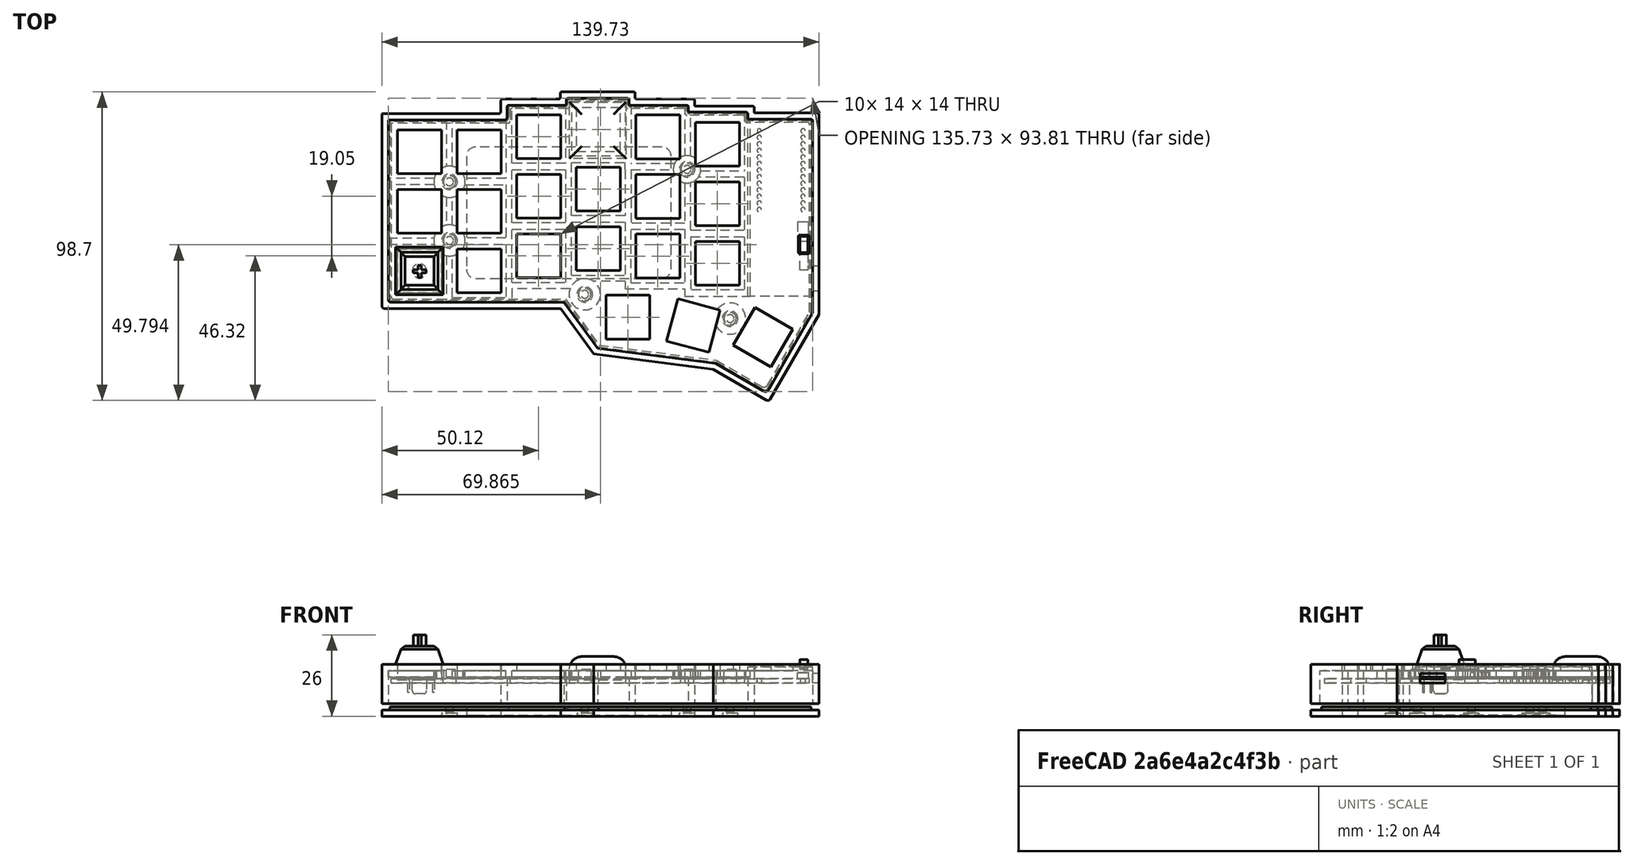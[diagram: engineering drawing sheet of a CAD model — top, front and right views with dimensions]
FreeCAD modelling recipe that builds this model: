
FCSTD DOCUMENT  (FreeCAD 0.22R37841 (Git))
Label: Corne 42 Case Clone
License: All rights reserved
LicenseURL: http://en.wikipedia.org/wiki/All_rights_reserved
objects: Sketcher::SketchObject×38, PartDesign::Pad×18, PartDesign::Pocket×13, PartDesign::Body×6, PartDesign::Fillet×3, App::DocumentObjectGroup×2, PartDesign::ShapeBinder×2, Spreadsheet::Sheet×1, Mesh::Feature×1, PartDesign::Chamfer×1
note: 116 computed .brp shape members not serialized (recipe doc carries the construction recipe); baked Part::Feature solids carry a one-line shape summary decoded from their .brp

FEATURE [Spreadsheet::Sheet] Spreadsheet
  cells = A1='PCBInnerBorderSpacing; B1(PCBInnerBorderSpacing)=1; A2='CaseTopBorderWitdh; B2(CaseTopBorderWitdh)=2; A3='SwitchBorderSpacing; B3(SwitchBorderSpacing)=2; A4='PCBBorderRadius; B4(PCBBorderRadius)=0.632; A5='PCBSmallStep; B5(PCBSmallStep)=2.25; A6='PCBBigStep; B6(PCBBigStep)=4.75; A7='SwitchplateHeight; B7(SwitchplateHeight)=2; A8='CaseTopTopBorderHeight; B8(CaseTopTopBorderHeight)=7; A9='CaseTopBottomBorderHeight; B9(CaseTopBottomBorderHeight)=6; A10='CaseColumnDiameter; B10(CaseColumnDiameter)=5; A11='ThreadedInsertHeight; B11(ThreadedInsertHeight)=3; A12='ThreadedInsertExtDiameter; B12(ThreadedInsertExtDiameter)=3.9; A13='PCBHoleSize; B13(PCBHoleSize)=4.2; A14='USBCPocketWidth; B14(USBCPocketWidth)=13.2; A15='USBCPocketHEIGHT; B15(USBCPocketHeight)=7.4; A16='CaseBottomPartHeight; B16(CaseBottomPartHeight)==CaseBottomFloorHeight + CaseBottomBorder; A17='CaseBottomFloorHeight; B17(CaseBottomFloorHeight)=3; A18='CaseBottomBorder; B18(CaseBottomBorder)=10; A19='ShadowLineWidth; B19(ShadowLineWidth)==CaseTopBorderWitdh - ShadowLineLipWidth; A20='ShadowLineLipWidth; B20(ShadowLineLipWidth)=0.6; A21='ResetSwitchHeight; B21(ResetSwitchHeight)=2.6; A22='PowerSwitchHeight; B22(PowerSwitchHeight)==3 - 1.4
FEATURE [Sketcher::SketchObject] MirroredSketch003  label="PCB.Borders"
  FullyConstrained = true
  expr: Constraints[41] = Spreadsheet.PCBBorderRadius
  expr: Constraints[44] = Spreadsheet.PCBBorderRadius
  expr: Constraints[47] = Spreadsheet.PCBBorderRadius
  expr: Constraints[52] = Spreadsheet.PCBBorderRadius
  expr: Constraints[53] = Spreadsheet.PCBBorderRadius
  expr: Constraints[56] = Spreadsheet.PCBBorderRadius
  expr: Constraints[59] = Spreadsheet.PCBBorderRadius
  expr: Constraints[62] = Spreadsheet.PCBBorderRadius
  expr: Constraints[65] = Spreadsheet.PCBBorderRadius
  expr: Constraints[68] = Spreadsheet.PCBBorderRadius
  expr: Constraints[74] = Spreadsheet.PCBBorderRadius
  expr: Constraints[79] = Spreadsheet.PCBBorderRadius
  expr: Constraints[86] = Spreadsheet.PCBSmallStep
  expr: Constraints[87] = Spreadsheet.PCBSmallStep
  expr: Constraints[88] = Spreadsheet.PCBSmallStep
  expr: Constraints[89] = Spreadsheet.PCBSmallStep
  expr: Constraints[90] = Spreadsheet.PCBBigStep
  sketch-geometry (38):
    g0: LineSegment StartX=0 StartY=56.25 StartZ=0 EndX=0 EndY=0.632 EndZ=0
    g1: LineSegment StartX=0.632 StartY=0 StartZ=0 EndX=55.6983 EndY=0 EndZ=0
    g2: LineSegment StartX=55.6983 StartY=0 StartZ=0 EndX=66.4243 EndY=-14.7035 EndZ=0
    g3: LineSegment StartX=66.4243 StartY=-14.7035 StartZ=0 EndX=103.928 EndY=-19.5811 EndZ=0
    g4: LineSegment StartX=103.928 StartY=-19.5811 StartZ=0 EndX=118.437 EndY=-27.9743 EndZ=0
    g5: LineSegment StartX=120.31 StartY=-27.472 StartZ=0 EndX=133.73 EndY=-4.162 EndZ=0
    g6: LineSegment StartX=133.73 StartY=-4.162 StartZ=0 EndX=133.73 EndY=55.868 EndZ=0
    g7: LineSegment StartX=133.098 StartY=56.5 StartZ=0 EndX=113.612 EndY=56.5 EndZ=0
    g8: LineSegment StartX=112.98 StartY=57.132 StartZ=0 EndX=112.98 EndY=58.118 EndZ=0
    g9: LineSegment StartX=112.348 StartY=58.75 StartZ=0 EndX=94.612 EndY=58.75 EndZ=0
    g10: LineSegment StartX=93.98 StartY=59.382 StartZ=0 EndX=93.98 EndY=60.368 EndZ=0
    g11: LineSegment StartX=93.348 StartY=61 StartZ=0 EndX=75.612 EndY=61 EndZ=0
    g12: LineSegment StartX=74.98 StartY=61.632 StartZ=0 EndX=74.98 EndY=62.618 EndZ=0
    g13: LineSegment StartX=74.348 StartY=63.25 StartZ=0 EndX=57.612 EndY=63.25 EndZ=0
    g14: LineSegment StartX=56.98 StartY=62.618 StartZ=0 EndX=56.98 EndY=61.632 EndZ=0
    g15: LineSegment StartX=56.348 StartY=61 StartZ=0 EndX=38.612 EndY=61 EndZ=0
    g16: LineSegment StartX=37.98 StartY=60.368 StartZ=0 EndX=37.98 EndY=56.882 EndZ=0
    g17: LineSegment StartX=37.348 StartY=56.25 StartZ=0 EndX=0 EndY=56.25 EndZ=0
    g18: Circle CenterX=18.61 CenterY=37.51 CenterZ=0 NormalX=0 NormalY=0 NormalZ=1 AngleXU=0 Radius=2.15
    g19: Circle CenterX=18.6 CenterY=18.76 CenterZ=0 NormalX=0 NormalY=0 NormalZ=1 AngleXU=0 Radius=2.15
    g20: Circle CenterX=108.3 CenterY=-6.24 CenterZ=0 NormalX=0 NormalY=0 NormalZ=1 AngleXU=0 Radius=2.15
    g21: Circle CenterX=94.55 CenterY=41.5 CenterZ=0 NormalX=0 NormalY=0 NormalZ=1 AngleXU=0 Radius=2.15
    g22: Circle CenterX=61.84 CenterY=1.51 CenterZ=0 NormalX=0 NormalY=0 NormalZ=1 AngleXU=0 Radius=2.15
    g23: ArcOfCircle CenterX=37.348 CenterY=56.882 CenterZ=0 NormalX=0 NormalY=0 NormalZ=1 AngleXU=0 Radius=0.632 StartAngle=4.71239 EndAngle=6.28319
    g24: ArcOfCircle CenterX=56.348 CenterY=61.632 CenterZ=0 NormalX=0 NormalY=0 NormalZ=1 AngleXU=0 Radius=0.632 StartAngle=4.71239 EndAngle=6.28319
    g25: ArcOfCircle CenterX=75.612 CenterY=61.632 CenterZ=0 NormalX=0 NormalY=0 NormalZ=1 AngleXU=0 Radius=0.632 StartAngle=3.14159 EndAngle=4.71239
    g26: ArcOfCircle CenterX=57.612 CenterY=62.618 CenterZ=0 NormalX=0 NormalY=0 NormalZ=1 AngleXU=0 Radius=0.632 StartAngle=1.5708 EndAngle=3.14159
    g27: ArcOfCircle CenterX=74.348 CenterY=62.618 CenterZ=0 NormalX=0 NormalY=0 NormalZ=1 AngleXU=0 Radius=0.632 StartAngle=5e-15 EndAngle=1.5708
    g28: ArcOfCircle CenterX=93.348 CenterY=60.368 CenterZ=0 NormalX=0 NormalY=0 NormalZ=1 AngleXU=0 Radius=0.632 StartAngle=-9e-16 EndAngle=1.5708
    g29: ArcOfCircle CenterX=94.612 CenterY=59.382 CenterZ=0 NormalX=0 NormalY=0 NormalZ=1 AngleXU=0 Radius=0.632 StartAngle=3.14159 EndAngle=4.71239
    g30: ArcOfCircle CenterX=112.348 CenterY=58.118 CenterZ=0 NormalX=0 NormalY=0 NormalZ=1 AngleXU=0 Radius=0.632 StartAngle=-9e-16 EndAngle=1.5708
    g31: ArcOfCircle CenterX=113.612 CenterY=57.132 CenterZ=0 NormalX=0 NormalY=0 NormalZ=1 AngleXU=0 Radius=0.632 StartAngle=3.14159 EndAngle=4.71239
    g32: ArcOfCircle CenterX=133.098 CenterY=55.868 CenterZ=0 NormalX=0 NormalY=0 NormalZ=1 AngleXU=0 Radius=0.632 StartAngle=-5.3e-15 EndAngle=1.5708
    g33: ArcOfCircle CenterX=119.123 CenterY=-26.7885 CenterZ=0 NormalX=0 NormalY=0 NormalZ=1 AngleXU=0 Radius=1.37 StartAngle=4.18792 EndAngle=5.76081
    g34: ArcOfCircle CenterX=0.632 CenterY=0.632 CenterZ=0 NormalX=0 NormalY=0 NormalZ=1 AngleXU=0 Radius=0.632 StartAngle=3.14159 EndAngle=4.71239
    g35: ArcOfCircle CenterX=38.612 CenterY=60.368 CenterZ=0 NormalX=0 NormalY=0 NormalZ=1 AngleXU=0 Radius=0.632 StartAngle=1.5708 EndAngle=3.14159
    g36: LineSegment StartX=122.07 StartY=-24.4153 StartZ=0 EndX=119.625 EndY=-28.6618 EndZ=0
    g37: LineSegment StartX=116.44 StartY=-26.819 StartZ=0 EndX=119.625 EndY=-28.6618 EndZ=0
  constraints (102):
    c: Horizontal(g1)
    c: Vertical(g0)
    c: Coincident(g1,g2)
    c: Coincident(g2,g3)
    c: Coincident(g3,g4)
    c: Coincident(g5,g6)
    c: Coincident(g17,g0)
    c: Vertical(g6)
    c: Horizontal(g7)
    c: Horizontal(g9)
    c: Horizontal(g11)
    c: Horizontal(g13)
    c: Horizontal(g15)
    c: Horizontal(g17)
    c: Vertical(g16)
    c: Vertical(g14)
    c: Vertical(g12)
    c: Vertical(g10)
    c: Vertical(g8)
    c: Angle(g5,g6) = -2.61922
    c: Angle(g4,g5) = -1.5687
    c: Angle(g4,g3) = -2.74645
    c: Angle(g2,g3) = -2.33036
    c: Diameter(g20) = 4.3
    c: Diameter(g21) = 4.3
    c: Diameter(g18) = 4.3
    c: Diameter(g19) = 4.3
    c: Distance(g18,g0) = 18.61
    c: Distance(g19,g18) = 18.75
    c: Distance(g19,g0) = 18.6
    c: Distance(g21,g6) = 39.18
    c: Distance(g21,g9) = 17.25
    c: Distance(g20,g6) = 25.43
    c: Distance(g3) = 37.82
    c: Distance(g19,g1) = 18.76
    c: Diameter(g22) = 4.3
    c: DistanceX(g19,g22) = 43.24
    c: DistanceY(g22,g19) = 17.25
    c: DistanceY(g20,g22) = 7.75
    c: Tangent(g16,g23) = 1.5708
    c: Tangent(g17,g23) = 1.5708
    c: Radius(g23) = 0.632
    c: Tangent(g14,g24) = 1.5708
    c: Tangent(g15,g24) = 1.5708
    c: Radius(g24) = 0.632
    c: Tangent(g12,g25) = 1.5708
    c: Tangent(g11,g25) = 1.5708
    c: Radius(g25) = 0.632
    c: Tangent(g13,g26) = -1.5708
    c: Tangent(g14,g26) = -1.5708
    c: Tangent(g13,g27) = -1.5708
    c: Tangent(g12,g27) = -1.5708
    c: Radius(g26) = 0.632
    c: Radius(g27) = 0.632
    c: Tangent(g11,g28) = -1.5708
    c: Tangent(g10,g28) = -1.5708
    c: Radius(g28) = 0.632
    c: Tangent(g10,g29) = 1.5708
    c: Tangent(g9,g29) = 1.5708
    c: Radius(g29) = 0.632
    c: Tangent(g9,g30) = -1.5708
    c: Tangent(g8,g30) = -1.5708
    c: Radius(g30) = 0.632
    c: Tangent(g8,g31) = 1.5708
    c: Tangent(g7,g31) = 1.5708
    c: Radius(g31) = 0.632
    c: Tangent(g7,g32) = -1.5708
    c: Tangent(g6,g32) = -1.5708
    c: Radius(g32) = 0.632
    c: Tangent(g5,g33) = -1.5708
    c: Tangent(g4,g33) = -1.5708
    c: Radius(g33) = 1.37
    c: Tangent(g1,g34) = -1.5708
    c: Tangent(g0,g34) = -1.5708
    c: Radius(g34) = 0.632
    c: DistanceY(g-1,g1) = 0
    c: DistanceX(g-2,g0) = 0
    c: Tangent(g15,g35) = -1.5708
    c: Tangent(g16,g35) = -1.5708
    c: Radius(g35) = 0.632
    c: Distance(g16,g0) = 37.98
    c: Distance(g14,g16) = 19
    c: Distance(g14,g12) = 18
    c: Distance(g10,g12) = 19
    c: Distance(g10,g8) = 19
    c: Distance(g6,g8) = 20.75
    c: Distance(g7,g9) = 2.25
    c: Distance(g9,g11) = 2.25
    c: Distance(g11,g13) = 2.25
    c: Distance(g15,g13) = 2.25
    c: Distance(g15,g17) = 4.75
    c: Distance(g1,g17) = 56.25
    c: Distance(g2) = 18.2
    c: DistanceY(g6,g6) = 60.03
    c: PointOnObject(g36,g5)
    c: Tangent(g36,g33)
    c: PointOnObject(g37,g4)
    c: Tangent(g37,g33)
    c: Coincident(g36,g37)
    c: Distance(g5,g36) = 28.27
    c: Distance(g36) = 4.9
    c: Distance(g37) = 3.68
FEATURE [Sketcher::SketchObject] Sketch
  FullyConstrained = true
  MapMode = 5
  Placement = pos=(66,54,3) rot=(0,0,1;0rad)
  sketch-geometry (4):
    g0: LineSegment StartX=-9.05 StartY=9.05 StartZ=0 EndX=9.05 EndY=9.05 EndZ=0
    g1: LineSegment StartX=9.05 StartY=9.05 StartZ=0 EndX=9.05 EndY=-9.05 EndZ=0
    g2: LineSegment StartX=9.05 StartY=-9.05 StartZ=0 EndX=-9.05 EndY=-9.05 EndZ=0
    g3: LineSegment StartX=-9.05 StartY=-9.05 StartZ=0 EndX=-9.05 EndY=9.05 EndZ=0
  constraints (11):
    c: Coincident(g0,g1)
    c: Coincident(g1,g2)
    c: Coincident(g2,g3)
    c: Coincident(g3,g0)
    c: Horizontal(g0)
    c: Horizontal(g2)
    c: Vertical(g1)
    c: Vertical(g3)
    c: Symmetric(g0,g1,g-1)
    c: Equal(g0,g1)
    c: Distance(g0) = 18.1
FEATURE [PartDesign::Pad] Pad007
  Direction = (0,0,1)
  Length = 7.5
  Length2 = 10
  Placement = pos=(66,54,3) rot=(0,0,1;0rad)
  Profile = -> Sketch
  ReferenceAxis = -> Sketch [N_Axis]
  Suppressed = false
  Type = 0
FEATURE [Mesh::Feature] xda_keycap
  Placement = pos=(-0.25,-0.45,14.5) rot=(0,0,1;0rad)
FEATURE [PartDesign::Fillet] Fillet
  Base = -> Pad007 [Face6]
  BaseFeature = -> Pad007
  Placement = pos=(66,54,3) rot=(0,0,1;0rad)
  Radius = 4
  SupportTransform = false
  Suppressed = false
  UseAllEdges = false
FEATURE [PartDesign::Body] Body002  label="Switch"
  AllowCompound = false
  Group = -> [Sketch,Pad007,Fillet]
  Origin = -> Origin002
  Tip = -> Fillet
FEATURE [Sketcher::SketchObject] Sketch054  label="Case.SwitchPlateBody"
  ExternalGeometry = -> [MirroredSketch003]
  FullyConstrained = false
  Placement = pos=(0,0,6) rot=(0,0,1;0rad)
  expr: .Placement.Base.z = Spreadsheet.CaseTopBottomBorderHeight
  expr: Constraints[22] = Spreadsheet.PCBInnerBorderSpacing + Spreadsheet.CaseTopBorderWitdh
  expr: Constraints[26] = Spreadsheet.PCBInnerBorderSpacing + Spreadsheet.CaseTopBorderWitdh
  expr: Constraints[27] = Spreadsheet.PCBInnerBorderSpacing + Spreadsheet.CaseTopBorderWitdh
  expr: Constraints[28] = Spreadsheet.PCBInnerBorderSpacing + Spreadsheet.CaseTopBorderWitdh
  expr: Constraints[32] = Spreadsheet.PCBInnerBorderSpacing + Spreadsheet.CaseTopBorderWitdh
  expr: Constraints[33] = Spreadsheet.PCBInnerBorderSpacing + Spreadsheet.CaseTopBorderWitdh
  expr: Constraints[34] = Spreadsheet.PCBInnerBorderSpacing + Spreadsheet.CaseTopBorderWitdh
  expr: Constraints[35] = Spreadsheet.PCBInnerBorderSpacing + Spreadsheet.CaseTopBorderWitdh
  expr: Constraints[36] = Spreadsheet.PCBInnerBorderSpacing + Spreadsheet.CaseTopBorderWitdh
  expr: Constraints[37] = Spreadsheet.PCBInnerBorderSpacing + Spreadsheet.CaseTopBorderWitdh
  expr: Constraints[38] = Spreadsheet.PCBInnerBorderSpacing + Spreadsheet.CaseTopBorderWitdh
  expr: Constraints[39] = Spreadsheet.PCBInnerBorderSpacing + Spreadsheet.CaseTopBorderWitdh
  expr: Constraints[44] = Spreadsheet.PCBInnerBorderSpacing + Spreadsheet.CaseTopBorderWitdh
  expr: Constraints[46] = Spreadsheet.PCBInnerBorderSpacing + Spreadsheet.CaseTopBorderWitdh
  expr: Constraints[50] = Spreadsheet.PCBInnerBorderSpacing + Spreadsheet.CaseTopBorderWitdh
  expr: Constraints[54] = Spreadsheet.PCBInnerBorderSpacing + Spreadsheet.CaseTopBorderWitdh
  expr: Constraints[59] = Spreadsheet.PCBInnerBorderSpacing + Spreadsheet.CaseTopBorderWitdh
  expr: Constraints[63] = Spreadsheet.PCBInnerBorderSpacing + Spreadsheet.CaseTopBorderWitdh
  sketch-geometry (39):
    g0: LineSegment StartX=-3 StartY=59.25 StartZ=0 EndX=34.2901 EndY=59.25 EndZ=0
    g1: LineSegment StartX=34.98 StartY=59.9399 StartZ=0 EndX=34.98 EndY=63.1957 EndZ=0
    g2: LineSegment StartX=35.7843 StartY=64 StartZ=0 EndX=53.5317 EndY=64 EndZ=0
    g3: LineSegment StartX=53.98 StartY=64.4483 StartZ=0 EndX=53.98 EndY=65.7804 EndZ=0
    g4: LineSegment StartX=54.4496 StartY=66.25 StartZ=0 EndX=77.5616 EndY=66.25 EndZ=0
    g5: LineSegment StartX=77.98 StartY=65.8316 StartZ=0 EndX=77.98 EndY=64.3517 EndZ=0
    g6: LineSegment StartX=78.3317 StartY=64 StartZ=0 EndX=96.3966 EndY=64 EndZ=0
    g7: LineSegment StartX=96.98 StartY=63.4166 StartZ=0 EndX=96.98 EndY=61.9688 EndZ=0
    g8: LineSegment StartX=97.1988 StartY=61.75 StartZ=0 EndX=115.529 EndY=61.75 EndZ=0
    g9: LineSegment StartX=115.98 StartY=61.2993 StartZ=0 EndX=115.98 EndY=59.8538 EndZ=0
    g10: LineSegment StartX=116.334 StartY=59.5 StartZ=0 EndX=136.112 EndY=59.5 EndZ=0
    g11: LineSegment StartX=136.73 StartY=58.8821 StartZ=0 EndX=136.73 EndY=-4.96388 EndZ=0
    g12: LineSegment StartX=136.73 StartY=-4.96388 StartZ=0 EndX=121.154 EndY=-32.0193 EndZ=0
    g13: LineSegment StartX=119.981 StartY=-32.3337 StartZ=0 EndX=102.946 EndY=-22.4786 EndZ=0
    g14: LineSegment StartX=102.946 StartY=-22.4786 StartZ=0 EndX=64.7598 EndY=-17.5123 EndZ=0
    g15: LineSegment StartX=64.7598 StartY=-17.5123 StartZ=0 EndX=54.1734 EndY=-3 EndZ=0
    g16: LineSegment StartX=54.1734 StartY=-3 StartZ=0 EndX=-2.2752 EndY=-3 EndZ=0
    g17: LineSegment StartX=-3 StartY=-2.2752 StartZ=0 EndX=-3 EndY=59.25 EndZ=0
    g18: LineSegment StartX=18.674 StartY=56.25 StartZ=0 EndX=18.674 EndY=59.25 EndZ=0
    g19: LineSegment StartX=47.3598 StartY=61 StartZ=0 EndX=47.3598 EndY=64 EndZ=0
    g20: LineSegment StartX=65.8007 StartY=63.25 StartZ=0 EndX=65.8007 EndY=66.25 EndZ=0
    g21: LineSegment StartX=128.098 StartY=-13.9439 StartZ=0 EndX=130.698 EndY=-15.4407 EndZ=0
    g22: LineSegment StartX=90.2517 StartY=-17.8024 StartZ=0 EndX=89.8648 EndY=-20.7774 EndZ=0
    g23: LineSegment StartX=62.9864 StartY=-9.99077 StartZ=0 EndX=60.5627 EndY=-11.7588 EndZ=0
    g24: LineSegment StartX=27.8823 StartY=0 StartZ=0 EndX=27.8823 EndY=-3 EndZ=0
    g25: LineSegment StartX=0 StartY=28.1957 StartZ=0 EndX=-3 EndY=28.1957 EndZ=0
    g26: ArcOfCircle CenterX=34.2901 CenterY=59.9399 CenterZ=0 NormalX=0 NormalY=0 NormalZ=1 AngleXU=0 Radius=0.689901 StartAngle=4.71239 EndAngle=6.28319
    g27: ArcOfCircle CenterX=35.7843 CenterY=63.1957 CenterZ=0 NormalX=0 NormalY=0 NormalZ=1 AngleXU=0 Radius=0.804272 StartAngle=1.5708 EndAngle=3.14159
    g28: ArcOfCircle CenterX=53.5317 CenterY=64.4483 CenterZ=0 NormalX=0 NormalY=0 NormalZ=1 AngleXU=0 Radius=0.448303 StartAngle=4.71239 EndAngle=6.28319
    g29: ArcOfCircle CenterX=54.4496 CenterY=65.7804 CenterZ=0 NormalX=0 NormalY=0 NormalZ=1 AngleXU=0 Radius=0.469571 StartAngle=1.5708 EndAngle=3.14159
    g30: ArcOfCircle CenterX=77.5616 CenterY=65.8316 CenterZ=0 NormalX=0 NormalY=0 NormalZ=1 AngleXU=0 Radius=0.418401 StartAngle=0 EndAngle=1.5708
    g31: ArcOfCircle CenterX=78.3317 CenterY=64.3517 CenterZ=0 NormalX=0 NormalY=0 NormalZ=1 AngleXU=0 Radius=0.3517 StartAngle=3.14159 EndAngle=4.71239
    g32: ArcOfCircle CenterX=96.3966 CenterY=63.4166 CenterZ=0 NormalX=0 NormalY=0 NormalZ=1 AngleXU=0 Radius=0.583444 StartAngle=0 EndAngle=1.5708
    g33: ArcOfCircle CenterX=97.1988 CenterY=61.9688 CenterZ=0 NormalX=0 NormalY=0 NormalZ=1 AngleXU=0 Radius=0.218754 StartAngle=3.14159 EndAngle=4.71239
    g34: ArcOfCircle CenterX=115.529 CenterY=61.2993 CenterZ=0 NormalX=0 NormalY=0 NormalZ=1 AngleXU=0 Radius=0.450718 StartAngle=0 EndAngle=1.5708
    g35: ArcOfCircle CenterX=116.334 CenterY=59.8538 CenterZ=0 NormalX=0 NormalY=0 NormalZ=1 AngleXU=0 Radius=0.353806 StartAngle=3.14159 EndAngle=4.71239
    g36: ArcOfCircle CenterX=136.112 CenterY=58.8821 CenterZ=0 NormalX=0 NormalY=0 NormalZ=1 AngleXU=0 Radius=0.617924 StartAngle=-9e-16 EndAngle=1.5708
    g37: ArcOfCircle CenterX=120.41 CenterY=-31.5915 CenterZ=0 NormalX=0 NormalY=0 NormalZ=1 AngleXU=0 Radius=0.857438 StartAngle=4.18792 EndAngle=5.76081
    g38: ArcOfCircle CenterX=-2.2752 CenterY=-2.2752 CenterZ=0 NormalX=0 NormalY=0 NormalZ=1 AngleXU=0 Radius=0.7248 StartAngle=3.14159 EndAngle=4.71239
  constraints (91):
    c: Horizontal(g0)
    c: Vertical(g1)
    c: Horizontal(g2)
    c: Vertical(g3)
    c: Horizontal(g4)
    c: Vertical(g5)
    c: Horizontal(g6)
    c: Vertical(g7)
    c: Horizontal(g8)
    c: Vertical(g9)
    c: Horizontal(g10)
    c: Vertical(g11)
    c: Coincident(g11,g12)
    c: Coincident(g13,g14)
    c: Coincident(g14,g15)
    c: Coincident(g15,g16)
    c: Horizontal(g16)
    c: Coincident(g17,g0)
    c: Vertical(g17)
    c: PointOnObject(g18,g-3)
    c: PointOnObject(g18,g0)
    c: Vertical(g18)
    c: Distance(g18) = 3
    c: PointOnObject(g19,g-5)
    c: PointOnObject(g19,g2)
    c: Vertical(g19)
    c: Distance(g-4,g1) = 3
    c: Distance(g-6,g3) = 3
    c: Distance(g19) = 3
    c: PointOnObject(g20,g-7)
    c: PointOnObject(g20,g4)
    c: Perpendicular(g20,g-7)
    c: Distance(g20) = 3
    c: Distance(g-8,g5) = 3
    c: Distance(g-9,g6) = 3
    c: Distance(g-11,g8) = 3
    c: Distance(g-10,g7) = 3
    c: Distance(g-12,g9) = 3
    c: Distance(g-13,g10) = 3
    c: Distance(g-14,g11) = 3
    c: PointOnObject(g21,g-15)
    c: PointOnObject(g21,g12)
    c: Perpendicular(g-15,g21)
    c: Parallel(g12,g-15)
    c: Distance(g21) = 3
    c: Parallel(g13,g-16)
    c: Distance(g-16,g13) = 3
    c: PointOnObject(g22,g-17)
    c: PointOnObject(g22,g14)
    c: Perpendicular(g-17,g22)
    c: Distance(g22) = 3
    c: PointOnObject(g23,g-18)
    c: PointOnObject(g23,g15)
    c: Perpendicular(g-18,g23)
    c: Distance(g23) = 3
    c: Parallel(g15,g-18)
    c: PointOnObject(g24,g-19)
    c: PointOnObject(g24,g16)
    c: Perpendicular(g-19,g24)
    c: Distance(g24) = 3
    c: PointOnObject(g25,g-20)
    c: PointOnObject(g25,g17)
    c: Perpendicular(g-20,g25)
    c: Distance(g25) = 3
    c: Tangent(g1,g26) = -1.5708
    c: Tangent(g0,g26) = -1.5708
    c: Tangent(g2,g27) = 1.5708
    c: Tangent(g1,g27) = 1.5708
    c: Tangent(g3,g28) = -1.5708
    c: Tangent(g2,g28) = -1.5708
    c: Tangent(g3,g29) = 1.5708
    c: Tangent(g4,g29) = 1.5708
    c: Tangent(g4,g30) = 1.5708
    c: Tangent(g5,g30) = 1.5708
    c: Tangent(g5,g31) = -1.5708
    c: Tangent(g6,g31) = -1.5708
    c: Tangent(g6,g32) = 1.5708
    c: Tangent(g7,g32) = 1.5708
    c: Tangent(g7,g33) = -1.5708
    c: Tangent(g8,g33) = -1.5708
    c: Tangent(g8,g34) = 1.5708
    c: Tangent(g9,g34) = 1.5708
    c: Tangent(g9,g35) = -1.5708
    c: Tangent(g10,g35) = -1.5708
    c: Tangent(g10,g36) = 1.5708
    c: Tangent(g11,g36) = 1.5708
    c: Tangent(g12,g37) = 1.5708
    c: Tangent(g13,g37) = 1.5708
    c: Tangent(g17,g38) = 1.5708
    c: Tangent(g16,g38) = 1.5708
    c: Parallel(g14,g-17)
FEATURE [PartDesign::Pad] Pad  label="Case.SwitchPlate.Body"
  Direction = (0,0,1)
  Length = 2
  Length2 = 10
  Placement = pos=(0,0,6) rot=(0,0,1;0rad)
  Profile = -> Sketch054
  ReferenceAxis = -> Sketch054 [N_Axis]
  Suppressed = false
  Type = 0
  expr: Length = Spreadsheet.SwitchplateHeight
FEATURE [Sketcher::SketchObject] MirroredSketch004  label="PCB.Borders001"
  AttachmentSupport = -> [XY_Plane001]
  FullyConstrained = true
  expr: Constraints[41] = Spreadsheet.PCBBorderRadius
  expr: Constraints[44] = Spreadsheet.PCBBorderRadius
  expr: Constraints[47] = Spreadsheet.PCBBorderRadius
  expr: Constraints[52] = Spreadsheet.PCBBorderRadius
  expr: Constraints[53] = Spreadsheet.PCBBorderRadius
  expr: Constraints[56] = Spreadsheet.PCBBorderRadius
  expr: Constraints[59] = Spreadsheet.PCBBorderRadius
  expr: Constraints[62] = Spreadsheet.PCBBorderRadius
  expr: Constraints[65] = Spreadsheet.PCBBorderRadius
  expr: Constraints[68] = Spreadsheet.PCBBorderRadius
  expr: Constraints[74] = Spreadsheet.PCBBorderRadius
  expr: Constraints[79] = Spreadsheet.PCBBorderRadius
  expr: Constraints[86] = Spreadsheet.PCBSmallStep
  expr: Constraints[87] = Spreadsheet.PCBSmallStep
  expr: Constraints[88] = Spreadsheet.PCBSmallStep
  expr: Constraints[89] = Spreadsheet.PCBSmallStep
  expr: Constraints[90] = Spreadsheet.PCBBigStep
  sketch-geometry (38):
    g0: LineSegment StartX=0 StartY=56.25 StartZ=0 EndX=0 EndY=0.632 EndZ=0
    g1: LineSegment StartX=0.632 StartY=0 StartZ=0 EndX=55.6983 EndY=0 EndZ=0
    g2: LineSegment StartX=55.6983 StartY=0 StartZ=0 EndX=66.4243 EndY=-14.7035 EndZ=0
    g3: LineSegment StartX=66.4243 StartY=-14.7035 StartZ=0 EndX=103.928 EndY=-19.5811 EndZ=0
    g4: LineSegment StartX=103.928 StartY=-19.5811 StartZ=0 EndX=118.437 EndY=-27.9743 EndZ=0
    g5: LineSegment StartX=120.31 StartY=-27.472 StartZ=0 EndX=133.73 EndY=-4.162 EndZ=0
    g6: LineSegment StartX=133.73 StartY=-4.162 StartZ=0 EndX=133.73 EndY=55.868 EndZ=0
    g7: LineSegment StartX=133.098 StartY=56.5 StartZ=0 EndX=113.612 EndY=56.5 EndZ=0
    g8: LineSegment StartX=112.98 StartY=57.132 StartZ=0 EndX=112.98 EndY=58.118 EndZ=0
    g9: LineSegment StartX=112.348 StartY=58.75 StartZ=0 EndX=94.612 EndY=58.75 EndZ=0
    g10: LineSegment StartX=93.98 StartY=59.382 StartZ=0 EndX=93.98 EndY=60.368 EndZ=0
    g11: LineSegment StartX=93.348 StartY=61 StartZ=0 EndX=75.612 EndY=61 EndZ=0
    g12: LineSegment StartX=74.98 StartY=61.632 StartZ=0 EndX=74.98 EndY=62.618 EndZ=0
    g13: LineSegment StartX=74.348 StartY=63.25 StartZ=0 EndX=57.612 EndY=63.25 EndZ=0
    g14: LineSegment StartX=56.98 StartY=62.618 StartZ=0 EndX=56.98 EndY=61.632 EndZ=0
    g15: LineSegment StartX=56.348 StartY=61 StartZ=0 EndX=38.612 EndY=61 EndZ=0
    g16: LineSegment StartX=37.98 StartY=60.368 StartZ=0 EndX=37.98 EndY=56.882 EndZ=0
    g17: LineSegment StartX=37.348 StartY=56.25 StartZ=0 EndX=0 EndY=56.25 EndZ=0
    g18: Circle CenterX=18.61 CenterY=37.51 CenterZ=0 NormalX=0 NormalY=0 NormalZ=1 AngleXU=0 Radius=2.15
    g19: Circle CenterX=18.6 CenterY=18.76 CenterZ=0 NormalX=0 NormalY=0 NormalZ=1 AngleXU=0 Radius=2.15
    g20: Circle CenterX=108.3 CenterY=-6.24 CenterZ=0 NormalX=0 NormalY=0 NormalZ=1 AngleXU=0 Radius=2.15
    g21: Circle CenterX=94.55 CenterY=41.5 CenterZ=0 NormalX=0 NormalY=0 NormalZ=1 AngleXU=0 Radius=2.15
    g22: Circle CenterX=61.84 CenterY=1.51 CenterZ=0 NormalX=0 NormalY=0 NormalZ=1 AngleXU=0 Radius=2.15
    g23: ArcOfCircle CenterX=37.348 CenterY=56.882 CenterZ=0 NormalX=0 NormalY=0 NormalZ=1 AngleXU=0 Radius=0.632 StartAngle=4.71239 EndAngle=6.28319
    g24: ArcOfCircle CenterX=56.348 CenterY=61.632 CenterZ=0 NormalX=0 NormalY=0 NormalZ=1 AngleXU=0 Radius=0.632 StartAngle=4.71239 EndAngle=6.28319
    g25: ArcOfCircle CenterX=75.612 CenterY=61.632 CenterZ=0 NormalX=0 NormalY=0 NormalZ=1 AngleXU=0 Radius=0.632 StartAngle=3.14159 EndAngle=4.71239
    g26: ArcOfCircle CenterX=57.612 CenterY=62.618 CenterZ=0 NormalX=0 NormalY=0 NormalZ=1 AngleXU=0 Radius=0.632 StartAngle=1.5708 EndAngle=3.14159
    g27: ArcOfCircle CenterX=74.348 CenterY=62.618 CenterZ=0 NormalX=0 NormalY=0 NormalZ=1 AngleXU=0 Radius=0.632 StartAngle=5e-15 EndAngle=1.5708
    g28: ArcOfCircle CenterX=93.348 CenterY=60.368 CenterZ=0 NormalX=0 NormalY=0 NormalZ=1 AngleXU=0 Radius=0.632 StartAngle=-9e-16 EndAngle=1.5708
    g29: ArcOfCircle CenterX=94.612 CenterY=59.382 CenterZ=0 NormalX=0 NormalY=0 NormalZ=1 AngleXU=0 Radius=0.632 StartAngle=3.14159 EndAngle=4.71239
    g30: ArcOfCircle CenterX=112.348 CenterY=58.118 CenterZ=0 NormalX=0 NormalY=0 NormalZ=1 AngleXU=0 Radius=0.632 StartAngle=-9e-16 EndAngle=1.5708
    g31: ArcOfCircle CenterX=113.612 CenterY=57.132 CenterZ=0 NormalX=0 NormalY=0 NormalZ=1 AngleXU=0 Radius=0.632 StartAngle=3.14159 EndAngle=4.71239
    g32: ArcOfCircle CenterX=133.098 CenterY=55.868 CenterZ=0 NormalX=0 NormalY=0 NormalZ=1 AngleXU=0 Radius=0.632 StartAngle=-5.3e-15 EndAngle=1.5708
    g33: ArcOfCircle CenterX=119.123 CenterY=-26.7885 CenterZ=0 NormalX=0 NormalY=0 NormalZ=1 AngleXU=0 Radius=1.37 StartAngle=4.18792 EndAngle=5.76081
    g34: ArcOfCircle CenterX=0.632 CenterY=0.632 CenterZ=0 NormalX=0 NormalY=0 NormalZ=1 AngleXU=0 Radius=0.632 StartAngle=3.14159 EndAngle=4.71239
    g35: ArcOfCircle CenterX=38.612 CenterY=60.368 CenterZ=0 NormalX=0 NormalY=0 NormalZ=1 AngleXU=0 Radius=0.632 StartAngle=1.5708 EndAngle=3.14159
    g36: LineSegment StartX=122.07 StartY=-24.4153 StartZ=0 EndX=119.625 EndY=-28.6618 EndZ=0
    g37: LineSegment StartX=116.44 StartY=-26.819 StartZ=0 EndX=119.625 EndY=-28.6618 EndZ=0
  constraints (102):
    c: Horizontal(g1)
    c: Vertical(g0)
    c: Coincident(g1,g2)
    c: Coincident(g2,g3)
    c: Coincident(g3,g4)
    c: Coincident(g5,g6)
    c: Coincident(g17,g0)
    c: Vertical(g6)
    c: Horizontal(g7)
    c: Horizontal(g9)
    c: Horizontal(g11)
    c: Horizontal(g13)
    c: Horizontal(g15)
    c: Horizontal(g17)
    c: Vertical(g16)
    c: Vertical(g14)
    c: Vertical(g12)
    c: Vertical(g10)
    c: Vertical(g8)
    c: Angle(g5,g6) = -2.61922
    c: Angle(g4,g5) = -1.5687
    c: Angle(g4,g3) = -2.74645
    c: Angle(g2,g3) = -2.33036
    c: Diameter(g20) = 4.3
    c: Diameter(g21) = 4.3
    c: Diameter(g18) = 4.3
    c: Diameter(g19) = 4.3
    c: Distance(g18,g0) = 18.61
    c: Distance(g19,g18) = 18.75
    c: Distance(g19,g0) = 18.6
    c: Distance(g21,g6) = 39.18
    c: Distance(g21,g9) = 17.25
    c: Distance(g20,g6) = 25.43
    c: Distance(g3) = 37.82
    c: Distance(g19,g1) = 18.76
    c: Diameter(g22) = 4.3
    c: DistanceX(g19,g22) = 43.24
    c: DistanceY(g22,g19) = 17.25
    c: DistanceY(g20,g22) = 7.75
    c: Tangent(g16,g23) = 1.5708
    c: Tangent(g17,g23) = 1.5708
    c: Radius(g23) = 0.632
    c: Tangent(g14,g24) = 1.5708
    c: Tangent(g15,g24) = 1.5708
    c: Radius(g24) = 0.632
    c: Tangent(g12,g25) = 1.5708
    c: Tangent(g11,g25) = 1.5708
    c: Radius(g25) = 0.632
    c: Tangent(g13,g26) = -1.5708
    c: Tangent(g14,g26) = -1.5708
    c: Tangent(g13,g27) = -1.5708
    c: Tangent(g12,g27) = -1.5708
    c: Radius(g26) = 0.632
    c: Radius(g27) = 0.632
    c: Tangent(g11,g28) = -1.5708
    c: Tangent(g10,g28) = -1.5708
    c: Radius(g28) = 0.632
    c: Tangent(g10,g29) = 1.5708
    c: Tangent(g9,g29) = 1.5708
    c: Radius(g29) = 0.632
    c: Tangent(g9,g30) = -1.5708
    c: Tangent(g8,g30) = -1.5708
    c: Radius(g30) = 0.632
    c: Tangent(g8,g31) = 1.5708
    c: Tangent(g7,g31) = 1.5708
    c: Radius(g31) = 0.632
    c: Tangent(g7,g32) = -1.5708
    c: Tangent(g6,g32) = -1.5708
    c: Radius(g32) = 0.632
    c: Tangent(g5,g33) = -1.5708
    c: Tangent(g4,g33) = -1.5708
    c: Radius(g33) = 1.37
    c: Tangent(g1,g34) = -1.5708
    c: Tangent(g0,g34) = -1.5708
    c: Radius(g34) = 0.632
    c: DistanceY(g-1,g1) = 0
    c: DistanceX(g-2,g0) = 0
    c: Tangent(g15,g35) = -1.5708
    c: Tangent(g16,g35) = -1.5708
    c: Radius(g35) = 0.632
    c: Distance(g16,g0) = 37.98
    c: Distance(g14,g16) = 19
    c: Distance(g14,g12) = 18
    c: Distance(g10,g12) = 19
    c: Distance(g10,g8) = 19
    c: Distance(g6,g8) = 20.75
    c: Distance(g7,g9) = 2.25
    c: Distance(g9,g11) = 2.25
    c: Distance(g11,g13) = 2.25
    c: Distance(g15,g13) = 2.25
    c: Distance(g15,g17) = 4.75
    c: Distance(g1,g17) = 56.25
    c: Distance(g2) = 18.2
    c: DistanceY(g6,g6) = 60.03
    c: PointOnObject(g36,g5)
    c: Tangent(g36,g33)
    c: PointOnObject(g37,g4)
    c: Tangent(g37,g33)
    c: Coincident(g36,g37)
    c: Distance(g5,g36) = 28.27
    c: Distance(g36) = 4.9
    c: Distance(g37) = 3.68
FEATURE [Sketcher::SketchObject] Sketch056  label="Case.OuterBorders001"
  ExternalGeometry = -> [MirroredSketch003]
  FullyConstrained = false
  expr: Constraints[22] = Spreadsheet.PCBInnerBorderSpacing + Spreadsheet.CaseTopBorderWitdh
  expr: Constraints[26] = Spreadsheet.PCBInnerBorderSpacing + Spreadsheet.CaseTopBorderWitdh
  expr: Constraints[27] = Spreadsheet.PCBInnerBorderSpacing + Spreadsheet.CaseTopBorderWitdh
  expr: Constraints[28] = Spreadsheet.PCBInnerBorderSpacing + Spreadsheet.CaseTopBorderWitdh
  expr: Constraints[32] = Spreadsheet.PCBInnerBorderSpacing + Spreadsheet.CaseTopBorderWitdh
  expr: Constraints[33] = Spreadsheet.PCBInnerBorderSpacing + Spreadsheet.CaseTopBorderWitdh
  expr: Constraints[34] = Spreadsheet.PCBInnerBorderSpacing + Spreadsheet.CaseTopBorderWitdh
  expr: Constraints[35] = Spreadsheet.PCBInnerBorderSpacing + Spreadsheet.CaseTopBorderWitdh
  expr: Constraints[36] = Spreadsheet.PCBInnerBorderSpacing + Spreadsheet.CaseTopBorderWitdh
  expr: Constraints[37] = Spreadsheet.PCBInnerBorderSpacing + Spreadsheet.CaseTopBorderWitdh
  expr: Constraints[38] = Spreadsheet.PCBInnerBorderSpacing + Spreadsheet.CaseTopBorderWitdh
  expr: Constraints[39] = Spreadsheet.PCBInnerBorderSpacing + Spreadsheet.CaseTopBorderWitdh
  expr: Constraints[44] = Spreadsheet.PCBInnerBorderSpacing + Spreadsheet.CaseTopBorderWitdh
  expr: Constraints[46] = Spreadsheet.PCBInnerBorderSpacing + Spreadsheet.CaseTopBorderWitdh
  expr: Constraints[50] = Spreadsheet.PCBInnerBorderSpacing + Spreadsheet.CaseTopBorderWitdh
  expr: Constraints[54] = Spreadsheet.PCBInnerBorderSpacing + Spreadsheet.CaseTopBorderWitdh
  expr: Constraints[59] = Spreadsheet.PCBInnerBorderSpacing + Spreadsheet.CaseTopBorderWitdh
  expr: Constraints[63] = Spreadsheet.PCBInnerBorderSpacing + Spreadsheet.CaseTopBorderWitdh
  sketch-geometry (39):
    g0: LineSegment StartX=-3 StartY=59.25 StartZ=0 EndX=34.2901 EndY=59.25 EndZ=0
    g1: LineSegment StartX=34.98 StartY=59.9399 StartZ=0 EndX=34.98 EndY=63.1957 EndZ=0
    g2: LineSegment StartX=35.7843 StartY=64 StartZ=0 EndX=53.5317 EndY=64 EndZ=0
    g3: LineSegment StartX=53.98 StartY=64.4483 StartZ=0 EndX=53.98 EndY=65.7804 EndZ=0
    g4: LineSegment StartX=54.4496 StartY=66.25 StartZ=0 EndX=77.5616 EndY=66.25 EndZ=0
    g5: LineSegment StartX=77.98 StartY=65.8316 StartZ=0 EndX=77.98 EndY=64.3517 EndZ=0
    g6: LineSegment StartX=78.3317 StartY=64 StartZ=0 EndX=96.3966 EndY=64 EndZ=0
    g7: LineSegment StartX=96.98 StartY=63.4166 StartZ=0 EndX=96.98 EndY=61.9688 EndZ=0
    g8: LineSegment StartX=97.1988 StartY=61.75 StartZ=0 EndX=115.529 EndY=61.75 EndZ=0
    g9: LineSegment StartX=115.98 StartY=61.2993 StartZ=0 EndX=115.98 EndY=59.8538 EndZ=0
    g10: LineSegment StartX=116.334 StartY=59.5 StartZ=0 EndX=136.112 EndY=59.5 EndZ=0
    g11: LineSegment StartX=136.73 StartY=58.8821 StartZ=0 EndX=136.73 EndY=-4.96388 EndZ=0
    g12: LineSegment StartX=136.73 StartY=-4.96388 StartZ=0 EndX=121.154 EndY=-32.0193 EndZ=0
    g13: LineSegment StartX=119.981 StartY=-32.3337 StartZ=0 EndX=102.946 EndY=-22.4786 EndZ=0
    g14: LineSegment StartX=102.946 StartY=-22.4786 StartZ=0 EndX=64.7598 EndY=-17.5123 EndZ=0
    g15: LineSegment StartX=64.7598 StartY=-17.5123 StartZ=0 EndX=54.1734 EndY=-3 EndZ=0
    g16: LineSegment StartX=54.1734 StartY=-3 StartZ=0 EndX=-2.2752 EndY=-3 EndZ=0
    g17: LineSegment StartX=-3 StartY=-2.2752 StartZ=0 EndX=-3 EndY=59.25 EndZ=0
    g18: LineSegment StartX=18.674 StartY=56.25 StartZ=0 EndX=18.674 EndY=59.25 EndZ=0
    g19: LineSegment StartX=47.3598 StartY=61 StartZ=0 EndX=47.3598 EndY=64 EndZ=0
    g20: LineSegment StartX=65.8007 StartY=63.25 StartZ=0 EndX=65.8007 EndY=66.25 EndZ=0
    g21: LineSegment StartX=128.098 StartY=-13.9439 StartZ=0 EndX=130.698 EndY=-15.4407 EndZ=0
    g22: LineSegment StartX=90.2517 StartY=-17.8024 StartZ=0 EndX=89.8648 EndY=-20.7774 EndZ=0
    g23: LineSegment StartX=62.9864 StartY=-9.99077 StartZ=0 EndX=60.5627 EndY=-11.7588 EndZ=0
    g24: LineSegment StartX=27.8823 StartY=0 StartZ=0 EndX=27.8823 EndY=-3 EndZ=0
    g25: LineSegment StartX=0 StartY=28.1957 StartZ=0 EndX=-3 EndY=28.1957 EndZ=0
    g26: ArcOfCircle CenterX=34.2901 CenterY=59.9399 CenterZ=0 NormalX=0 NormalY=0 NormalZ=1 AngleXU=0 Radius=0.689901 StartAngle=4.71239 EndAngle=6.28319
    g27: ArcOfCircle CenterX=35.7843 CenterY=63.1957 CenterZ=0 NormalX=0 NormalY=0 NormalZ=1 AngleXU=0 Radius=0.804272 StartAngle=1.5708 EndAngle=3.14159
    g28: ArcOfCircle CenterX=53.5317 CenterY=64.4483 CenterZ=0 NormalX=0 NormalY=0 NormalZ=1 AngleXU=0 Radius=0.448303 StartAngle=4.71239 EndAngle=6.28319
    g29: ArcOfCircle CenterX=54.4496 CenterY=65.7804 CenterZ=0 NormalX=0 NormalY=0 NormalZ=1 AngleXU=0 Radius=0.469571 StartAngle=1.5708 EndAngle=3.14159
    g30: ArcOfCircle CenterX=77.5616 CenterY=65.8316 CenterZ=0 NormalX=0 NormalY=0 NormalZ=1 AngleXU=0 Radius=0.418401 StartAngle=0 EndAngle=1.5708
    g31: ArcOfCircle CenterX=78.3317 CenterY=64.3517 CenterZ=0 NormalX=0 NormalY=0 NormalZ=1 AngleXU=0 Radius=0.3517 StartAngle=3.14159 EndAngle=4.71239
    g32: ArcOfCircle CenterX=96.3966 CenterY=63.4166 CenterZ=0 NormalX=0 NormalY=0 NormalZ=1 AngleXU=0 Radius=0.583444 StartAngle=0 EndAngle=1.5708
    g33: ArcOfCircle CenterX=97.1988 CenterY=61.9688 CenterZ=0 NormalX=0 NormalY=0 NormalZ=1 AngleXU=0 Radius=0.218754 StartAngle=3.14159 EndAngle=4.71239
    g34: ArcOfCircle CenterX=115.529 CenterY=61.2993 CenterZ=0 NormalX=0 NormalY=0 NormalZ=1 AngleXU=0 Radius=0.450718 StartAngle=0 EndAngle=1.5708
    g35: ArcOfCircle CenterX=116.334 CenterY=59.8538 CenterZ=0 NormalX=0 NormalY=0 NormalZ=1 AngleXU=0 Radius=0.353806 StartAngle=3.14159 EndAngle=4.71239
    g36: ArcOfCircle CenterX=136.112 CenterY=58.8821 CenterZ=0 NormalX=0 NormalY=0 NormalZ=1 AngleXU=0 Radius=0.617924 StartAngle=-9e-16 EndAngle=1.5708
    g37: ArcOfCircle CenterX=120.41 CenterY=-31.5915 CenterZ=0 NormalX=0 NormalY=0 NormalZ=1 AngleXU=0 Radius=0.857438 StartAngle=4.18792 EndAngle=5.76081
    g38: ArcOfCircle CenterX=-2.2752 CenterY=-2.2752 CenterZ=0 NormalX=0 NormalY=0 NormalZ=1 AngleXU=0 Radius=0.7248 StartAngle=3.14159 EndAngle=4.71239
  constraints (91):
    c: Horizontal(g0)
    c: Vertical(g1)
    c: Horizontal(g2)
    c: Vertical(g3)
    c: Horizontal(g4)
    c: Vertical(g5)
    c: Horizontal(g6)
    c: Vertical(g7)
    c: Horizontal(g8)
    c: Vertical(g9)
    c: Horizontal(g10)
    c: Vertical(g11)
    c: Coincident(g11,g12)
    c: Coincident(g13,g14)
    c: Coincident(g14,g15)
    c: Coincident(g15,g16)
    c: Horizontal(g16)
    c: Coincident(g17,g0)
    c: Vertical(g17)
    c: PointOnObject(g18,g-3)
    c: PointOnObject(g18,g0)
    c: Vertical(g18)
    c: Distance(g18) = 3
    c: PointOnObject(g19,g-5)
    c: PointOnObject(g19,g2)
    c: Vertical(g19)
    c: Distance(g-4,g1) = 3
    c: Distance(g-6,g3) = 3
    c: Distance(g19) = 3
    c: PointOnObject(g20,g-7)
    c: PointOnObject(g20,g4)
    c: Perpendicular(g20,g-7)
    c: Distance(g20) = 3
    c: Distance(g-8,g5) = 3
    c: Distance(g-9,g6) = 3
    c: Distance(g-11,g8) = 3
    c: Distance(g-10,g7) = 3
    c: Distance(g-12,g9) = 3
    c: Distance(g-13,g10) = 3
    c: Distance(g-14,g11) = 3
    c: PointOnObject(g21,g-15)
    c: PointOnObject(g21,g12)
    c: Perpendicular(g-15,g21)
    c: Parallel(g12,g-15)
    c: Distance(g21) = 3
    c: Parallel(g13,g-16)
    c: Distance(g-16,g13) = 3
    c: PointOnObject(g22,g-17)
    c: PointOnObject(g22,g14)
    c: Perpendicular(g-17,g22)
    c: Distance(g22) = 3
    c: PointOnObject(g23,g-18)
    c: PointOnObject(g23,g15)
    c: Perpendicular(g-18,g23)
    c: Distance(g23) = 3
    c: Parallel(g15,g-18)
    c: PointOnObject(g24,g-19)
    c: PointOnObject(g24,g16)
    c: Perpendicular(g-19,g24)
    c: Distance(g24) = 3
    c: PointOnObject(g25,g-20)
    c: PointOnObject(g25,g17)
    c: Perpendicular(g-20,g25)
    c: Distance(g25) = 3
    c: Tangent(g1,g26) = -1.5708
    c: Tangent(g0,g26) = -1.5708
    c: Tangent(g2,g27) = 1.5708
    c: Tangent(g1,g27) = 1.5708
    c: Tangent(g3,g28) = -1.5708
    c: Tangent(g2,g28) = -1.5708
    c: Tangent(g3,g29) = 1.5708
    c: Tangent(g4,g29) = 1.5708
    c: Tangent(g4,g30) = 1.5708
    c: Tangent(g5,g30) = 1.5708
    c: Tangent(g5,g31) = -1.5708
    c: Tangent(g6,g31) = -1.5708
    c: Tangent(g6,g32) = 1.5708
    c: Tangent(g7,g32) = 1.5708
    c: Tangent(g7,g33) = -1.5708
    c: Tangent(g8,g33) = -1.5708
    c: Tangent(g8,g34) = 1.5708
    c: Tangent(g9,g34) = 1.5708
    c: Tangent(g9,g35) = -1.5708
    c: Tangent(g10,g35) = -1.5708
    c: Tangent(g10,g36) = 1.5708
    c: Tangent(g11,g36) = 1.5708
    c: Tangent(g12,g37) = 1.5708
    c: Tangent(g13,g37) = 1.5708
    c: Tangent(g17,g38) = 1.5708
    c: Tangent(g16,g38) = 1.5708
    c: Parallel(g14,g-17)
FEATURE [Sketcher::SketchObject] Sketch057  label="Case.InnerBorders001"
  ExternalGeometry = -> [MirroredSketch003]
  FullyConstrained = false
  expr: Constraints[23] = Spreadsheet.PCBInnerBorderSpacing
  expr: Constraints[27] = Spreadsheet.PCBInnerBorderSpacing
  expr: Constraints[57] = Spreadsheet.PCBInnerBorderSpacing
  expr: Constraints[61] = Spreadsheet.PCBInnerBorderSpacing
  expr: Constraints[65] = Spreadsheet.PCBInnerBorderSpacing
  expr: Constraints[66] = Spreadsheet.PCBInnerBorderSpacing
  expr: Constraints[67] = Spreadsheet.PCBInnerBorderSpacing
  expr: Constraints[68] = Spreadsheet.PCBInnerBorderSpacing
  expr: Constraints[69] = Spreadsheet.PCBInnerBorderSpacing
  expr: Constraints[70] = Spreadsheet.PCBInnerBorderSpacing
  expr: Constraints[71] = Spreadsheet.PCBInnerBorderSpacing
  expr: Constraints[72] = Spreadsheet.PCBInnerBorderSpacing
  expr: Constraints[73] = Spreadsheet.PCBInnerBorderSpacing
  expr: Constraints[74] = Spreadsheet.PCBInnerBorderSpacing
  expr: Constraints[79] = Spreadsheet.PCBInnerBorderSpacing
  expr: Constraints[84] = Spreadsheet.PCBInnerBorderSpacing
  expr: Constraints[89] = Spreadsheet.PCBInnerBorderSpacing
  sketch-geometry (47):
    g0: LineSegment StartX=-1 StartY=57.25 StartZ=0 EndX=36.2169 EndY=57.25 EndZ=0
    g1: LineSegment StartX=36.98 StartY=58.0131 StartZ=0 EndX=36.98 EndY=61.4175 EndZ=0
    g2: LineSegment StartX=37.5625 StartY=62 StartZ=0 EndX=55.4164 EndY=62 EndZ=0
    g3: LineSegment StartX=55.98 StartY=62.5636 StartZ=0 EndX=55.98 EndY=63.7531 EndZ=0
    g4: LineSegment StartX=56.4769 StartY=64.25 StartZ=0 EndX=75.4511 EndY=64.25 EndZ=0
    g5: LineSegment StartX=75.98 StartY=63.7211 StartZ=0 EndX=75.98 EndY=62.4917 EndZ=0
    g6: LineSegment StartX=76.4717 StartY=62 StartZ=0 EndX=94.3924 EndY=62 EndZ=0
    g7: LineSegment StartX=94.98 StartY=61.4124 StartZ=0 EndX=94.98 EndY=60.1933 EndZ=0
    g8: LineSegment StartX=95.4233 StartY=59.75 StartZ=0 EndX=113.447 EndY=59.75 EndZ=0
    g9: LineSegment StartX=113.98 StartY=59.2166 StartZ=0 EndX=113.98 EndY=57.5 EndZ=0
    g10: LineSegment StartX=113.98 StartY=57.5 StartZ=0 EndX=134.174 EndY=57.5 EndZ=0
    g11: LineSegment StartX=134.73 StartY=56.9441 StartZ=0 EndX=134.73 EndY=-4.32052 EndZ=0
    g12: LineSegment StartX=134.73 StartY=-4.32052 StartZ=0 EndX=120.755 EndY=-28.8693 EndZ=0
    g13: LineSegment StartX=118.869 StartY=-29.3799 StartZ=0 EndX=103.751 EndY=-20.634 EndZ=0
    g14: LineSegment StartX=103.751 StartY=-20.634 StartZ=0 EndX=65.9238 EndY=-15.7144 EndZ=0
    g15: LineSegment StartX=65.9238 StartY=-15.7144 StartZ=0 EndX=55.19 EndY=-1 EndZ=0
    g16: LineSegment StartX=55.19 StartY=-1 StartZ=0 EndX=-0.150389 EndY=-1 EndZ=0
    g17: LineSegment StartX=-1 StartY=-0.150389 StartZ=0 EndX=-1 EndY=57.25 EndZ=0
    g18: LineSegment StartX=47.1972 StartY=61 StartZ=0 EndX=47.1972 EndY=62 EndZ=0
    g19: LineSegment StartX=55.98 StartY=62.2587 StartZ=0 EndX=56.98 EndY=62.2587 EndZ=0
    g20: LineSegment StartX=64.3475 StartY=63.25 StartZ=0 EndX=64.3475 EndY=64.25 EndZ=0
    g21: LineSegment StartX=74.98 StartY=62.1974 StartZ=0 EndX=75.98 EndY=62.1974 EndZ=0
    g22: LineSegment StartX=85.2009 StartY=61 StartZ=0 EndX=85.2009 EndY=62 EndZ=0
    g23: LineSegment StartX=93.98 StartY=59.926 StartZ=0 EndX=94.98 EndY=59.926 EndZ=0
    g24: LineSegment StartX=103.763 StartY=58.75 StartZ=0 EndX=103.763 EndY=59.75 EndZ=0
    g25: LineSegment StartX=112.98 StartY=57.625 StartZ=0 EndX=113.98 EndY=57.625 EndZ=0
    g26: LineSegment StartX=123.843 StartY=56.5 StartZ=0 EndX=123.843 EndY=57.5 EndZ=0
    g27: LineSegment StartX=133.73 StartY=50.7739 StartZ=0 EndX=134.73 EndY=50.7739 EndZ=0
    g28: LineSegment StartX=128.328 StartY=-13.5448 StartZ=0 EndX=129.195 EndY=-14.0438 EndZ=0
    g29: LineSegment StartX=37.98 StartY=58.625 StartZ=0 EndX=36.98 EndY=58.625 EndZ=0
    g30: LineSegment StartX=10.6909 StartY=56.25 StartZ=0 EndX=10.6909 EndY=57.25 EndZ=0
    g31: LineSegment StartX=0 StartY=10.9273 StartZ=0 EndX=-1 EndY=10.9273 EndZ=0
    g32: LineSegment StartX=108.97 StartY=-22.4975 StartZ=0 EndX=108.469 EndY=-23.3631 EndZ=0
    g33: LineSegment StartX=62.8938 StartY=-9.86382 StartZ=0 EndX=62.0859 EndY=-10.4532 EndZ=0
    g34: LineSegment StartX=45.3197 StartY=-1 StartZ=0 EndX=45.3197 EndY=0 EndZ=0
    g35: ArcOfCircle CenterX=37.5625 CenterY=61.4175 CenterZ=0 NormalX=0 NormalY=0 NormalZ=1 AngleXU=0 Radius=0.582459 StartAngle=1.5708 EndAngle=3.14159
    g36: ArcOfCircle CenterX=55.4164 CenterY=62.5636 CenterZ=0 NormalX=0 NormalY=0 NormalZ=1 AngleXU=0 Radius=0.563591 StartAngle=4.71239 EndAngle=6.28319
    g37: ArcOfCircle CenterX=56.4769 CenterY=63.7531 CenterZ=0 NormalX=0 NormalY=0 NormalZ=1 AngleXU=0 Radius=0.496936 StartAngle=1.5708 EndAngle=3.14159
    g38: ArcOfCircle CenterX=75.4511 CenterY=63.7211 CenterZ=0 NormalX=0 NormalY=0 NormalZ=1 AngleXU=0 Radius=0.528895 StartAngle=0 EndAngle=1.5708
    g39: ArcOfCircle CenterX=76.4717 CenterY=62.4917 CenterZ=0 NormalX=0 NormalY=0 NormalZ=1 AngleXU=0 Radius=0.491748 StartAngle=3.14159 EndAngle=4.71239
    g40: ArcOfCircle CenterX=94.3924 CenterY=61.4124 CenterZ=0 NormalX=0 NormalY=0 NormalZ=1 AngleXU=0 Radius=0.587645 StartAngle=0 EndAngle=1.5708
    g41: ArcOfCircle CenterX=95.4233 CenterY=60.1933 CenterZ=0 NormalX=0 NormalY=0 NormalZ=1 AngleXU=0 Radius=0.443253 StartAngle=3.14159 EndAngle=4.71239
    g42: ArcOfCircle CenterX=113.447 CenterY=59.2166 CenterZ=0 NormalX=0 NormalY=0 NormalZ=1 AngleXU=0 Radius=0.533416 StartAngle=0 EndAngle=1.5708
    g43: ArcOfCircle CenterX=134.174 CenterY=56.9441 CenterZ=0 NormalX=0 NormalY=0 NormalZ=1 AngleXU=0 Radius=0.555946 StartAngle=0 EndAngle=1.5708
    g44: ArcOfCircle CenterX=119.558 CenterY=-28.1883 CenterZ=0 NormalX=0 NormalY=0 NormalZ=1 AngleXU=0 Radius=1.37659 StartAngle=4.18792 EndAngle=5.76566
    g45: ArcOfCircle CenterX=-0.150389 CenterY=-0.150389 CenterZ=0 NormalX=0 NormalY=0 NormalZ=1 AngleXU=0 Radius=0.849611 StartAngle=3.14159 EndAngle=4.71239
    g46: ArcOfCircle CenterX=36.2169 CenterY=58.0131 CenterZ=0 NormalX=0 NormalY=0 NormalZ=1 AngleXU=0 Radius=0.763133 StartAngle=4.71239 EndAngle=6.28319
  constraints (115):
    c: Horizontal(g0)
    c: Vertical(g1)
    c: Horizontal(g2)
    c: Vertical(g3)
    c: Horizontal(g4)
    c: Horizontal(g6)
    c: Vertical(g7)
    c: Horizontal(g8)
    c: Vertical(g9)
    c: Coincident(g9,g10)
    c: Horizontal(g10)
    c: Vertical(g11)
    c: Coincident(g11,g12)
    c: Coincident(g13,g14)
    c: Coincident(g14,g15)
    c: Coincident(g15,g16)
    c: Horizontal(g16)
    c: Coincident(g17,g0)
    c: Vertical(g17)
    c: Vertical(g5)
    c: PointOnObject(g18,g-8)
    c: PointOnObject(g18,g2)
    c: Perpendicular(g18,g-8)
    c: Distance(g18) = 1
    c: PointOnObject(g19,g3)
    c: PointOnObject(g19,g-10)
    c: Horizontal(g19)
    c: Distance(g19) = 1
    c: PointOnObject(g20,g-12)
    c: PointOnObject(g20,g4)
    c: Vertical(g20)
    c: PointOnObject(g21,g-14)
    c: PointOnObject(g21,g5)
    c: Horizontal(g21)
    c: PointOnObject(g22,g-16)
    c: PointOnObject(g22,g6)
    c: Perpendicular(g22,g-16)
    c: PointOnObject(g23,g-18)
    c: PointOnObject(g23,g7)
    c: Horizontal(g23)
    c: PointOnObject(g24,g-20)
    c: PointOnObject(g24,g8)
    c: Perpendicular(g-20,g24)
    c: PointOnObject(g25,g-22)
    c: PointOnObject(g25,g9)
    c: Horizontal(g25)
    c: PointOnObject(g26,g-24)
    c: PointOnObject(g26,g10)
    c: Perpendicular(g26,g-24)
    c: PointOnObject(g27,g-26)
    c: PointOnObject(g27,g11)
    c: Horizontal(g27)
    c: PointOnObject(g28,g-27)
    c: PointOnObject(g28,g12)
    c: PointOnObject(g29,g-6)
    c: PointOnObject(g29,g1)
    c: Horizontal(g29)
    c: Distance(g29) = 1
    c: PointOnObject(g30,g-3)
    c: PointOnObject(g30,g0)
    c: Vertical(g30)
    c: Distance(g30) = 1
    c: PointOnObject(g31,g-4)
    c: PointOnObject(g31,g17)
    c: Horizontal(g31)
    c: Distance(g31) = 1
    c: Distance(g20) = 1
    c: Distance(g21) = 1
    c: Distance(g22) = 1
    c: Distance(g23) = 1
    c: Distance(g24) = 1
    c: Distance(g25) = 1
    c: Distance(g26) = 1
    c: Distance(g27) = 1
    c: Distance(g28) = 1
    c: Perpendicular(g28,g-27)
    c: PointOnObject(g32,g-29)
    c: PointOnObject(g32,g13)
    c: Parallel(g13,g-29)
    c: Distance(g32) = 1
    c: Perpendicular(g-29,g32)
    c: PointOnObject(g33,g-31)
    c: PointOnObject(g33,g15)
    c: Perpendicular(g-31,g33)
    c: Distance(g33) = 1
    c: Parallel(g15,g-31)
    c: PointOnObject(g34,g16)
    c: PointOnObject(g34,g-32)
    c: Vertical(g34)
    c: Distance(g34) = 1
    c: Tangent(g2,g35) = 1.5708
    c: Tangent(g1,g35) = 1.5708
    c: Tangent(g3,g36) = -1.5708
    c: Tangent(g2,g36) = -1.5708
    c: Tangent(g4,g37) = 1.5708
    c: Tangent(g3,g37) = 1.5708
    c: Tangent(g4,g38) = 1.5708
    c: Tangent(g5,g38) = 1.5708
    c: Tangent(g6,g39) = -1.5708
    c: Tangent(g5,g39) = -1.5708
    c: Tangent(g6,g40) = 1.5708
    c: Tangent(g7,g40) = 1.5708
    c: Tangent(g8,g41) = -1.5708
    c: Tangent(g7,g41) = -1.5708
    c: Tangent(g8,g42) = 1.5708
    c: Tangent(g9,g42) = 1.5708
    c: Tangent(g10,g43) = 1.5708
    c: Tangent(g11,g43) = 1.5708
    c: Tangent(g13,g44) = 1.5708
    c: Tangent(g12,g44) = 1.5708
    c: Tangent(g17,g45) = 1.5708
    c: Tangent(g16,g45) = 1.5708
    c: Tangent(g0,g46) = -1.5708
    c: Tangent(g1,g46) = -1.5708
    c: Parallel(g14,g-30)
FEATURE [Sketcher::SketchObject] Sketch058  label="Case.TopBorder"
  AttachmentSupport = -> [Pad]
  FullyConstrained = false
  MapMode = 5
  Placement = pos=(0,0,8) rot=(0,0,1;0rad)
  sketch-geometry (86):
    g0: LineSegment StartX=-3 StartY=59.25 StartZ=0 EndX=34.2901 EndY=59.25 EndZ=0
    g1: LineSegment StartX=34.98 StartY=59.9399 StartZ=0 EndX=34.98 EndY=63.1957 EndZ=0
    g2: LineSegment StartX=35.7843 StartY=64 StartZ=0 EndX=53.5317 EndY=64 EndZ=0
    g3: LineSegment StartX=53.98 StartY=64.4483 StartZ=0 EndX=53.98 EndY=65.7804 EndZ=0
    g4: LineSegment StartX=54.4496 StartY=66.25 StartZ=0 EndX=77.5616 EndY=66.25 EndZ=0
    g5: LineSegment StartX=77.98 StartY=65.8316 StartZ=0 EndX=77.98 EndY=64.3517 EndZ=0
    g6: LineSegment StartX=78.3317 StartY=64 StartZ=0 EndX=96.3966 EndY=64 EndZ=0
    g7: LineSegment StartX=96.98 StartY=63.4166 StartZ=0 EndX=96.98 EndY=61.9688 EndZ=0
    g8: LineSegment StartX=97.1988 StartY=61.75 StartZ=0 EndX=115.529 EndY=61.75 EndZ=0
    g9: LineSegment StartX=115.98 StartY=61.2993 StartZ=0 EndX=115.98 EndY=59.8538 EndZ=0
    g10: LineSegment StartX=116.334 StartY=59.5 StartZ=0 EndX=136.112 EndY=59.5 EndZ=0
    g11: LineSegment StartX=136.73 StartY=58.8821 StartZ=0 EndX=136.73 EndY=-4.96388 EndZ=0
    g12: LineSegment StartX=136.73 StartY=-4.96388 StartZ=0 EndX=121.154 EndY=-32.0193 EndZ=0
    g13: LineSegment StartX=119.981 StartY=-32.3337 StartZ=0 EndX=102.946 EndY=-22.4786 EndZ=0
    g14: LineSegment StartX=102.946 StartY=-22.4786 StartZ=0 EndX=64.7598 EndY=-17.5123 EndZ=0
    g15: LineSegment StartX=64.7598 StartY=-17.5123 StartZ=0 EndX=54.1734 EndY=-3 EndZ=0
    g16: LineSegment StartX=54.1734 StartY=-3 StartZ=0 EndX=-2.2752 EndY=-3 EndZ=0
    g17: LineSegment StartX=-3 StartY=-2.2752 StartZ=0 EndX=-3 EndY=59.25 EndZ=0
    g18: LineSegment StartX=18.674 StartY=56.25 StartZ=0 EndX=18.674 EndY=59.25 EndZ=0
    g19: LineSegment StartX=47.3598 StartY=61 StartZ=0 EndX=47.3598 EndY=64 EndZ=0
    g20: LineSegment StartX=65.8007 StartY=63.25 StartZ=0 EndX=65.8007 EndY=66.25 EndZ=0
    g21: LineSegment StartX=128.098 StartY=-13.9439 StartZ=0 EndX=130.698 EndY=-15.4407 EndZ=0
    g22: LineSegment StartX=90.2517 StartY=-17.8024 StartZ=0 EndX=89.8648 EndY=-20.7774 EndZ=0
    g23: LineSegment StartX=62.9864 StartY=-9.99077 StartZ=0 EndX=60.5627 EndY=-11.7588 EndZ=0
    g24: LineSegment StartX=27.8823 StartY=0 StartZ=0 EndX=27.8823 EndY=-3 EndZ=0
    g25: LineSegment StartX=0 StartY=28.1957 StartZ=0 EndX=-3 EndY=28.1957 EndZ=0
    g26: ArcOfCircle CenterX=34.2901 CenterY=59.9399 CenterZ=0 NormalX=0 NormalY=0 NormalZ=1 AngleXU=0 Radius=0.689901 StartAngle=4.71239 EndAngle=6.28319
    g27: ArcOfCircle CenterX=35.7843 CenterY=63.1957 CenterZ=0 NormalX=0 NormalY=0 NormalZ=1 AngleXU=0 Radius=0.804272 StartAngle=1.5708 EndAngle=3.14159
    g28: ArcOfCircle CenterX=53.5317 CenterY=64.4483 CenterZ=0 NormalX=0 NormalY=0 NormalZ=1 AngleXU=0 Radius=0.448303 StartAngle=4.71239 EndAngle=6.28319
    g29: ArcOfCircle CenterX=54.4496 CenterY=65.7804 CenterZ=0 NormalX=0 NormalY=0 NormalZ=1 AngleXU=0 Radius=0.469571 StartAngle=1.5708 EndAngle=3.14159
    g30: ArcOfCircle CenterX=77.5616 CenterY=65.8316 CenterZ=0 NormalX=0 NormalY=0 NormalZ=1 AngleXU=0 Radius=0.418401 StartAngle=0 EndAngle=1.5708
    g31: ArcOfCircle CenterX=78.3317 CenterY=64.3517 CenterZ=0 NormalX=0 NormalY=0 NormalZ=1 AngleXU=0 Radius=0.3517 StartAngle=3.14159 EndAngle=4.71239
    g32: ArcOfCircle CenterX=96.3966 CenterY=63.4166 CenterZ=0 NormalX=0 NormalY=0 NormalZ=1 AngleXU=0 Radius=0.583444 StartAngle=0 EndAngle=1.5708
    g33: ArcOfCircle CenterX=97.1988 CenterY=61.9688 CenterZ=0 NormalX=0 NormalY=0 NormalZ=1 AngleXU=0 Radius=0.218754 StartAngle=3.14159 EndAngle=4.71239
    g34: ArcOfCircle CenterX=115.529 CenterY=61.2993 CenterZ=0 NormalX=0 NormalY=0 NormalZ=1 AngleXU=0 Radius=0.450718 StartAngle=0 EndAngle=1.5708
    g35: ArcOfCircle CenterX=116.334 CenterY=59.8538 CenterZ=0 NormalX=0 NormalY=0 NormalZ=1 AngleXU=0 Radius=0.353806 StartAngle=3.14159 EndAngle=4.71239
    g36: ArcOfCircle CenterX=136.112 CenterY=58.8821 CenterZ=0 NormalX=0 NormalY=0 NormalZ=1 AngleXU=0 Radius=0.617924 StartAngle=-9e-16 EndAngle=1.5708
    g37: ArcOfCircle CenterX=120.41 CenterY=-31.5915 CenterZ=0 NormalX=0 NormalY=0 NormalZ=1 AngleXU=0 Radius=0.857438 StartAngle=4.18792 EndAngle=5.76081
    g38: ArcOfCircle CenterX=-2.2752 CenterY=-2.2752 CenterZ=0 NormalX=0 NormalY=0 NormalZ=1 AngleXU=0 Radius=0.7248 StartAngle=3.14159 EndAngle=4.71239
    g39: LineSegment StartX=-1 StartY=57.25 StartZ=0 EndX=36.2169 EndY=57.25 EndZ=0
    g40: LineSegment StartX=36.98 StartY=58.0131 StartZ=0 EndX=36.98 EndY=61.4175 EndZ=0
    g41: LineSegment StartX=37.5625 StartY=62 StartZ=0 EndX=55.4164 EndY=62 EndZ=0
    g42: LineSegment StartX=55.98 StartY=62.5636 StartZ=0 EndX=55.98 EndY=63.7531 EndZ=0
    g43: LineSegment StartX=56.4769 StartY=64.25 StartZ=0 EndX=75.4511 EndY=64.25 EndZ=0
    g44: LineSegment StartX=75.98 StartY=63.7211 StartZ=0 EndX=75.98 EndY=62.4917 EndZ=0
    g45: LineSegment StartX=76.4717 StartY=62 StartZ=0 EndX=94.3924 EndY=62 EndZ=0
    g46: LineSegment StartX=94.98 StartY=61.4124 StartZ=0 EndX=94.98 EndY=60.1933 EndZ=0
    g47: LineSegment StartX=95.4233 StartY=59.75 StartZ=0 EndX=113.447 EndY=59.75 EndZ=0
    g48: LineSegment StartX=113.98 StartY=59.2166 StartZ=0 EndX=113.98 EndY=57.5 EndZ=0
    g49: LineSegment StartX=113.98 StartY=57.5 StartZ=0 EndX=134.174 EndY=57.5 EndZ=0
    g50: LineSegment StartX=134.73 StartY=56.9441 StartZ=0 EndX=134.73 EndY=-4.32052 EndZ=0
    g51: LineSegment StartX=134.73 StartY=-4.32052 StartZ=0 EndX=120.755 EndY=-28.8693 EndZ=0
    g52: LineSegment StartX=118.869 StartY=-29.3799 StartZ=0 EndX=103.751 EndY=-20.634 EndZ=0
    g53: LineSegment StartX=103.751 StartY=-20.634 StartZ=0 EndX=65.9238 EndY=-15.7144 EndZ=0
    g54: LineSegment StartX=65.9238 StartY=-15.7144 StartZ=0 EndX=55.19 EndY=-1 EndZ=0
    g55: LineSegment StartX=55.19 StartY=-1 StartZ=0 EndX=-0.150389 EndY=-1 EndZ=0
    g56: LineSegment StartX=-1 StartY=-0.150389 StartZ=0 EndX=-1 EndY=57.25 EndZ=0
    g57: LineSegment StartX=47.1972 StartY=61 StartZ=0 EndX=47.1972 EndY=62 EndZ=0
    g58: LineSegment StartX=55.98 StartY=62.2587 StartZ=0 EndX=56.98 EndY=62.2587 EndZ=0
    g59: LineSegment StartX=64.3475 StartY=63.25 StartZ=0 EndX=64.3475 EndY=64.25 EndZ=0
    g60: LineSegment StartX=74.98 StartY=62.1974 StartZ=0 EndX=75.98 EndY=62.1974 EndZ=0
    g61: LineSegment StartX=85.2009 StartY=61 StartZ=0 EndX=85.2009 EndY=62 EndZ=0
    g62: LineSegment StartX=93.98 StartY=59.926 StartZ=0 EndX=94.98 EndY=59.926 EndZ=0
    g63: LineSegment StartX=103.763 StartY=58.75 StartZ=0 EndX=103.763 EndY=59.75 EndZ=0
    g64: LineSegment StartX=112.98 StartY=57.625 StartZ=0 EndX=113.98 EndY=57.625 EndZ=0
    g65: LineSegment StartX=123.843 StartY=56.5 StartZ=0 EndX=123.843 EndY=57.5 EndZ=0
    g66: LineSegment StartX=133.73 StartY=50.7739 StartZ=0 EndX=134.73 EndY=50.7739 EndZ=0
    g67: LineSegment StartX=128.328 StartY=-13.5448 StartZ=0 EndX=129.195 EndY=-14.0438 EndZ=0
    g68: LineSegment StartX=37.98 StartY=58.625 StartZ=0 EndX=36.98 EndY=58.625 EndZ=0
    g69: LineSegment StartX=10.6909 StartY=56.25 StartZ=0 EndX=10.6909 EndY=57.25 EndZ=0
    g70: LineSegment StartX=0 StartY=10.9273 StartZ=0 EndX=-1 EndY=10.9273 EndZ=0
    g71: LineSegment StartX=108.97 StartY=-22.4975 StartZ=0 EndX=108.469 EndY=-23.3631 EndZ=0
    g72: LineSegment StartX=62.8938 StartY=-9.86382 StartZ=0 EndX=62.0859 EndY=-10.4532 EndZ=0
    g73: LineSegment StartX=45.3197 StartY=-1 StartZ=0 EndX=45.3197 EndY=0 EndZ=0
    g74: ArcOfCircle CenterX=37.5625 CenterY=61.4175 CenterZ=0 NormalX=0 NormalY=0 NormalZ=1 AngleXU=0 Radius=0.582459 StartAngle=1.5708 EndAngle=3.14159
    g75: ArcOfCircle CenterX=55.4164 CenterY=62.5636 CenterZ=0 NormalX=0 NormalY=0 NormalZ=1 AngleXU=0 Radius=0.563591 StartAngle=4.71239 EndAngle=6.28319
    g76: ArcOfCircle CenterX=56.4769 CenterY=63.7531 CenterZ=0 NormalX=0 NormalY=0 NormalZ=1 AngleXU=0 Radius=0.496936 StartAngle=1.5708 EndAngle=3.14159
    g77: ArcOfCircle CenterX=75.4511 CenterY=63.7211 CenterZ=0 NormalX=0 NormalY=0 NormalZ=1 AngleXU=0 Radius=0.528895 StartAngle=0 EndAngle=1.5708
    g78: ArcOfCircle CenterX=76.4717 CenterY=62.4917 CenterZ=0 NormalX=0 NormalY=0 NormalZ=1 AngleXU=0 Radius=0.491748 StartAngle=3.14159 EndAngle=4.71239
    g79: ArcOfCircle CenterX=94.3924 CenterY=61.4124 CenterZ=0 NormalX=0 NormalY=0 NormalZ=1 AngleXU=0 Radius=0.587645 StartAngle=0 EndAngle=1.5708
    g80: ArcOfCircle CenterX=95.4233 CenterY=60.1933 CenterZ=0 NormalX=0 NormalY=0 NormalZ=1 AngleXU=0 Radius=0.443253 StartAngle=3.14159 EndAngle=4.71239
    g81: ArcOfCircle CenterX=113.447 CenterY=59.2166 CenterZ=0 NormalX=0 NormalY=0 NormalZ=1 AngleXU=0 Radius=0.533416 StartAngle=0 EndAngle=1.5708
    g82: ArcOfCircle CenterX=134.174 CenterY=56.9441 CenterZ=0 NormalX=0 NormalY=0 NormalZ=1 AngleXU=0 Radius=0.555946 StartAngle=0 EndAngle=1.5708
    g83: ArcOfCircle CenterX=119.558 CenterY=-28.1883 CenterZ=0 NormalX=0 NormalY=0 NormalZ=1 AngleXU=0 Radius=1.37659 StartAngle=4.18792 EndAngle=5.76566
    g84: ArcOfCircle CenterX=-0.150389 CenterY=-0.150389 CenterZ=0 NormalX=0 NormalY=0 NormalZ=1 AngleXU=0 Radius=0.849611 StartAngle=3.14159 EndAngle=4.71239
    g85: ArcOfCircle CenterX=36.2169 CenterY=58.0131 CenterZ=0 NormalX=0 NormalY=0 NormalZ=1 AngleXU=0 Radius=0.763133 StartAngle=4.71239 EndAngle=6.28319
  constraints (206):
    c: Horizontal(g0)
    c: Vertical(g1)
    c: Horizontal(g2)
    c: Vertical(g3)
    c: Horizontal(g4)
    c: Vertical(g5)
    c: Horizontal(g6)
    c: Vertical(g7)
    c: Horizontal(g8)
    c: Vertical(g9)
    c: Horizontal(g10)
    c: Vertical(g11)
    c: Coincident(g11,g12)
    c: Coincident(g13,g14)
    c: Coincident(g14,g15)
    c: Coincident(g15,g16)
    c: Horizontal(g16)
    c: Coincident(g17,g0)
    c: Vertical(g17)
    c: PointOnObject(g18,g-3)
    c: PointOnObject(g18,g0)
    c: Vertical(g18)
    c: Distance(g18) = 3
    c: PointOnObject(g19,g-5)
    c: PointOnObject(g19,g2)
    c: Vertical(g19)
    c: Distance(g-4,g1) = 3
    c: Distance(g-6,g3) = 3
    c: Distance(g19) = 3
    c: PointOnObject(g20,g-7)
    c: PointOnObject(g20,g4)
    c: Perpendicular(g20,g-7)
    c: Distance(g20) = 3
    c: Distance(g-8,g5) = 3
    c: Distance(g-9,g6) = 3
    c: Distance(g-11,g8) = 3
    c: Distance(g-10,g7) = 3
    c: Distance(g-12,g9) = 3
    c: Distance(g-13,g10) = 3
    c: Distance(g-14,g11) = 3
    c: PointOnObject(g21,g-15)
    c: PointOnObject(g21,g12)
    c: Perpendicular(g-15,g21)
    c: Parallel(g12,g-15)
    c: Distance(g21) = 3
    c: Parallel(g13,g-16)
    c: Distance(g-16,g13) = 3
    c: PointOnObject(g22,g-17)
    c: PointOnObject(g22,g14)
    c: Perpendicular(g-17,g22)
    c: Distance(g22) = 3
    c: PointOnObject(g23,g-18)
    c: PointOnObject(g23,g15)
    c: Perpendicular(g-18,g23)
    c: Distance(g23) = 3
    c: Parallel(g15,g-18)
    c: PointOnObject(g24,g-19)
    c: PointOnObject(g24,g16)
    c: Perpendicular(g-19,g24)
    c: Distance(g24) = 3
    c: PointOnObject(g25,g-20)
    c: PointOnObject(g25,g17)
    c: Perpendicular(g-20,g25)
    c: Distance(g25) = 3
    c: Tangent(g1,g26) = -1.5708
    c: Tangent(g0,g26) = -1.5708
    c: Tangent(g2,g27) = 1.5708
    c: Tangent(g1,g27) = 1.5708
    c: Tangent(g3,g28) = -1.5708
    c: Tangent(g2,g28) = -1.5708
    c: Tangent(g3,g29) = 1.5708
    c: Tangent(g4,g29) = 1.5708
    c: Tangent(g4,g30) = 1.5708
    c: Tangent(g5,g30) = 1.5708
    c: Tangent(g5,g31) = -1.5708
    c: Tangent(g6,g31) = -1.5708
    c: Tangent(g6,g32) = 1.5708
    c: Tangent(g7,g32) = 1.5708
    c: Tangent(g7,g33) = -1.5708
    c: Tangent(g8,g33) = -1.5708
    c: Tangent(g8,g34) = 1.5708
    c: Tangent(g9,g34) = 1.5708
    c: Tangent(g9,g35) = -1.5708
    c: Tangent(g10,g35) = -1.5708
    c: Tangent(g10,g36) = 1.5708
    c: Tangent(g11,g36) = 1.5708
    c: Tangent(g12,g37) = 1.5708
    c: Tangent(g13,g37) = 1.5708
    c: Tangent(g17,g38) = 1.5708
    c: Tangent(g16,g38) = 1.5708
    c: Parallel(g14,g-17)
    c: Horizontal(g39)
    c: Vertical(g40)
    c: Horizontal(g41)
    c: Vertical(g42)
    c: Horizontal(g43)
    c: Horizontal(g45)
    c: Vertical(g46)
    c: Horizontal(g47)
    c: Vertical(g48)
    c: Coincident(g48,g49)
    c: Horizontal(g49)
    c: Vertical(g50)
    c: Coincident(g50,g51)
    c: Coincident(g52,g53)
    c: Coincident(g53,g54)
    c: Coincident(g54,g55)
    c: Horizontal(g55)
    c: Coincident(g56,g39)
    c: Vertical(g56)
    c: Vertical(g44)
    c: PointOnObject(g57,g31)
    c: PointOnObject(g57,g41)
    c: Perpendicular(g57,g31)
    c: Distance(g57) = 1
    c: PointOnObject(g58,g42)
    c: PointOnObject(g58,g29)
    c: Horizontal(g58)
    c: Distance(g58) = 1
    c: PointOnObject(g59,g27)
    c: PointOnObject(g59,g43)
    c: Vertical(g59)
    c: PointOnObject(g60,g25)
    c: PointOnObject(g60,g44)
    c: Horizontal(g60)
    c: PointOnObject(g61,g23)
    c: PointOnObject(g61,g45)
    c: Perpendicular(g61,g23)
    c: PointOnObject(g62,g21)
    c: PointOnObject(g62,g46)
    c: Horizontal(g62)
    c: PointOnObject(g63,g19)
    c: PointOnObject(g63,g47)
    c: Perpendicular(g19,g63)
    c: PointOnObject(g64,g17)
    c: PointOnObject(g64,g48)
    c: Horizontal(g64)
    c: PointOnObject(g65,g15)
    c: PointOnObject(g65,g49)
    c: Perpendicular(g65,g15)
    c: PointOnObject(g66,g13)
    c: PointOnObject(g66,g50)
    c: Horizontal(g66)
    c: PointOnObject(g67,g12)
    c: PointOnObject(g67,g51)
    c: PointOnObject(g68,g33)
    c: PointOnObject(g68,g40)
    c: Horizontal(g68)
    c: Distance(g68) = 1
    c: PointOnObject(g69,g36)
    c: PointOnObject(g69,g39)
    c: Vertical(g69)
    c: Distance(g69) = 1
    c: PointOnObject(g70,g35)
    c: PointOnObject(g70,g56)
    c: Horizontal(g70)
    c: Distance(g70) = 1
    c: Distance(g59) = 1
    c: Distance(g60) = 1
    c: Distance(g61) = 1
    c: Distance(g62) = 1
    c: Distance(g63) = 1
    c: Distance(g64) = 1
    c: Distance(g65) = 1
    c: Distance(g66) = 1
    c: Distance(g67) = 1
    c: Perpendicular(g67,g12)
    c: PointOnObject(g71,g10)
    c: PointOnObject(g71,g52)
    c: Parallel(g52,g10)
    c: Distance(g71) = 1
    c: Perpendicular(g10,g71)
    c: PointOnObject(g72,g8)
    c: PointOnObject(g72,g54)
    c: Perpendicular(g8,g72)
    c: Distance(g72) = 1
    c: Parallel(g54,g8)
    c: PointOnObject(g73,g55)
    c: PointOnObject(g73,g7)
    c: Vertical(g73)
    c: Distance(g73) = 1
    c: Tangent(g41,g74) = 1.5708
    c: Tangent(g40,g74) = 1.5708
    c: Tangent(g42,g75) = -1.5708
    c: Tangent(g41,g75) = -1.5708
    c: Tangent(g43,g76) = 1.5708
    c: Tangent(g42,g76) = 1.5708
    c: Tangent(g43,g77) = 1.5708
    c: Tangent(g44,g77) = 1.5708
    c: Tangent(g45,g78) = -1.5708
    c: Tangent(g44,g78) = -1.5708
    c: Tangent(g45,g79) = 1.5708
    c: Tangent(g46,g79) = 1.5708
    c: Tangent(g47,g80) = -1.5708
    c: Tangent(g46,g80) = -1.5708
    c: Tangent(g47,g81) = 1.5708
    c: Tangent(g48,g81) = 1.5708
    c: Tangent(g49,g82) = 1.5708
    c: Tangent(g50,g82) = 1.5708
    c: Tangent(g52,g83) = 1.5708
    c: Tangent(g51,g83) = 1.5708
    c: Tangent(g56,g84) = 1.5708
    c: Tangent(g55,g84) = 1.5708
    c: Tangent(g39,g85) = -1.5708
    c: Tangent(g40,g85) = -1.5708
    c: Parallel(g53,g9)
FEATURE [Sketcher::SketchObject] Sketch023  label="Case.SwitchPlatePocket"
  ExternalGeometry = -> [Sketch058]
  FullyConstrained = false
  MapMode = 5
  Placement = pos=(0,0,8) rot=(0,0,1;0rad)
  expr: .Placement.Base.z = Spreadsheet.CaseTopBottomBorderHeight + Spreadsheet.SwitchplateHeight
  sketch-geometry (115):
    g0: LineSegment StartX=68.62 StartY=1.21 StartZ=0 EndX=82.62 EndY=1.21 EndZ=0
    g1: LineSegment StartX=82.62 StartY=1.21 StartZ=0 EndX=82.62 EndY=-12.79 EndZ=0
    g2: LineSegment StartX=82.62 StartY=-12.79 StartZ=0 EndX=68.62 EndY=-12.79 EndZ=0
    g3: LineSegment StartX=68.62 StartY=-12.79 StartZ=0 EndX=68.62 EndY=1.21 EndZ=0
    g4: LineSegment StartX=91.6293 StartY=0.0893034 StartZ=0 EndX=105.156 EndY=-3.52 EndZ=0
    g5: LineSegment StartX=105.156 StartY=-3.52 StartZ=0 EndX=101.547 EndY=-17.0467 EndZ=0
    g6: LineSegment StartX=101.547 StartY=-17.0467 StartZ=0 EndX=88.02 EndY=-13.4374 EndZ=0
    g7: LineSegment StartX=88.02 StartY=-13.4374 StartZ=0 EndX=91.6293 EndY=0.0893034 EndZ=0
    g8: LineSegment StartX=116.275 StartY=-2.66 StartZ=0 EndX=128.399 EndY=-9.66 EndZ=0
    g9: LineSegment StartX=128.399 StartY=-9.66 StartZ=0 EndX=121.399 EndY=-21.7844 EndZ=0
    g10: LineSegment StartX=121.399 StartY=-21.7844 StartZ=0 EndX=109.277 EndY=-14.7856 EndZ=0
    g11: LineSegment StartX=109.277 StartY=-14.7856 StartZ=0 EndX=116.275 EndY=-2.66 EndZ=0
    g12: Circle CenterX=108.346 CenterY=-6.24282 CenterZ=0 NormalX=0 NormalY=0 NormalZ=1 AngleXU=0 Radius=1.14051
    g13: Circle CenterX=61.8361 CenterY=1.51 CenterZ=0 NormalX=0 NormalY=0 NormalZ=1 AngleXU=0 Radius=1.14411
    g14: Circle CenterX=18.6 CenterY=18.76 CenterZ=0 NormalX=0 NormalY=0 NormalZ=1 AngleXU=0 Radius=1.14013
    g15: Circle CenterX=18.6 CenterY=37.51 CenterZ=0 NormalX=0 NormalY=0 NormalZ=1 AngleXU=0 Radius=1.14152
    g16: Circle CenterX=94.6 CenterY=41.2626 CenterZ=0 NormalX=0 NormalY=0 NormalZ=1 AngleXU=0 Radius=1.14274
    g17: LineSegment StartX=2.02 StartY=54.16 StartZ=0 EndX=2.02 EndY=40.16 EndZ=0
    g18: LineSegment StartX=2.02 StartY=2.06 StartZ=0 EndX=16.02 EndY=2.06 EndZ=0
    g19: LineSegment StartX=35.07 StartY=54.16 StartZ=0 EndX=21.07 EndY=54.16 EndZ=0
    g20: LineSegment StartX=35.07 StartY=40.16 StartZ=0 EndX=21.07 EndY=40.16 EndZ=0
    g21: LineSegment StartX=35.07 StartY=16.06 StartZ=0 EndX=21.07 EndY=16.06 EndZ=0
    g22: LineSegment StartX=2.02 StartY=35.11 StartZ=0 EndX=16.02 EndY=35.11 EndZ=0
    g23: LineSegment StartX=2.02 StartY=21.11 StartZ=0 EndX=16.02 EndY=21.11 EndZ=0
    g24: LineSegment StartX=16.02 StartY=54.16 StartZ=0 EndX=16.02 EndY=40.16 EndZ=0
    g25: LineSegment StartX=21.07 StartY=2.06 StartZ=0 EndX=21.07 EndY=16.06 EndZ=0
    g26: LineSegment StartX=35.07 StartY=54.16 StartZ=0 EndX=35.07 EndY=40.16 EndZ=0
    g27: LineSegment StartX=40.12 StartY=58.97 StartZ=0 EndX=40.12 EndY=44.97 EndZ=0
    g28: LineSegment StartX=54.12 StartY=6.87 StartZ=0 EndX=54.12 EndY=20.87 EndZ=0
    g29: LineSegment StartX=59.17 StartY=61.27 StartZ=0 EndX=59.17 EndY=47.27 EndZ=0
    g30: LineSegment StartX=73.17 StartY=9.17 StartZ=0 EndX=73.17 EndY=23.17 EndZ=0
    g31: LineSegment StartX=78.22 StartY=58.87 StartZ=0 EndX=78.22 EndY=44.87 EndZ=0
    g32: LineSegment StartX=92.22 StartY=6.77 StartZ=0 EndX=92.22 EndY=20.77 EndZ=0
    g33: LineSegment StartX=97.27 StartY=56.54 StartZ=0 EndX=97.27 EndY=42.54 EndZ=0
    g34: LineSegment StartX=111.27 StartY=56.54 StartZ=0 EndX=111.27 EndY=42.54 EndZ=0
    g35: LineSegment StartX=40.12 StartY=44.97 StartZ=0 EndX=54.12 EndY=44.97 EndZ=0
    g36: LineSegment StartX=40.12 StartY=39.92 StartZ=0 EndX=54.12 EndY=39.92 EndZ=0
    g37: LineSegment StartX=40.12 StartY=6.87 StartZ=0 EndX=54.12 EndY=6.87 EndZ=0
    g38: LineSegment StartX=59.17 StartY=9.17 StartZ=0 EndX=73.17 EndY=9.17 EndZ=0
    g39: LineSegment StartX=59.17 StartY=23.17 StartZ=0 EndX=73.17 EndY=23.17 EndZ=0
    g40: LineSegment StartX=59.17 StartY=28.22 StartZ=0 EndX=73.17 EndY=28.22 EndZ=0
    g41: LineSegment StartX=59.17 StartY=42.22 StartZ=0 EndX=73.17 EndY=42.22 EndZ=0
    g42: LineSegment StartX=59.17 StartY=47.27 StartZ=0 EndX=73.17 EndY=47.27 EndZ=0
    g43: LineSegment StartX=16.02 StartY=54.16 StartZ=0 EndX=2.02 EndY=54.16 EndZ=0
    g44: LineSegment StartX=16.02 StartY=40.16 StartZ=0 EndX=2.02 EndY=40.16 EndZ=0
    g45: LineSegment StartX=21.07 StartY=21.11 StartZ=0 EndX=35.07 EndY=21.11 EndZ=0
    g46: LineSegment StartX=16.02 StartY=16.06 StartZ=0 EndX=2.02 EndY=16.06 EndZ=0
    g47: LineSegment StartX=16.02 StartY=16.06 StartZ=0 EndX=16.02 EndY=2.06 EndZ=0
    g48: LineSegment StartX=21.07 StartY=21.11 StartZ=0 EndX=21.07 EndY=35.11 EndZ=0
    g49: LineSegment StartX=21.07 StartY=40.16 StartZ=0 EndX=21.07 EndY=54.16 EndZ=0
    g50: LineSegment StartX=16.02 StartY=35.11 StartZ=0 EndX=16.02 EndY=21.11 EndZ=0
    g51: LineSegment StartX=35.07 StartY=35.11 StartZ=0 EndX=35.07 EndY=21.11 EndZ=0
    g52: LineSegment StartX=35.07 StartY=16.06 StartZ=0 EndX=35.07 EndY=2.06 EndZ=0
    g53: LineSegment StartX=54.12 StartY=44.97 StartZ=0 EndX=54.12 EndY=58.97 EndZ=0
    g54: LineSegment StartX=54.12 StartY=25.92 StartZ=0 EndX=54.12 EndY=39.92 EndZ=0
    g55: LineSegment StartX=97.27 StartY=42.54 StartZ=0 EndX=111.27 EndY=42.54 EndZ=0
    g56: LineSegment StartX=97.27 StartY=37.49 StartZ=0 EndX=111.27 EndY=37.49 EndZ=0
    g57: LineSegment StartX=97.27 StartY=23.49 StartZ=0 EndX=111.27 EndY=23.49 EndZ=0
    g58: LineSegment StartX=97.27 StartY=18.44 StartZ=0 EndX=111.27 EndY=18.44 EndZ=0
    g59: LineSegment StartX=97.27 StartY=4.44 StartZ=0 EndX=111.27 EndY=4.44 EndZ=0
    g60: LineSegment StartX=73.17 StartY=28.22 StartZ=0 EndX=73.17 EndY=42.22 EndZ=0
    g61: LineSegment StartX=78.22 StartY=44.87 StartZ=0 EndX=92.22 EndY=44.87 EndZ=0
    g62: LineSegment StartX=73.17 StartY=47.27 StartZ=0 EndX=73.17 EndY=61.27 EndZ=0
    g63: LineSegment StartX=92.22 StartY=25.82 StartZ=0 EndX=92.22 EndY=39.82 EndZ=0
    g64: LineSegment StartX=78.22 StartY=6.77 StartZ=0 EndX=92.22 EndY=6.77 EndZ=0
    g65: LineSegment StartX=78.22 StartY=20.77 StartZ=0 EndX=92.22 EndY=20.77 EndZ=0
    g66: LineSegment StartX=78.22 StartY=25.82 StartZ=0 EndX=92.22 EndY=25.82 EndZ=0
    g67: LineSegment StartX=78.22 StartY=20.77 StartZ=0 EndX=78.22 EndY=6.77 EndZ=0
    g68: LineSegment StartX=78.22 StartY=39.82 StartZ=0 EndX=92.22 EndY=39.82 EndZ=0
    g69: LineSegment StartX=59.17 StartY=42.22 StartZ=0 EndX=59.17 EndY=28.22 EndZ=0
    g70: LineSegment StartX=78.22 StartY=39.82 StartZ=0 EndX=78.22 EndY=25.82 EndZ=0
    g71: LineSegment StartX=92.22 StartY=44.87 StartZ=0 EndX=92.22 EndY=58.87 EndZ=0
    g72: LineSegment StartX=40.12 StartY=39.92 StartZ=0 EndX=40.12 EndY=25.92 EndZ=0
    g73: LineSegment StartX=40.12 StartY=20.87 StartZ=0 EndX=40.12 EndY=6.87 EndZ=0
    g74: LineSegment StartX=97.27 StartY=18.44 StartZ=0 EndX=97.27 EndY=4.44 EndZ=0
    g75: LineSegment StartX=111.27 StartY=18.44 StartZ=0 EndX=111.27 EndY=4.44 EndZ=0
    g76: LineSegment StartX=111.27 StartY=37.49 StartZ=0 EndX=111.27 EndY=23.49 EndZ=0
    g77: LineSegment StartX=97.27 StartY=37.49 StartZ=0 EndX=97.27 EndY=23.49 EndZ=0
    g78: LineSegment StartX=78.22 StartY=58.87 StartZ=0 EndX=92.22 EndY=58.87 EndZ=0
    g79: LineSegment StartX=59.17 StartY=23.17 StartZ=0 EndX=59.17 EndY=9.17 EndZ=0
    g80: LineSegment StartX=2.02 StartY=35.11 StartZ=0 EndX=2.02 EndY=21.11 EndZ=0
    g81: LineSegment StartX=2.02 StartY=16.06 StartZ=0 EndX=2.02 EndY=2.06 EndZ=0
    g82: LineSegment StartX=111.27 StartY=56.54 StartZ=0 EndX=97.27 EndY=56.54 EndZ=0
    g83: LineSegment StartX=40.12 StartY=58.97 StartZ=0 EndX=54.12 EndY=58.97 EndZ=0
    g84: LineSegment StartX=40.12 StartY=20.87 StartZ=0 EndX=54.12 EndY=20.87 EndZ=0
    g85: LineSegment StartX=21.07 StartY=2.06 StartZ=0 EndX=35.07 EndY=2.06 EndZ=0
    g86: LineSegment StartX=40.12 StartY=25.92 StartZ=0 EndX=54.12 EndY=25.92 EndZ=0
    g87: LineSegment StartX=109.277 StartY=-14.7856 StartZ=0 EndX=109.277 EndY=-18.8356 EndZ=0
    g88: LineSegment StartX=88.02 StartY=-13.4374 StartZ=0 EndX=88.02 EndY=-63.3371 EndZ=0
    g89: LineSegment StartX=101.547 StartY=-17.0467 StartZ=0 EndX=109.277 EndY=-17.0467 EndZ=0
    g90: LineSegment StartX=0.08 StartY=56.27 StartZ=0 EndX=0.08 EndY=0.01 EndZ=0
    g91: LineSegment StartX=0.08 StartY=56.27 StartZ=0 EndX=38.09 EndY=56.27 EndZ=0
    g92: LineSegment StartX=0.08 StartY=0.01 StartZ=0 EndX=55.8461 EndY=0.01 EndZ=0
    g93: LineSegment StartX=55.8461 StartY=0.01 StartZ=0 EndX=66.6118 EndY=-14.7264 EndZ=0
    g94: LineSegment StartX=66.6118 StartY=-14.7264 StartZ=0 EndX=104.029 EndY=-19.5728 EndZ=0
    g95: LineSegment StartX=104.029 StartY=-19.5728 StartZ=0 EndX=119.75 EndY=-28.6236 EndZ=0
    g96: LineSegment StartX=119.75 StartY=-28.6236 StartZ=0 EndX=133.476 EndY=-4.78248 EndZ=0
    g97: LineSegment StartX=113.11 StartY=58.5126 StartZ=0 EndX=113.11 EndY=6.94265 EndZ=0
    g98: LineSegment StartX=113.11 StartY=6.94265 StartZ=0 EndX=133.476 EndY=-4.78248 EndZ=0
    g99: LineSegment StartX=94.09 StartY=58.5126 StartZ=0 EndX=113.11 EndY=58.5126 EndZ=0
    g100: LineSegment StartX=94.09 StartY=61.0126 StartZ=0 EndX=94.09 EndY=58.5126 EndZ=0
    g101: LineSegment StartX=38.09 StartY=61.02 StartZ=0 EndX=57.08 EndY=61.02 EndZ=0
    g102: LineSegment StartX=57.08 StartY=63.26 StartZ=0 EndX=75.08 EndY=63.26 EndZ=0
    g103: LineSegment StartX=57.08 StartY=63.26 StartZ=0 EndX=57.08 EndY=61.02 EndZ=0
    g104: LineSegment StartX=75.08 StartY=61.02 StartZ=0 EndX=75.08 EndY=63.26 EndZ=0
    g105: LineSegment StartX=75.08 StartY=61.02 StartZ=0 EndX=94.09 EndY=61.0126 EndZ=0
    g106: LineSegment StartX=38.09 StartY=61.02 StartZ=0 EndX=38.09 EndY=56.27 EndZ=0
    g107: LineSegment StartX=73.17 StartY=61.27 StartZ=0 EndX=59.17 EndY=61.27 EndZ=0
    g108: LineSegment StartX=21.07 StartY=35.11 StartZ=0 EndX=35.07 EndY=35.11 EndZ=0
    g109: LineSegment StartX=114.544 StartY=22.1265 StartZ=0 EndX=114.544 EndY=57.5 EndZ=0
    g110: LineSegment StartX=115.521 StartY=21.15 StartZ=0 EndX=134.73 EndY=21.15 EndZ=0
    g111: LineSegment StartX=114.544 StartY=57.5 StartZ=0 EndX=134.174 EndY=57.5 EndZ=0
    g112: LineSegment StartX=134.73 StartY=21.15 StartZ=0 EndX=134.73 EndY=56.9444 EndZ=0
    g113: ArcOfCircle CenterX=134.174 CenterY=56.9444 CenterZ=0 NormalX=0 NormalY=0 NormalZ=1 AngleXU=0 Radius=0.555602 StartAngle=0 EndAngle=1.5708
    g114: ArcOfCircle CenterX=115.521 CenterY=22.1265 CenterZ=0 NormalX=0 NormalY=0 NormalZ=1 AngleXU=0 Radius=0.976478 StartAngle=3.14159 EndAngle=4.71239
  constraints (96):
    c: Coincident(g18,g81)
    c: Coincident(g46,g81)
    c: Coincident(g23,g80)
    c: Coincident(g22,g80)
    c: Coincident(g17,g44)
    c: Coincident(g17,g43)
    c: Coincident(g18,g47)
    c: Coincident(g46,g47)
    c: Coincident(g23,g50)
    c: Coincident(g22,g50)
    c: Coincident(g24,g44)
    c: Coincident(g24,g43)
    c: Coincident(g25,g85)
    c: Coincident(g21,g25)
    c: Coincident(g45,g48)
    c: Coincident(g48,g108)
    c: Coincident(g20,g49)
    c: Coincident(g19,g49)
    c: Coincident(g52,g85)
    c: Coincident(g21,g52)
    c: Coincident(g45,g51)
    c: Coincident(g51,g108)
    c: Coincident(g20,g26)
    c: Coincident(g19,g26)
    c: Coincident(g37,g73)
    c: Coincident(g73,g84)
    c: Coincident(g72,g86)
    c: Coincident(g36,g72)
    c: Coincident(g27,g35)
    c: Coincident(g27,g83)
    c: Coincident(g28,g37)
    c: Coincident(g28,g84)
    c: Coincident(g54,g86)
    c: Coincident(g36,g54)
    c: Coincident(g35,g53)
    c: Coincident(g53,g83)
    c: Coincident(g38,g79)
    c: Coincident(g39,g79)
    c: Coincident(g40,g69)
    c: Coincident(g41,g69)
    c: Coincident(g29,g42)
    c: Coincident(g29,g107)
    c: Coincident(g2,g3)
    c: Coincident(g0,g3)
    c: Coincident(g30,g38)
    c: Coincident(g30,g39)
    c: Coincident(g40,g60)
    c: Coincident(g41,g60)
    c: Coincident(g42,g62)
    c: Coincident(g62,g107)
    c: Coincident(g64,g67)
    c: Coincident(g65,g67)
    c: Coincident(g66,g70)
    c: Coincident(g68,g70)
    c: Coincident(g31,g61)
    c: Coincident(g31,g78)
    c: Coincident(g1,g2)
    c: Coincident(g0,g1)
    c: Coincident(g6,g7)
    c: Coincident(g4,g7)
    c: Coincident(g32,g64)
    c: Coincident(g32,g65)
    c: Coincident(g63,g66)
    c: Coincident(g63,g68)
    c: Coincident(g61,g71)
    c: Coincident(g71,g78)
    c: Coincident(g59,g74)
    c: Coincident(g58,g74)
    c: Coincident(g57,g77)
    c: Coincident(g56,g77)
    c: Coincident(g33,g55)
    c: Coincident(g33,g82)
    c: Coincident(g5,g6)
    c: Coincident(g4,g5)
    c: Coincident(g10,g11)
    c: Coincident(g59,g75)
    c: Coincident(g58,g75)
    c: Coincident(g57,g76)
    c: Coincident(g56,g76)
    c: Coincident(g34,g55)
    c: Coincident(g34,g82)
    c: Coincident(g8,g11)
    c: Coincident(g9,g10)
    c: Coincident(g8,g9)
    c: PointOnObject(g109,g-3)
    c: Vertical(g109)
    c: PointOnObject(g110,g-4)
    c: Horizontal(g110)
    c: Coincident(g111,g109)
    c: Horizontal(g111)
    c: Coincident(g112,g110)
    c: Vertical(g112)
    c: Tangent(g111,g113) = 1.5708
    c: Tangent(g112,g113) = -1.5708
    c: Tangent(g109,g114) = 1.5708
    c: Tangent(g110,g114) = -1.5708
FEATURE [PartDesign::Pocket] Pocket006  label="Case.SwitchPlate.Pocket"
  BaseFeature = -> Pad
  Direction = (0,0,-1)
  Length = 2
  Length2 = 5
  Placement = pos=(0,0,6) rot=(0,0,1;0rad)
  Profile = -> Sketch023
  ReferenceAxis = -> Sketch023 [N_Axis]
  Suppressed = false
  Type = 0
  expr: Length = Spreadsheet.SwitchplateHeight
FEATURE [Sketcher::SketchObject] Sketch059  label="Case.BottomBorders"
  AttachmentOffset = pos=(0,0,0) rot=(1,0,0;3.14159rad)
  AttachmentSupport = -> [Pad]
  FullyConstrained = false
  MapMode = 5
  Placement = pos=(0,0,6) rot=(0,0,1;0rad)
  sketch-geometry (86):
    g0: LineSegment StartX=-3 StartY=59.25 StartZ=0 EndX=34.2901 EndY=59.25 EndZ=0
    g1: LineSegment StartX=34.98 StartY=59.9399 StartZ=0 EndX=34.98 EndY=63.1957 EndZ=0
    g2: LineSegment StartX=35.7843 StartY=64 StartZ=0 EndX=53.5317 EndY=64 EndZ=0
    g3: LineSegment StartX=53.98 StartY=64.4483 StartZ=0 EndX=53.98 EndY=65.7804 EndZ=0
    g4: LineSegment StartX=54.4496 StartY=66.25 StartZ=0 EndX=77.5616 EndY=66.25 EndZ=0
    g5: LineSegment StartX=77.98 StartY=65.8316 StartZ=0 EndX=77.98 EndY=64.3517 EndZ=0
    g6: LineSegment StartX=78.3317 StartY=64 StartZ=0 EndX=96.3966 EndY=64 EndZ=0
    g7: LineSegment StartX=96.98 StartY=63.4166 StartZ=0 EndX=96.98 EndY=61.9688 EndZ=0
    g8: LineSegment StartX=97.1988 StartY=61.75 StartZ=0 EndX=115.529 EndY=61.75 EndZ=0
    g9: LineSegment StartX=115.98 StartY=61.2993 StartZ=0 EndX=115.98 EndY=59.8538 EndZ=0
    g10: LineSegment StartX=116.334 StartY=59.5 StartZ=0 EndX=136.112 EndY=59.5 EndZ=0
    g11: LineSegment StartX=136.73 StartY=58.8821 StartZ=0 EndX=136.73 EndY=-4.96388 EndZ=0
    g12: LineSegment StartX=136.73 StartY=-4.96388 StartZ=0 EndX=121.154 EndY=-32.0193 EndZ=0
    g13: LineSegment StartX=119.981 StartY=-32.3337 StartZ=0 EndX=102.946 EndY=-22.4786 EndZ=0
    g14: LineSegment StartX=102.946 StartY=-22.4786 StartZ=0 EndX=64.7598 EndY=-17.5123 EndZ=0
    g15: LineSegment StartX=64.7598 StartY=-17.5123 StartZ=0 EndX=54.1734 EndY=-3 EndZ=0
    g16: LineSegment StartX=54.1734 StartY=-3 StartZ=0 EndX=-2.2752 EndY=-3 EndZ=0
    g17: LineSegment StartX=-3 StartY=-2.2752 StartZ=0 EndX=-3 EndY=59.25 EndZ=0
    g18: LineSegment StartX=18.674 StartY=56.25 StartZ=0 EndX=18.674 EndY=59.25 EndZ=0
    g19: LineSegment StartX=47.3598 StartY=61 StartZ=0 EndX=47.3598 EndY=64 EndZ=0
    g20: LineSegment StartX=65.8007 StartY=63.25 StartZ=0 EndX=65.8007 EndY=66.25 EndZ=0
    g21: LineSegment StartX=128.098 StartY=-13.9439 StartZ=0 EndX=130.698 EndY=-15.4407 EndZ=0
    g22: LineSegment StartX=90.2517 StartY=-17.8024 StartZ=0 EndX=89.8648 EndY=-20.7774 EndZ=0
    g23: LineSegment StartX=62.9864 StartY=-9.99077 StartZ=0 EndX=60.5627 EndY=-11.7588 EndZ=0
    g24: LineSegment StartX=27.8823 StartY=0 StartZ=0 EndX=27.8823 EndY=-3 EndZ=0
    g25: LineSegment StartX=0 StartY=28.1957 StartZ=0 EndX=-3 EndY=28.1957 EndZ=0
    g26: ArcOfCircle CenterX=34.2901 CenterY=59.9399 CenterZ=0 NormalX=0 NormalY=0 NormalZ=1 AngleXU=0 Radius=0.689901 StartAngle=4.71239 EndAngle=6.28319
    g27: ArcOfCircle CenterX=35.7843 CenterY=63.1957 CenterZ=0 NormalX=0 NormalY=0 NormalZ=1 AngleXU=0 Radius=0.804272 StartAngle=1.5708 EndAngle=3.14159
    g28: ArcOfCircle CenterX=53.5317 CenterY=64.4483 CenterZ=0 NormalX=0 NormalY=0 NormalZ=1 AngleXU=0 Radius=0.448303 StartAngle=4.71239 EndAngle=6.28319
    g29: ArcOfCircle CenterX=54.4496 CenterY=65.7804 CenterZ=0 NormalX=0 NormalY=0 NormalZ=1 AngleXU=0 Radius=0.469571 StartAngle=1.5708 EndAngle=3.14159
    g30: ArcOfCircle CenterX=77.5616 CenterY=65.8316 CenterZ=0 NormalX=0 NormalY=0 NormalZ=1 AngleXU=0 Radius=0.418401 StartAngle=0 EndAngle=1.5708
    g31: ArcOfCircle CenterX=78.3317 CenterY=64.3517 CenterZ=0 NormalX=0 NormalY=0 NormalZ=1 AngleXU=0 Radius=0.3517 StartAngle=3.14159 EndAngle=4.71239
    g32: ArcOfCircle CenterX=96.3966 CenterY=63.4166 CenterZ=0 NormalX=0 NormalY=0 NormalZ=1 AngleXU=0 Radius=0.583444 StartAngle=0 EndAngle=1.5708
    g33: ArcOfCircle CenterX=97.1988 CenterY=61.9688 CenterZ=0 NormalX=0 NormalY=0 NormalZ=1 AngleXU=0 Radius=0.218754 StartAngle=3.14159 EndAngle=4.71239
    g34: ArcOfCircle CenterX=115.529 CenterY=61.2993 CenterZ=0 NormalX=0 NormalY=0 NormalZ=1 AngleXU=0 Radius=0.450718 StartAngle=0 EndAngle=1.5708
    g35: ArcOfCircle CenterX=116.334 CenterY=59.8538 CenterZ=0 NormalX=0 NormalY=0 NormalZ=1 AngleXU=0 Radius=0.353806 StartAngle=3.14159 EndAngle=4.71239
    g36: ArcOfCircle CenterX=136.112 CenterY=58.8821 CenterZ=0 NormalX=0 NormalY=0 NormalZ=1 AngleXU=0 Radius=0.617924 StartAngle=-9e-16 EndAngle=1.5708
    g37: ArcOfCircle CenterX=120.41 CenterY=-31.5915 CenterZ=0 NormalX=0 NormalY=0 NormalZ=1 AngleXU=0 Radius=0.857438 StartAngle=4.18792 EndAngle=5.76081
    g38: ArcOfCircle CenterX=-2.2752 CenterY=-2.2752 CenterZ=0 NormalX=0 NormalY=0 NormalZ=1 AngleXU=0 Radius=0.7248 StartAngle=3.14159 EndAngle=4.71239
    g39: LineSegment StartX=-1 StartY=57.25 StartZ=0 EndX=36.2169 EndY=57.25 EndZ=0
    g40: LineSegment StartX=36.98 StartY=58.0131 StartZ=0 EndX=36.98 EndY=61.4175 EndZ=0
    g41: LineSegment StartX=37.5625 StartY=62 StartZ=0 EndX=55.4164 EndY=62 EndZ=0
    g42: LineSegment StartX=55.98 StartY=62.5636 StartZ=0 EndX=55.98 EndY=63.7531 EndZ=0
    g43: LineSegment StartX=56.4769 StartY=64.25 StartZ=0 EndX=75.4511 EndY=64.25 EndZ=0
    g44: LineSegment StartX=75.98 StartY=63.7211 StartZ=0 EndX=75.98 EndY=62.4917 EndZ=0
    g45: LineSegment StartX=76.4717 StartY=62 StartZ=0 EndX=94.3924 EndY=62 EndZ=0
    g46: LineSegment StartX=94.98 StartY=61.4124 StartZ=0 EndX=94.98 EndY=60.1933 EndZ=0
    g47: LineSegment StartX=95.4233 StartY=59.75 StartZ=0 EndX=113.447 EndY=59.75 EndZ=0
    g48: LineSegment StartX=113.98 StartY=59.2166 StartZ=0 EndX=113.98 EndY=57.5 EndZ=0
    g49: LineSegment StartX=113.98 StartY=57.5 StartZ=0 EndX=134.174 EndY=57.5 EndZ=0
    g50: LineSegment StartX=134.73 StartY=56.9441 StartZ=0 EndX=134.73 EndY=-4.32052 EndZ=0
    g51: LineSegment StartX=134.73 StartY=-4.32052 StartZ=0 EndX=120.755 EndY=-28.8693 EndZ=0
    g52: LineSegment StartX=118.869 StartY=-29.3799 StartZ=0 EndX=103.751 EndY=-20.634 EndZ=0
    g53: LineSegment StartX=103.751 StartY=-20.634 StartZ=0 EndX=65.9238 EndY=-15.7144 EndZ=0
    g54: LineSegment StartX=65.9238 StartY=-15.7144 StartZ=0 EndX=55.19 EndY=-1 EndZ=0
    g55: LineSegment StartX=55.19 StartY=-1 StartZ=0 EndX=-0.150389 EndY=-1 EndZ=0
    g56: LineSegment StartX=-1 StartY=-0.150389 StartZ=0 EndX=-1 EndY=57.25 EndZ=0
    g57: LineSegment StartX=47.1972 StartY=61 StartZ=0 EndX=47.1972 EndY=62 EndZ=0
    g58: LineSegment StartX=55.98 StartY=62.2587 StartZ=0 EndX=56.98 EndY=62.2587 EndZ=0
    g59: LineSegment StartX=64.3475 StartY=63.25 StartZ=0 EndX=64.3475 EndY=64.25 EndZ=0
    g60: LineSegment StartX=74.98 StartY=62.1974 StartZ=0 EndX=75.98 EndY=62.1974 EndZ=0
    g61: LineSegment StartX=85.2009 StartY=61 StartZ=0 EndX=85.2009 EndY=62 EndZ=0
    g62: LineSegment StartX=93.98 StartY=59.926 StartZ=0 EndX=94.98 EndY=59.926 EndZ=0
    g63: LineSegment StartX=103.763 StartY=58.75 StartZ=0 EndX=103.763 EndY=59.75 EndZ=0
    g64: LineSegment StartX=112.98 StartY=57.625 StartZ=0 EndX=113.98 EndY=57.625 EndZ=0
    g65: LineSegment StartX=123.843 StartY=56.5 StartZ=0 EndX=123.843 EndY=57.5 EndZ=0
    g66: LineSegment StartX=133.73 StartY=50.7739 StartZ=0 EndX=134.73 EndY=50.7739 EndZ=0
    g67: LineSegment StartX=128.328 StartY=-13.5448 StartZ=0 EndX=129.195 EndY=-14.0438 EndZ=0
    g68: LineSegment StartX=37.98 StartY=58.625 StartZ=0 EndX=36.98 EndY=58.625 EndZ=0
    g69: LineSegment StartX=10.6909 StartY=56.25 StartZ=0 EndX=10.6909 EndY=57.25 EndZ=0
    g70: LineSegment StartX=0 StartY=10.9273 StartZ=0 EndX=-1 EndY=10.9273 EndZ=0
    g71: LineSegment StartX=108.97 StartY=-22.4975 StartZ=0 EndX=108.469 EndY=-23.3631 EndZ=0
    g72: LineSegment StartX=62.8938 StartY=-9.86382 StartZ=0 EndX=62.0859 EndY=-10.4532 EndZ=0
    g73: LineSegment StartX=45.3197 StartY=-1 StartZ=0 EndX=45.3197 EndY=0 EndZ=0
    g74: ArcOfCircle CenterX=37.5625 CenterY=61.4175 CenterZ=0 NormalX=0 NormalY=0 NormalZ=1 AngleXU=0 Radius=0.582459 StartAngle=1.5708 EndAngle=3.14159
    g75: ArcOfCircle CenterX=55.4164 CenterY=62.5636 CenterZ=0 NormalX=0 NormalY=0 NormalZ=1 AngleXU=0 Radius=0.563591 StartAngle=4.71239 EndAngle=6.28319
    g76: ArcOfCircle CenterX=56.4769 CenterY=63.7531 CenterZ=0 NormalX=0 NormalY=0 NormalZ=1 AngleXU=0 Radius=0.496936 StartAngle=1.5708 EndAngle=3.14159
    g77: ArcOfCircle CenterX=75.4511 CenterY=63.7211 CenterZ=0 NormalX=0 NormalY=0 NormalZ=1 AngleXU=0 Radius=0.528895 StartAngle=0 EndAngle=1.5708
    g78: ArcOfCircle CenterX=76.4717 CenterY=62.4917 CenterZ=0 NormalX=0 NormalY=0 NormalZ=1 AngleXU=0 Radius=0.491748 StartAngle=3.14159 EndAngle=4.71239
    g79: ArcOfCircle CenterX=94.3924 CenterY=61.4124 CenterZ=0 NormalX=0 NormalY=0 NormalZ=1 AngleXU=0 Radius=0.587645 StartAngle=0 EndAngle=1.5708
    g80: ArcOfCircle CenterX=95.4233 CenterY=60.1933 CenterZ=0 NormalX=0 NormalY=0 NormalZ=1 AngleXU=0 Radius=0.443253 StartAngle=3.14159 EndAngle=4.71239
    g81: ArcOfCircle CenterX=113.447 CenterY=59.2166 CenterZ=0 NormalX=0 NormalY=0 NormalZ=1 AngleXU=0 Radius=0.533416 StartAngle=0 EndAngle=1.5708
    g82: ArcOfCircle CenterX=134.174 CenterY=56.9441 CenterZ=0 NormalX=0 NormalY=0 NormalZ=1 AngleXU=0 Radius=0.555946 StartAngle=0 EndAngle=1.5708
    g83: ArcOfCircle CenterX=119.558 CenterY=-28.1883 CenterZ=0 NormalX=0 NormalY=0 NormalZ=1 AngleXU=0 Radius=1.37659 StartAngle=4.18792 EndAngle=5.76566
    g84: ArcOfCircle CenterX=-0.150389 CenterY=-0.150389 CenterZ=0 NormalX=0 NormalY=0 NormalZ=1 AngleXU=0 Radius=0.849611 StartAngle=3.14159 EndAngle=4.71239
    g85: ArcOfCircle CenterX=36.2169 CenterY=58.0131 CenterZ=0 NormalX=0 NormalY=0 NormalZ=1 AngleXU=0 Radius=0.763133 StartAngle=4.71239 EndAngle=6.28319
  constraints (61):
    c: Coincident(g17,g38)
    c: Coincident(g0,g17)
    c: Coincident(g16,g38)
    c: Coincident(g56,g84)
    c: Coincident(g39,g56)
    c: Coincident(g55,g84)
    c: Coincident(g0,g26)
    c: Coincident(g1,g26)
    c: Coincident(g1,g27)
    c: Coincident(g2,g27)
    c: Coincident(g39,g85)
    c: Coincident(g40,g85)
    c: Coincident(g40,g74)
    c: Coincident(g41,g74)
    c: Coincident(g2,g28)
    c: Coincident(g3,g28)
    c: Coincident(g3,g29)
    c: Coincident(g15,g16)
    c: Coincident(g4,g29)
    c: Coincident(g54,g55)
    c: Coincident(g41,g75)
    c: Coincident(g42,g75)
    c: Coincident(g42,g76)
    c: Coincident(g43,g76)
    c: Coincident(g14,g15)
    c: Coincident(g53,g54)
    c: Coincident(g43,g77)
    c: Coincident(g44,g78)
    c: Coincident(g44,g77)
    c: Coincident(g45,g78)
    c: Coincident(g4,g30)
    c: Coincident(g5,g31)
    c: Coincident(g5,g30)
    c: Coincident(g6,g31)
    c: Coincident(g45,g79)
    c: Coincident(g46,g80)
    c: Coincident(g46,g79)
    c: Coincident(g47,g80)
    c: Coincident(g6,g32)
    c: Coincident(g7,g33)
    c: Coincident(g7,g32)
    c: Coincident(g8,g33)
    c: Coincident(g13,g14)
    c: Coincident(g52,g53)
    c: Coincident(g47,g81)
    c: Coincident(g48,g49)
    c: Coincident(g48,g81)
    c: Coincident(g8,g34)
    c: Coincident(g9,g35)
    c: Coincident(g9,g34)
    c: Coincident(g10,g35)
    c: Coincident(g52,g83)
    c: Coincident(g13,g37)
    c: Coincident(g51,g83)
    c: Coincident(g12,g37)
    c: Coincident(g49,g82)
    c: Coincident(g50,g51)
    c: Coincident(g50,g82)
    c: Coincident(g10,g36)
    c: Coincident(g11,g12)
    c: Coincident(g11,g36)
FEATURE [PartDesign::Pad] Pad009  label="Case.BottomBorder.Body"
  BaseFeature = -> Pocket006
  Direction = (0,1e-16,1)
  Length = 22
  Length2 = 10
  Placement = pos=(0,0,6) rot=(0,0,1;0rad)
  Profile = -> Sketch059
  ReferenceAxis = -> Sketch059 [N_Axis]
  Reversed = true
  Suppressed = false
  Type = 0
  expr: Length = Spreadsheet.CaseTopBottomBorderHeight + Spreadsheet.CaseTopTopBorderHeight + 7 + 2
FEATURE [App::DocumentObjectGroup] Group  label="BaseSketches"
  Group = -> [MirroredSketch004,Sketch056,Sketch057]
FEATURE [Sketcher::SketchObject] Sketch077
  AttachmentSupport = -> [Pad009]
  ExternalGeometry = -> [MirroredSketch003,Pad009]
  FullyConstrained = false
  MapMode = 5
  Placement = pos=(0,0,6) rot=(1,0,0;3.14159rad)
  expr: Constraints[100] = Spreadsheet.ThreadedInsertExtDiameter
  expr: Constraints[102] = Spreadsheet.ThreadedInsertExtDiameter
  expr: Constraints[104] = Spreadsheet.ThreadedInsertExtDiameter
  expr: Constraints[98] = Spreadsheet.ThreadedInsertExtDiameter
  expr: Constraints[99] = Spreadsheet.ThreadedInsertExtDiameter
  sketch-geometry (42):
    g0: ArcOfCircle CenterX=18.61 CenterY=-37.51 CenterZ=0 NormalX=0 NormalY=0 NormalZ=1 AngleXU=0 Radius=5 StartAngle=1.05641 EndAngle=2.11531
    g1: Circle CenterX=61.84 CenterY=-1.51 CenterZ=0 NormalX=0 NormalY=0 NormalZ=1 AngleXU=0 Radius=5
    g2: ArcOfCircle CenterX=108.3 CenterY=6.24 CenterZ=0 NormalX=0 NormalY=0 NormalZ=1 AngleXU=0 Radius=5 StartAngle=3.77437 EndAngle=8.95945
    g3: ArcOfCircle CenterX=18.6 CenterY=-18.76 CenterZ=0 NormalX=0 NormalY=0 NormalZ=1 AngleXU=0 Radius=5 StartAngle=1.05411 EndAngle=2.11297
    g4: LineSegment StartX=14.1867 StartY=-21.11 StartZ=0 EndX=16.02 EndY=-21.11 EndZ=0
    g5: LineSegment StartX=16.02 StartY=-21.11 StartZ=0 EndX=16.02 EndY=-23.0429 EndZ=0
    g6: LineSegment StartX=16.02 StartY=-35.11 StartZ=0 EndX=14.2237 EndY=-35.11 EndZ=0
    g7: LineSegment StartX=21.07 StartY=-35.11 StartZ=0 EndX=22.9963 EndY=-35.11 EndZ=0
    g8: LineSegment StartX=23.0133 StartY=-21.11 StartZ=0 EndX=21.07 EndY=-21.11 EndZ=0
    g9: LineSegment StartX=21.07 StartY=-21.11 StartZ=0 EndX=21.07 EndY=-23.1073 EndZ=0
    g10: LineSegment StartX=21.07 StartY=-14.4127 StartZ=0 EndX=21.07 EndY=-16.06 EndZ=0
    g11: LineSegment StartX=21.07 StartY=-16.06 StartZ=0 EndX=22.8083 EndY=-16.06 EndZ=0
    g12: LineSegment StartX=16.02 StartY=-14.4771 StartZ=0 EndX=16.02 EndY=-16.06 EndZ=0
    g13: LineSegment StartX=16.02 StartY=-16.06 StartZ=0 EndX=14.3917 EndY=-16.06 EndZ=0
    g14: LineSegment StartX=16.02 StartY=-40.16 StartZ=0 EndX=14.37 EndY=-40.16 EndZ=0
    g15: LineSegment StartX=16.02 StartY=-41.7869 StartZ=0 EndX=16.02 EndY=-40.16 EndZ=0
    g16: LineSegment StartX=21.07 StartY=-40.16 StartZ=0 EndX=22.85 EndY=-40.16 EndZ=0
    g17: LineSegment StartX=21.07 StartY=-41.863 StartZ=0 EndX=21.07 EndY=-40.16 EndZ=0
    g18: LineSegment StartX=103.832 StartY=8.48359 StartZ=0 EndX=105.156 EndY=3.52 EndZ=0
    g19: LineSegment StartX=105.156 StartY=3.52 StartZ=0 EndX=104.268 EndY=3.28306 EndZ=0
    g20: ArcOfCircle CenterX=18.6 CenterY=-18.76 CenterZ=0 NormalX=0 NormalY=0 NormalZ=1 AngleXU=0 Radius=5 StartAngle=2.57116 EndAngle=3.63088
    g21: ArcOfCircle CenterX=18.6 CenterY=-18.76 CenterZ=0 NormalX=0 NormalY=0 NormalZ=1 AngleXU=0 Radius=5 StartAngle=4.17021 EndAngle=5.22907
    g22: ArcOfCircle CenterX=18.6 CenterY=-18.76 CenterZ=0 NormalX=0 NormalY=0 NormalZ=1 AngleXU=0 Radius=5 StartAngle=5.79389 EndAngle=6.85362
    g23: ArcOfCircle CenterX=18.61 CenterY=-37.51 CenterZ=0 NormalX=0 NormalY=0 NormalZ=1 AngleXU=0 Radius=5 StartAngle=2.64094 EndAngle=3.70019
    g24: ArcOfCircle CenterX=18.61 CenterY=-37.51 CenterZ=0 NormalX=0 NormalY=0 NormalZ=1 AngleXU=0 Radius=5 StartAngle=4.16788 EndAngle=5.22677
    g25: ArcOfCircle CenterX=18.61 CenterY=-37.51 CenterZ=0 NormalX=0 NormalY=0 NormalZ=1 AngleXU=0 Radius=5 StartAngle=5.72458 EndAngle=6.78384
    g26: LineSegment StartX=92.22 StartY=-37.782 StartZ=0 EndX=92.22 EndY=-39.82 EndZ=0
    g27: LineSegment StartX=92.22 StartY=-45.218 StartZ=0 EndX=92.22 EndY=-44.87 EndZ=0
    g28: LineSegment StartX=92.22 StartY=-44.87 StartZ=0 EndX=91.7401 EndY=-44.87 EndZ=0
    g29: ArcOfCircle CenterX=94.55 CenterY=-41.5 CenterZ=0 NormalX=0 NormalY=0 NormalZ=1 AngleXU=0 Radius=4.38774 StartAngle=2.74868 EndAngle=4.01738
    g30: ArcOfCircle CenterX=94.55 CenterY=-41.5 CenterZ=0 NormalX=0 NormalY=0 NormalZ=1 AngleXU=0 Radius=4.38774 StartAngle=6.04388 EndAngle=8.41379
    g31: ArcOfCircle CenterX=94.55 CenterY=-41.5 CenterZ=0 NormalX=0 NormalY=0 NormalZ=1 AngleXU=0 Radius=4.38774 StartAngle=4.15258 EndAngle=5.38102
    g32: LineSegment StartX=21.07 StartY=-33.157 StartZ=0 EndX=21.07 EndY=-35.11 EndZ=0
    g33: LineSegment StartX=16.02 StartY=-33.2331 StartZ=0 EndX=16.02 EndY=-35.11 EndZ=0
    g34: LineSegment StartX=90.4966 StartY=-39.82 StartZ=0 EndX=92.22 EndY=-39.82 EndZ=0
    g35: LineSegment StartX=97.27 StartY=-42.54 StartZ=0 EndX=98.8127 EndY=-42.54 EndZ=0
    g36: LineSegment StartX=97.27 StartY=-42.54 StartZ=0 EndX=97.27 EndY=-44.9429 EndZ=0
    g37: Circle CenterX=94.55 CenterY=-41.5 CenterZ=0 NormalX=0 NormalY=0 NormalZ=1 AngleXU=0 Radius=1.95
    g38: Circle CenterX=108.3 CenterY=6.24 CenterZ=0 NormalX=0 NormalY=0 NormalZ=1 AngleXU=0 Radius=1.95
    g39: Circle CenterX=61.84 CenterY=-1.51 CenterZ=0 NormalX=0 NormalY=0 NormalZ=1 AngleXU=0 Radius=1.95
    g40: Circle CenterX=18.6 CenterY=-18.76 CenterZ=0 NormalX=0 NormalY=0 NormalZ=1 AngleXU=0 Radius=1.95
    g41: Circle CenterX=18.61 CenterY=-37.51 CenterZ=0 NormalX=0 NormalY=0 NormalZ=1 AngleXU=0 Radius=1.95
  constraints (105):
    c: Coincident(g0,g-4)
    c: Coincident(g1,g-7)
    c: Coincident(g3,g-3)
    c: Diameter(g3) = 10
    c: Diameter(g0) = 10
    c: Diameter(g1) = 10
    c: Coincident(g4,g5)
    c: Coincident(g33,g6)
    c: Horizontal(g4)
    c: Horizontal(g6)
    c: Vertical(g5)
    c: Coincident(g33,g-14)
    c: Coincident(g8,g9)
    c: Coincident(g32,g7)
    c: Horizontal(g7)
    c: Horizontal(g8)
    c: Vertical(g9)
    c: Coincident(g7,g-33)
    c: Coincident(g10,g11)
    c: Horizontal(g11)
    c: Vertical(g10)
    c: Coincident(g10,g-9)
    c: Coincident(g12,g13)
    c: Horizontal(g13)
    c: Vertical(g12)
    c: Coincident(g12,g-11)
    c: Coincident(g15,g14)
    c: Horizontal(g14)
    c: Vertical(g15)
    c: Coincident(g14,g-19)
    c: Coincident(g17,g16)
    c: Horizontal(g16)
    c: Vertical(g17)
    c: Coincident(g16,g-18)
    c: Coincident(g18,g-50)
    c: Coincident(g18,g19)
    c: PointOnObject(g3,g-8)
    c: Equal(g3,g20)
    c: Coincident(g3,g20)
    c: Equal(g20,g21)
    c: Coincident(g20,g21)
    c: Equal(g21,g22)
    c: PointOnObject(g21,g-13)
    c: PointOnObject(g22,g-30)
    c: Coincident(g21,g22)
    c: PointOnObject(g0,g-13)
    c: Equal(g0,g23)
    c: Coincident(g0,g23)
    c: Equal(g23,g24)
    c: PointOnObject(g23,g-16)
    c: PointOnObject(g24,g-19)
    c: Coincident(g23,g24)
    c: Equal(g24,g25)
    c: PointOnObject(g24,g-18)
    c: PointOnObject(g25,g-17)
    c: Coincident(g24,g25)
    c: Vertical(g26)
    c: Coincident(g26,g-25)
    c: Coincident(g27,g28)
    c: Horizontal(g28)
    c: Vertical(g27)
    c: Coincident(g27,g-23)
    c: PointOnObject(g29,g-24)
    c: Equal(g29,g30)
    c: Coincident(g29,g30)
    c: Equal(g29,g31)
    c: Coincident(g29,g31)
    c: Coincident(g12,g3)
    c: Coincident(g13,g20)
    c: Coincident(g11,g22)
    c: PointOnObject(g8,g22)
    c: PointOnObject(g9,g21)
    c: PointOnObject(g32,g0)
    c: Coincident(g7,g25)
    c: PointOnObject(g10,g3)
    c: Coincident(g4,g20)
    c: Coincident(g5,g21)
    c: Coincident(g33,g0)
    c: Coincident(g6,g23)
    c: PointOnObject(g14,g23)
    c: PointOnObject(g15,g24)
    c: PointOnObject(g17,g24)
    c: PointOnObject(g16,g25)
    c: Coincident(g19,g2)
    c: Coincident(g18,g2)
    c: Coincident(g26,g30)
    c: Coincident(g28,g29)
    c: Coincident(g27,g31)
    c: Coincident(g34,g29)
    c: Coincident(g34,g26)
    c: Coincident(g35,g30)
    c: Horizontal(g35)
    c: Coincident(g36,g35)
    c: Coincident(g36,g31)
    c: Vertical(g36)
    c: Coincident(g37,g29)
    c: Coincident(g38,g2)
    c: Coincident(g39,g1)
    c: Diameter(g39) = 3.9
    c: Diameter(g38) = 3.9
    c: Diameter(g37) = 3.9
    c: Coincident(g40,g3)
    c: Diameter(g40) = 3.9
    c: Coincident(g41,g0)
    c: Diameter(g41) = 3.9
FEATURE [PartDesign::Pad] Pad008  label="Case.TopBorder.Body"
  BaseFeature = -> Pad009
  Direction = (0,0,1)
  Length = 7
  Length2 = 10
  Placement = pos=(0,0,6) rot=(0,0,1;0rad)
  Profile = -> Sketch058
  ReferenceAxis = -> Sketch058 [N_Axis]
  Suppressed = false
  Type = 0
  expr: Length = Spreadsheet.CaseTopTopBorderHeight
FEATURE [PartDesign::Pad] Pad013  label="Postes"
  BaseFeature = -> Pad008
  Direction = (0,0,-1)
  Length = 2.6
  Length2 = 10
  Placement = pos=(0,0,6) rot=(0,0,1;0rad)
  Profile = -> Sketch077
  ReferenceAxis = -> Sketch077 [N_Axis]
  Suppressed = false
  Type = 0
FEATURE [Sketcher::SketchObject] Sketch078
  AttachmentSupport = -> [Pad013]
  ExternalGeometry = -> [Pad013]
  FullyConstrained = false
  MapMode = 5
  Placement = pos=(0,0,6) rot=(1,0,0;3.14159rad)
  sketch-geometry (95):
    g0: LineSegment StartX=19.54 StartY=-0.54 StartZ=0 EndX=19.54 EndY=-16.3162 EndZ=0
    g1: LineSegment StartX=18.54 StartY=-0.54 StartZ=0 EndX=18.54 EndY=-1.88641 EndZ=0
    g2: LineSegment StartX=37.59 StartY=-0.54 StartZ=0 EndX=37.59 EndY=-1.54 EndZ=0
    g3: LineSegment StartX=36.59 StartY=-19.58 StartZ=0 EndX=20.8994 EndY=-19.58 EndZ=0
    g4: LineSegment StartX=36.59 StartY=-38.63 StartZ=0 EndX=21.2556 EndY=-38.63 EndZ=0
    g5: LineSegment StartX=38.59 StartY=-22.39 StartZ=0 EndX=55.64 EndY=-22.39 EndZ=0
    g6: LineSegment StartX=55.64 StartY=-24.39 StartZ=0 EndX=38.59 EndY=-24.39 EndZ=0
    g7: LineSegment StartX=38.59 StartY=-41.44 StartZ=0 EndX=55.64 EndY=-41.44 EndZ=0
    g8: LineSegment StartX=55.64 StartY=-43.44 StartZ=0 EndX=38.59 EndY=-43.44 EndZ=0
    g9: LineSegment StartX=57.64 StartY=-43.74 StartZ=0 EndX=74.69 EndY=-43.74 EndZ=0
    g10: LineSegment StartX=74.69 StartY=-45.74 StartZ=0 EndX=57.64 EndY=-45.74 EndZ=0
    g11: LineSegment StartX=74.69 StartY=-26.7254 StartZ=0 EndX=57.64 EndY=-26.7254 EndZ=0
    g12: LineSegment StartX=57.64 StartY=-24.69 StartZ=0 EndX=74.69 EndY=-24.69 EndZ=0
    g13: LineSegment StartX=57.64 StartY=-7.65 StartZ=0 EndX=74.69 EndY=-7.65 EndZ=0
    g14: LineSegment StartX=74.69 StartY=-5.65 StartZ=0 EndX=59.2888 EndY=-5.65 EndZ=0
    g15: LineSegment StartX=76.69 StartY=-5.25 StartZ=0 EndX=93.74 EndY=-5.25 EndZ=0
    g16: LineSegment StartX=76.69 StartY=-22.29 StartZ=0 EndX=93.74 EndY=-22.29 EndZ=0
    g17: LineSegment StartX=93.74 StartY=-24.29 StartZ=0 EndX=76.69 EndY=-24.29 EndZ=0
    g18: LineSegment StartX=76.69 StartY=-41.34 StartZ=0 EndX=91.9041 EndY=-41.34 EndZ=0
    g19: LineSegment StartX=92.4501 StartY=-43.34 StartZ=0 EndX=76.69 EndY=-43.34 EndZ=0
    g20: LineSegment StartX=95.74 StartY=-19.96 StartZ=0 EndX=112.79 EndY=-19.96 EndZ=0
    g21: LineSegment StartX=112.79 StartY=-21.96 StartZ=0 EndX=95.74 EndY=-21.96 EndZ=0
    g22: LineSegment StartX=36.59 StartY=-17.58 StartZ=0 EndX=36.59 EndY=-0.54 EndZ=0
    g23: LineSegment StartX=38.59 StartY=-24.39 StartZ=0 EndX=38.59 EndY=-41.44 EndZ=0
    g24: LineSegment StartX=55.64 StartY=-22.39 StartZ=0 EndX=55.6369 EndY=-5.65 EndZ=0
    g25: LineSegment StartX=57.64 StartY=-26.7254 StartZ=0 EndX=57.64 EndY=-43.74 EndZ=0
    g26: LineSegment StartX=36.59 StartY=-36.63 StartZ=0 EndX=36.59 EndY=-19.58 EndZ=0
    g27: LineSegment StartX=55.64 StartY=-41.44 StartZ=0 EndX=55.64 EndY=-24.39 EndZ=0
    g28: LineSegment StartX=74.69 StartY=-41.34 StartZ=0 EndX=74.69 EndY=-26.7254 EndZ=0
    g29: LineSegment StartX=74.69 StartY=-24.69 StartZ=0 EndX=74.69 EndY=-7.65 EndZ=0
    g30: LineSegment StartX=74.69 StartY=-5.65 StartZ=0 EndX=74.69 EndY=-3.26258 EndZ=0
    g31: LineSegment StartX=76.69 StartY=-5.25 StartZ=0 EndX=76.69 EndY=-22.29 EndZ=0
    g32: LineSegment StartX=93.74 StartY=-22.29 StartZ=0 EndX=93.74 EndY=-5.25 EndZ=0
    g33: LineSegment StartX=95.74 StartY=-21.96 StartZ=0 EndX=95.74 EndY=-39.01 EndZ=0
    g34: LineSegment StartX=57.64 StartY=-7.65 StartZ=0 EndX=57.64 EndY=-24.69 EndZ=0
    g35: LineSegment StartX=112.79 StartY=-39.01 StartZ=0 EndX=95.74 EndY=-39.01 EndZ=0
    g36: LineSegment StartX=96.9808 StartY=-41.01 StartZ=0 EndX=112.79 EndY=-41.01 EndZ=0
    g37: LineSegment StartX=93.74 StartY=-39.2188 StartZ=0 EndX=93.74 EndY=-24.29 EndZ=0
    g38: LineSegment StartX=17.54 StartY=-35.2577 StartZ=0 EndX=17.54 EndY=-20.995 EndZ=0
    g39: LineSegment StartX=21.175 StartY=-36.63 StartZ=0 EndX=36.59 EndY=-36.63 EndZ=0
    g40: LineSegment StartX=17.54 StartY=-16.3082 StartZ=0 EndX=17.54 EndY=1.69509 EndZ=0
    g41: LineSegment StartX=20.8382 StartY=-17.58 StartZ=0 EndX=36.59 EndY=-17.58 EndZ=0
    g42: LineSegment StartX=19.54 StartY=-20.987 StartZ=0 EndX=19.54 EndY=-35.1452 EndZ=0
    g43: ArcOfCircle CenterX=18.6824 CenterY=-37.7321 CenterZ=0 NormalX=0 NormalY=0 NormalZ=1 AngleXU=0 Radius=2.72539 StartAngle=3.47733 EndAngle=4.27987
    g44: ArcOfCircle CenterX=18.5307 CenterY=-18.6516 CenterZ=0 NormalX=0 NormalY=0 NormalZ=1 AngleXU=0 Radius=2.54419 StartAngle=5.12032 EndAngle=5.90965
    g45: ArcOfCircle CenterX=94.4774 CenterY=-41.712 CenterZ=0 NormalX=0 NormalY=0 NormalZ=1 AngleXU=0 Radius=2.59999 StartAngle=3.8182 EndAngle=4.42484
    g46: ArcOfCircle CenterX=18.6824 CenterY=-37.7321 CenterZ=0 NormalX=0 NormalY=0 NormalZ=1 AngleXU=0 Radius=2.72539 StartAngle=2.00331 EndAngle=2.72529
    g47: ArcOfCircle CenterX=18.6824 CenterY=-37.7321 CenterZ=0 NormalX=0 NormalY=0 NormalZ=1 AngleXU=0 Radius=2.72539 StartAngle=0.4163 EndAngle=1.25067
    g48: ArcOfCircle CenterX=18.6824 CenterY=-37.7321 CenterZ=0 NormalX=0 NormalY=0 NormalZ=1 AngleXU=0 Radius=2.72539 StartAngle=5.03251 EndAngle=5.94745
    g49: ArcOfCircle CenterX=18.5307 CenterY=-18.6516 CenterZ=0 NormalX=0 NormalY=0 NormalZ=1 AngleXU=0 Radius=2.54419 StartAngle=3.51513 EndAngle=4.31241
    g50: ArcOfCircle CenterX=18.5307 CenterY=-18.6516 CenterZ=0 NormalX=0 NormalY=0 NormalZ=1 AngleXU=0 Radius=2.54419 StartAngle=1.97077 EndAngle=2.70683
    g51: ArcOfCircle CenterX=18.5307 CenterY=-18.6516 CenterZ=0 NormalX=0 NormalY=0 NormalZ=1 AngleXU=0 Radius=2.54419 StartAngle=0.43476 EndAngle=1.16287
    g52: LineSegment StartX=74.69 StartY=-41.34 StartZ=0 EndX=74.69 EndY=-43.74 EndZ=0
    g53: ArcOfCircle CenterX=94.4774 CenterY=-41.712 CenterZ=0 NormalX=0 NormalY=0 NormalZ=1 AngleXU=0 Radius=2.59999 StartAngle=5.21948 EndAngle=6.55658
    g54: ArcOfCircle CenterX=94.4774 CenterY=-41.712 CenterZ=0 NormalX=0 NormalY=0 NormalZ=1 AngleXU=0 Radius=2.59999 StartAngle=1.85834 EndAngle=2.99802
    g55: LineSegment StartX=19.54 StartY=-0.54 StartZ=0 EndX=36.59 EndY=-0.54 EndZ=0
    g56: LineSegment StartX=17.54 StartY=1.69509 StartZ=0 EndX=38.59 EndY=1.69509 EndZ=0
    g57: LineSegment StartX=38.59 StartY=-5.35 StartZ=0 EndX=55.6369 EndY=-5.35 EndZ=0
    g58: LineSegment StartX=59.2888 StartY=-3.35 StartZ=0 EndX=38.59 EndY=-3.35 EndZ=0
    g59: LineSegment StartX=55.6369 StartY=-5.65 StartZ=0 EndX=55.6369 EndY=-5.35 EndZ=0
    g60: LineSegment StartX=38.59 StartY=-5.35 StartZ=0 EndX=38.59 EndY=-22.39 EndZ=0
    g61: LineSegment StartX=-1.95892 StartY=-17.58 StartZ=0 EndX=-1.95892 EndY=-19.58 EndZ=0
    g62: LineSegment StartX=-1.97545 StartY=-36.63 StartZ=0 EndX=-1.97545 EndY=-38.63 EndZ=0
    g63: LineSegment StartX=19.54 StartY=-58.014 StartZ=0 EndX=17.54 EndY=-58.014 EndZ=0
    g64: LineSegment StartX=38.59 StartY=-62.7065 StartZ=0 EndX=36.59 EndY=-62.7065 EndZ=0
    g65: LineSegment StartX=57.64 StartY=-64.7796 StartZ=0 EndX=55.64 EndY=-64.7796 EndZ=0
    g66: LineSegment StartX=74.69 StartY=-65.1109 StartZ=0 EndX=76.69 EndY=-65.1109 EndZ=0
    g67: LineSegment StartX=93.74 StartY=-62.889 StartZ=0 EndX=95.74 EndY=-62.889 EndZ=0
    g68: LineSegment StartX=114.79 StartY=-60.5274 StartZ=0 EndX=112.79 EndY=-60.5274 EndZ=0
    g69: LineSegment StartX=112.79 StartY=-39.01 StartZ=0 EndX=112.79 EndY=-21.96 EndZ=0
    g70: LineSegment StartX=93.74 StartY=-0.92 StartZ=0 EndX=114.79 EndY=-0.92 EndZ=0
    g71: LineSegment StartX=112.79 StartY=-2.92 StartZ=0 EndX=95.74 EndY=-2.92 EndZ=0
    g72: LineSegment StartX=93.74 StartY=-3.26258 StartZ=0 EndX=93.74 EndY=-0.92 EndZ=0
    g73: LineSegment StartX=112.79 StartY=-19.96 StartZ=0 EndX=112.79 EndY=-2.92 EndZ=0
    g74: LineSegment StartX=112.79 StartY=-60.5274 StartZ=0 EndX=112.79 EndY=-41.01 EndZ=0
    g75: LineSegment StartX=-1.95892 StartY=-19.58 StartZ=0 EndX=16.162 EndY=-19.58 EndZ=0
    g76: LineSegment StartX=-1.95892 StartY=-17.58 StartZ=0 EndX=16.2232 EndY=-17.58 EndZ=0
    g77: LineSegment StartX=76.69 StartY=-41.34 StartZ=0 EndX=76.69 EndY=-24.29 EndZ=0
    g78: LineSegment StartX=17.54 StartY=-58.014 StartZ=0 EndX=17.54 EndY=-40.2065 EndZ=0
    g79: LineSegment StartX=19.54 StartY=-40.319 StartZ=0 EndX=19.54 EndY=-58.014 EndZ=0
    g80: LineSegment StartX=74.69 StartY=-3.26258 StartZ=0 EndX=93.74 EndY=-3.26258 EndZ=0
    g81: LineSegment StartX=114.79 StartY=-0.92 StartZ=0 EndX=114.79 EndY=-60.5274 EndZ=0
    g82: LineSegment StartX=93.74 StartY=-62.889 StartZ=0 EndX=93.74 EndY=-44.2052 EndZ=0
    g83: LineSegment StartX=95.74 StartY=-43.9848 StartZ=0 EndX=95.74 EndY=-62.889 EndZ=0
    g84: LineSegment StartX=74.69 StartY=-65.1109 StartZ=0 EndX=74.69 EndY=-45.74 EndZ=0
    g85: LineSegment StartX=76.69 StartY=-65.1109 StartZ=0 EndX=76.69 EndY=-43.34 EndZ=0
    g86: LineSegment StartX=55.64 StartY=-64.7796 StartZ=0 EndX=55.64 EndY=-43.44 EndZ=0
    g87: LineSegment StartX=57.64 StartY=-64.7796 StartZ=0 EndX=57.64 EndY=-45.74 EndZ=0
    g88: LineSegment StartX=38.59 StartY=-43.44 StartZ=0 EndX=38.59 EndY=-62.7065 EndZ=0
    g89: LineSegment StartX=36.59 StartY=-62.7065 StartZ=0 EndX=36.59 EndY=-38.63 EndZ=0
    g90: LineSegment StartX=16.1091 StartY=-38.63 StartZ=0 EndX=-1.97545 EndY=-38.63 EndZ=0
    g91: LineSegment StartX=16.1897 StartY=-36.63 StartZ=0 EndX=-1.97545 EndY=-36.63 EndZ=0
    g92: LineSegment StartX=59.2888 StartY=-5.65 StartZ=0 EndX=59.2888 EndY=-3.35 EndZ=0
    g93: LineSegment StartX=38.59 StartY=-3.35 StartZ=0 EndX=38.59 EndY=1.69509 EndZ=0
    g94: LineSegment StartX=95.74 StartY=-19.96 StartZ=0 EndX=95.74 EndY=-2.92 EndZ=0
  constraints (186):
    c: Vertical(g0)
    c: Vertical(g1)
    c: Distance(g2) = 1
    c: DistanceX(g-5,g22) = 1.52
    c: Horizontal(g3)
    c: Horizontal(g4)
    c: Horizontal(g5)
    c: Horizontal(g6)
    c: Horizontal(g8)
    c: Horizontal(g11)
    c: Horizontal(g12)
    c: Horizontal(g13)
    c: Horizontal(g14)
    c: Horizontal(g15)
    c: Horizontal(g16)
    c: Horizontal(g17)
    c: Horizontal(g18)
    c: Horizontal(g19)
    c: Distance(g-14,g9) = 1.52
    c: Distance(g-15,g18) = 1.52
    c: Distance(g-9,g12) = 1.52
    c: Distance(g-10,g16) = 1.52
    c: Distance(g-10,g15) = 1.52
    c: Distance(g-9,g13) = 1.52
    c: Distance(g-6,g5) = 1.52
    c: Horizontal(g20)
    c: Horizontal(g21)
    c: Distance(g-12,g20) = 1.52
    c: Coincident(g41,g22)
    c: Coincident(g6,g23)
    c: Coincident(g24,g5)
    c: Coincident(g25,g11)
    c: Coincident(g27,g6)
    c: Coincident(g34,g12)
    c: Coincident(g26,g3)
    c: Coincident(g60,g5)
    c: Coincident(g39,g26)
    c: Coincident(g23,g7)
    c: Coincident(g7,g27)
    c: PointOnObject(g25,g9)
    c: PointOnObject(g28,g18)
    c: Coincident(g28,g11)
    c: Coincident(g29,g12)
    c: Coincident(g31,g16)
    c: Coincident(g29,g13)
    c: Coincident(g30,g14)
    c: Coincident(g15,g32)
    c: Coincident(g37,g17)
    c: Coincident(g32,g16)
    c: Coincident(g33,g21)
    c: Coincident(g13,g34)
    c: Coincident(g15,g31)
    c: Horizontal(g35)
    c: Horizontal(g36)
    c: Distance(g-17,g35) = 1.52
    c: Coincident(g35,g33)
    c: Equal(g43,g46)
    c: Coincident(g47,g42)
    c: Coincident(g46,g38)
    c: Coincident(g43,g46)
    c: Equal(g43,g47)
    c: Coincident(g48,g4)
    c: Coincident(g47,g39)
    c: Coincident(g43,g47)
    c: Equal(g43,g48)
    c: Coincident(g43,g48)
    c: Coincident(g49,g38)
    c: Coincident(g44,g42)
    c: Equal(g44,g49)
    c: Coincident(g44,g49)
    c: Equal(g44,g50)
    c: Coincident(g51,g0)
    c: Coincident(g50,g40)
    c: Coincident(g44,g50)
    c: Equal(g44,g51)
    c: Coincident(g44,g3)
    c: Coincident(g51,g41)
    c: Coincident(g44,g51)
    c: Coincident(g52,g28)
    c: Coincident(g52,g9)
    c: Vertical(g52)
    c: PointOnObject(g37,g45)
    c: Coincident(g54,g18)
    c: Coincident(g19,g45)
    c: PointOnObject(g36,g45)
    c: Equal(g45,g53)
    c: Coincident(g45,g53)
    c: Equal(g53,g54)
    c: PointOnObject(g53,g36)
    c: PointOnObject(g54,g37)
    c: Coincident(g53,g54)
    c: Horizontal(g55)
    c: Distance(g-4,g55) = 1.52
    c: PointOnObject(g55,g22)
    c: Coincident(g55,g0)
    c: Horizontal(g56)
    c: Coincident(g56,g40)
    c: Horizontal(g57)
    c: Horizontal(g58)
    c: Distance(g-6,g57) = 1.52
    c: Coincident(g59,g24)
    c: Vertical(g59)
    c: Coincident(g57,g59)
    c: Coincident(g57,g60)
    c: Vertical(g61)
    c: Vertical(g62)
    c: Horizontal(g63)
    c: Horizontal(g64)
    c: Horizontal(g65)
    c: Horizontal(g66)
    c: Horizontal(g67)
    c: Horizontal(g68)
    c: Vertical(g69)
    c: Distance(g-18,g69) = 1.52
    c: Horizontal(g70)
    c: Horizontal(g71)
    c: Distance(g-12,g71) = 1.52
    c: Vertical(g72)
    c: Coincident(g70,g72)
    c: Coincident(g71,g73)
    c: Coincident(g73,g20)
    c: Coincident(g21,g69)
    c: Coincident(g69,g35)
    c: Coincident(g74,g68)
    c: Coincident(g74,g36)
    c: Vertical(g74)
    c: Coincident(g75,g61)
    c: Coincident(g75,g49)
    c: Horizontal(g75)
    c: Coincident(g76,g61)
    c: Coincident(g76,g50)
    c: Horizontal(g76)
    c: Coincident(g77,g18)
    c: Coincident(g77,g17)
    c: Vertical(g77)
    c: Coincident(g78,g63)
    c: Coincident(g78,g43)
    c: Vertical(g78)
    c: Coincident(g79,g48)
    c: Coincident(g79,g63)
    c: Vertical(g79)
    c: Coincident(g80,g30)
    c: Coincident(g80,g72)
    c: Horizontal(g80)
    c: Coincident(g81,g70)
    c: Coincident(g81,g68)
    c: Vertical(g81)
    c: Coincident(g82,g67)
    c: Coincident(g82,g45)
    c: Vertical(g82)
    c: Coincident(g83,g53)
    c: Coincident(g83,g67)
    c: Vertical(g83)
    c: Coincident(g84,g66)
    c: Coincident(g84,g10)
    c: Vertical(g84)
    c: Coincident(g85,g66)
    c: Coincident(g85,g19)
    c: Vertical(g85)
    c: Coincident(g86,g65)
    c: Coincident(g86,g8)
    c: Vertical(g86)
    c: Coincident(g87,g65)
    c: Coincident(g87,g10)
    c: Vertical(g87)
    c: Coincident(g88,g8)
    c: Coincident(g88,g64)
    c: Vertical(g88)
    c: Coincident(g89,g64)
    c: Coincident(g89,g4)
    c: Vertical(g89)
    c: Coincident(g90,g43)
    c: Coincident(g90,g62)
    c: Horizontal(g90)
    c: Coincident(g91,g46)
    c: Coincident(g91,g62)
    c: Horizontal(g91)
    c: Coincident(g92,g14)
    c: Coincident(g92,g58)
    c: Vertical(g92)
    c: Coincident(g93,g58)
    c: Coincident(g93,g56)
    c: Vertical(g93)
    c: Coincident(g94,g20)
    c: Coincident(g94,g71)
    c: Vertical(g94)
FEATURE [PartDesign::Pad] Pad014  label="Refuerzos"
  BaseFeature = -> Pad013
  Direction = (0,0,-1)
  Length = 2
  Length2 = 10
  Placement = pos=(0,0,6) rot=(0,0,1;0rad)
  Profile = -> Sketch078
  ReferenceAxis = -> Sketch078 [N_Axis]
  Suppressed = false
  Type = 0
FEATURE [Sketcher::SketchObject] Sketch079
  AttachmentSupport = -> [Pad014]
  ExternalGeometry = -> [Pad014]
  FullyConstrained = false
  MapMode = 5
  Placement = pos=(0,0,3.4) rot=(1,0,0;3.14159rad)
  sketch-geometry (5):
    g0: Circle CenterX=18.6 CenterY=-18.76 CenterZ=0 NormalX=0 NormalY=0 NormalZ=1 AngleXU=0 Radius=1.95
    g1: Circle CenterX=18.61 CenterY=-37.51 CenterZ=0 NormalX=0 NormalY=0 NormalZ=1 AngleXU=0 Radius=1.95
    g2: Circle CenterX=94.55 CenterY=-41.5 CenterZ=0 NormalX=0 NormalY=0 NormalZ=1 AngleXU=0 Radius=1.95
    g3: Circle CenterX=108.3 CenterY=6.24 CenterZ=0 NormalX=0 NormalY=0 NormalZ=1 AngleXU=0 Radius=1.95
    g4: Circle CenterX=61.84 CenterY=-1.51 CenterZ=0 NormalX=0 NormalY=0 NormalZ=1 AngleXU=0 Radius=1.95
  constraints (5):
    c: Coincident(g0,g-3)
    c: Coincident(g1,g-4)
    c: Coincident(g2,g-5)
    c: Coincident(g3,g-6)
    c: Coincident(g4,g-7)
FEATURE [PartDesign::Pocket] Pocket
  BaseFeature = -> Pad014
  Direction = (0,0,1)
  Length = 3
  Length2 = 5
  Placement = pos=(0,0,6) rot=(0,0,1;0rad)
  Profile = -> Sketch079
  ReferenceAxis = -> Sketch079 [N_Axis]
  Suppressed = false
  Type = 0
  expr: Length = Spreadsheet.ThreadedInsertHeight
FEATURE [Sketcher::SketchObject] Sketch080
  AttachmentOffset = pos=(0,0,30) rot=(0,0,1;0rad)
  AttachmentSupport = -> [Pocket]
  FullyConstrained = false
  MapMode = 5
  Placement = pos=(0,-33,6) rot=(1,0,0;1.5708rad)
  sketch-geometry (4):
    g0: LineSegment StartX=-12.0444 StartY=16.4808 StartZ=0 EndX=-12.0444 EndY=2.04826 EndZ=0
    g1: LineSegment StartX=-12.0444 StartY=2.04826 StartZ=0 EndX=141.831 EndY=2.04826 EndZ=0
    g2: LineSegment StartX=141.831 StartY=2.04826 StartZ=0 EndX=141.831 EndY=16.4808 EndZ=0
    g3: LineSegment StartX=141.831 StartY=16.4808 StartZ=0 EndX=-12.0444 EndY=16.4808 EndZ=0
  constraints (8):
    c: Coincident(g0,g1)
    c: Coincident(g1,g2)
    c: Coincident(g2,g3)
    c: Coincident(g3,g0)
    c: Vertical(g0)
    c: Vertical(g2)
    c: Horizontal(g1)
    c: Horizontal(g3)
FEATURE [PartDesign::Pocket] Pocket007  label="EliminaBordeSuperior"
  BaseFeature = -> Pocket
  Direction = (0,1,-2e-16)
  Length = 100
  Length2 = 5
  Placement = pos=(0,0,6) rot=(0,0,1;0rad)
  Profile = -> Sketch080
  ReferenceAxis = -> Sketch080 [N_Axis]
  Suppressed = false
  Type = 0
FEATURE [PartDesign::ShapeBinder] ShapeBinder
  Placement = pos=(0,-2.7e-15,-22) rot=(0,0,1;0rad)
  Support = -> [Pocket007]
  TraceSupport = false
FEATURE [Sketcher::SketchObject] Sketch081
  AttachmentOffset = pos=(0,0,1) rot=(0,0,1;0rad)
  AttachmentSupport = -> [ShapeBinder]
  ExternalGeometry = -> [ShapeBinder]
  FullyConstrained = true
  MapMode = 5
  Placement = pos=(0,-2.7e-15,-17) rot=(1,0,0;3.14159rad)
  sketch-geometry (18):
    g0: LineSegment StartX=-3 StartY=3 StartZ=0 EndX=54.1734 EndY=3 EndZ=0
    g1: LineSegment StartX=54.1734 StartY=3 StartZ=0 EndX=64.7598 EndY=17.5123 EndZ=0
    g2: LineSegment StartX=64.7598 StartY=17.5123 StartZ=0 EndX=102.946 EndY=22.4786 EndZ=0
    g3: LineSegment StartX=102.946 StartY=22.4786 StartZ=0 EndX=120.725 EndY=32.764 EndZ=0
    g4: LineSegment StartX=120.725 StartY=32.764 StartZ=0 EndX=136.73 EndY=4.96388 EndZ=0
    g5: LineSegment StartX=136.73 StartY=4.96388 StartZ=0 EndX=136.73 EndY=-59.5 EndZ=0
    g6: LineSegment StartX=136.73 StartY=-59.5 StartZ=0 EndX=115.98 EndY=-59.5 EndZ=0
    g7: LineSegment StartX=115.98 StartY=-59.5 StartZ=0 EndX=115.98 EndY=-61.75 EndZ=0
    g8: LineSegment StartX=115.98 StartY=-61.75 StartZ=0 EndX=96.98 EndY=-61.75 EndZ=0
    g9: LineSegment StartX=96.98 StartY=-61.75 StartZ=0 EndX=96.98 EndY=-64 EndZ=0
    g10: LineSegment StartX=96.98 StartY=-64 StartZ=0 EndX=77.98 EndY=-64 EndZ=0
    g11: LineSegment StartX=77.98 StartY=-64 StartZ=0 EndX=77.98 EndY=-66.25 EndZ=0
    g12: LineSegment StartX=77.98 StartY=-66.25 StartZ=0 EndX=53.98 EndY=-66.25 EndZ=0
    g13: LineSegment StartX=53.98 StartY=-66.25 StartZ=0 EndX=53.98 EndY=-64 EndZ=0
    g14: LineSegment StartX=53.98 StartY=-64 StartZ=0 EndX=34.98 EndY=-64 EndZ=0
    g15: LineSegment StartX=34.98 StartY=-64 StartZ=0 EndX=34.98 EndY=-59.25 EndZ=0
    g16: LineSegment StartX=34.98 StartY=-59.25 StartZ=0 EndX=-3 EndY=-59.25 EndZ=0
    g17: LineSegment StartX=-3 StartY=-59.25 StartZ=0 EndX=-3 EndY=3 EndZ=0
  constraints (49):
    c: Horizontal(g0)
    c: Coincident(g0,g1)
    c: Coincident(g1,g2)
    c: Coincident(g2,g3)
    c: Coincident(g3,g4)
    c: Coincident(g4,g5)
    c: Vertical(g5)
    c: Coincident(g5,g6)
    c: Horizontal(g6)
    c: Coincident(g6,g7)
    c: Coincident(g7,g8)
    c: Coincident(g8,g9)
    c: Coincident(g9,g10)
    c: Coincident(g10,g11)
    c: Vertical(g11)
    c: Coincident(g11,g12)
    c: Horizontal(g12)
    c: Coincident(g12,g13)
    c: Coincident(g13,g14)
    c: Horizontal(g14)
    c: Coincident(g14,g15)
    c: Coincident(g15,g16)
    c: Horizontal(g16)
    c: Coincident(g16,g17)
    c: Coincident(g17,g0)
    c: Vertical(g17)
    c: Coincident(g16,g-4)
    c: Vertical(g15)
    c: Vertical(g15,g-6)
    c: Horizontal(g-8,g14)
    c: Vertical(g13)
    c: Vertical(g13,g-11)
    c: Horizontal(g12,g-12)
    c: Horizontal(g10)
    c: Vertical(g11,g-14)
    c: Horizontal(g10,g-16)
    c: Vertical(g9)
    c: Horizontal(g8)
    c: Vertical(g9,g-18)
    c: Horizontal(g8,g-20)
    c: Vertical(g7)
    c: Vertical(g7,g-22)
    c: Horizontal(g6,g-24)
    c: Parallel(g4,g-27)
    c: Coincident(g4,g-27)
    c: Parallel(g3,g-29)
    c: Coincident(g2,g-30)
    c: Coincident(g1,g-31)
    c: Coincident(g0,g-32)
FEATURE [Sketcher::SketchObject] Sketch082
  ExternalGeometry = -> [ShapeBinder,Sketch081]
  FullyConstrained = false
  MapMode = 5
  Placement = pos=(0,-2.4e-15,-12) rot=(0,0,1;0rad)
  sketch-geometry (45):
    g0: LineSegment StartX=-9.85985 StartY=70.6655 StartZ=0 EndX=-9.85985 EndY=-37.2919 EndZ=0
    g1: LineSegment StartX=-9.85985 StartY=-37.2919 StartZ=0 EndX=149.522 EndY=-37.2919 EndZ=0
    g2: LineSegment StartX=149.522 StartY=-37.2919 StartZ=0 EndX=149.522 EndY=70.6655 EndZ=0
    g3: LineSegment StartX=149.522 StartY=70.6655 StartZ=0 EndX=-9.85985 EndY=70.6655 EndZ=0
    g4: LineSegment StartX=1 StartY=55.25 StartZ=0 EndX=38.98 EndY=55.25 EndZ=0
    g5: LineSegment StartX=38.98 StartY=55.25 StartZ=0 EndX=38.98 EndY=60 EndZ=0
    g6: LineSegment StartX=38.98 StartY=60 StartZ=0 EndX=57.98 EndY=60 EndZ=0
    g7: LineSegment StartX=57.98 StartY=60 StartZ=0 EndX=57.98 EndY=62.25 EndZ=0
    g8: LineSegment StartX=57.98 StartY=62.25 StartZ=0 EndX=73.98 EndY=62.25 EndZ=0
    g9: LineSegment StartX=73.98 StartY=62.25 StartZ=0 EndX=73.98 EndY=60 EndZ=0
    g10: LineSegment StartX=73.98 StartY=60 StartZ=0 EndX=92.98 EndY=60 EndZ=0
    g11: LineSegment StartX=92.98 StartY=60 StartZ=0 EndX=92.98 EndY=57.75 EndZ=0
    g12: LineSegment StartX=92.98 StartY=57.75 StartZ=0 EndX=111.98 EndY=57.75 EndZ=0
    g13: LineSegment StartX=111.98 StartY=57.75 StartZ=0 EndX=111.98 EndY=55.5 EndZ=0
    g14: LineSegment StartX=111.98 StartY=55.5 StartZ=0 EndX=132.73 EndY=55.5 EndZ=0
    g15: LineSegment StartX=132.73 StartY=55.5 StartZ=0 EndX=132.73 EndY=-3.89471 EndZ=0
    g16: LineSegment StartX=132.73 StartY=-3.89471 StartZ=0 EndX=119.258 EndY=-27.2944 EndZ=0
    g17: LineSegment StartX=119.258 StartY=-27.2944 StartZ=0 EndX=104.256 EndY=-18.6153 EndZ=0
    g18: LineSegment StartX=104.256 StartY=-18.6153 StartZ=0 EndX=66.9791 EndY=-13.7673 EndZ=0
    g19: LineSegment StartX=66.9791 StartY=-13.7673 StartZ=0 EndX=56.2066 EndY=1 EndZ=0
    g20: LineSegment StartX=56.2066 StartY=1 StartZ=0 EndX=1 EndY=1 EndZ=0
    g21: LineSegment StartX=1 StartY=1 StartZ=0 EndX=1 EndY=55.25 EndZ=0
    g22: LineSegment StartX=41.3919 StartY=60 StartZ=0 EndX=41.3919 EndY=64 EndZ=0
    g23: LineSegment StartX=63.7997 StartY=66.25 StartZ=0 EndX=63.7997 EndY=62.25 EndZ=0
    g24: LineSegment StartX=86.9267 StartY=60 StartZ=0 EndX=86.9267 EndY=64 EndZ=0
    g25: LineSegment StartX=104.315 StartY=61.75 StartZ=0 EndX=104.315 EndY=57.75 EndZ=0
    g26: LineSegment StartX=122.355 StartY=55.5 StartZ=0 EndX=122.355 EndY=59.5 EndZ=0
    g27: LineSegment StartX=136.73 StartY=30.7806 StartZ=0 EndX=132.73 EndY=30.7806 EndZ=0
    g28: LineSegment StartX=127.031 StartY=-13.7927 StartZ=0 EndX=130.498 EndY=-15.7885 EndZ=0
    g29: LineSegment StartX=111.757 StartY=-22.9549 StartZ=0 EndX=109.754 EndY=-26.4172 EndZ=0
    g30: LineSegment StartX=85.6175 StartY=-16.1913 StartZ=0 EndX=85.1016 EndY=-20.1579 EndZ=0
    g31: LineSegment StartX=62.6911 StartY=-7.8891 StartZ=0 EndX=59.4595 EndY=-10.2465 EndZ=0
    g32: LineSegment StartX=38.0462 StartY=1 StartZ=0 EndX=38.0462 EndY=-3 EndZ=0
    g33: LineSegment StartX=-3 StartY=5.13949 StartZ=0 EndX=1 EndY=5.13949 EndZ=0
    g34: LineSegment StartX=15.99 StartY=59.25 StartZ=0 EndX=15.99 EndY=55.25 EndZ=0
    g35: LineSegment StartX=34.98 StartY=59.25 StartZ=0 EndX=34.98 EndY=55.25 EndZ=0
    g36: LineSegment StartX=38.98 StartY=58.552 StartZ=0 EndX=34.98 EndY=58.552 EndZ=0
    g37: LineSegment StartX=53.98 StartY=64 StartZ=0 EndX=53.98 EndY=59.4641 EndZ=0
    g38: LineSegment StartX=57.98 StartY=61.2941 StartZ=0 EndX=53.98 EndY=61.2941 EndZ=0
    g39: LineSegment StartX=77.98 StartY=64 StartZ=0 EndX=77.98 EndY=60 EndZ=0
    g40: LineSegment StartX=73.98 StartY=61.5546 StartZ=0 EndX=77.98 EndY=61.5546 EndZ=0
    g41: LineSegment StartX=96.98 StartY=61.75 StartZ=0 EndX=96.98 EndY=57.75 EndZ=0
    g42: LineSegment StartX=92.98 StartY=59.3466 StartZ=0 EndX=96.98 EndY=59.3466 EndZ=0
    g43: LineSegment StartX=115.98 StartY=59.5 StartZ=0 EndX=115.98 EndY=55.5 EndZ=0
    g44: LineSegment StartX=111.98 StartY=57.0369 StartZ=0 EndX=115.98 EndY=57.0369 EndZ=0
  constraints (130):
    c: Coincident(g0,g1)
    c: Coincident(g1,g2)
    c: Coincident(g2,g3)
    c: Coincident(g3,g0)
    c: Vertical(g0)
    c: Vertical(g2)
    c: Horizontal(g1)
    c: Horizontal(g3)
    c: Horizontal(g4)
    c: Coincident(g4,g5)
    c: Vertical(g5)
    c: Coincident(g5,g6)
    c: Horizontal(g6)
    c: Coincident(g6,g7)
    c: Vertical(g7)
    c: Coincident(g7,g8)
    c: Horizontal(g8)
    c: Coincident(g8,g9)
    c: Coincident(g9,g10)
    c: Horizontal(g10)
    c: Coincident(g10,g11)
    c: Vertical(g11)
    c: Coincident(g11,g12)
    c: Horizontal(g12)
    c: Coincident(g12,g13)
    c: Coincident(g13,g14)
    c: Horizontal(g14)
    c: Coincident(g14,g15)
    c: Vertical(g15)
    c: Coincident(g15,g16)
    c: Coincident(g16,g17)
    c: Coincident(g17,g18)
    c: Coincident(g18,g19)
    c: Coincident(g19,g20)
    c: Horizontal(g20)
    c: Coincident(g20,g21)
    c: Coincident(g21,g4)
    c: Vertical(g21)
    c: PointOnObject(g22,g6)
    c: PointOnObject(g22,g-15)
    c: Vertical(g22)
    c: Distance(g22) = 4
    c: PointOnObject(g23,g-17)
    c: PointOnObject(g23,g8)
    c: Vertical(g23)
    c: Distance(g23) = 4
    c: Vertical(g9)
    c: PointOnObject(g24,g10)
    c: PointOnObject(g24,g-19)
    c: Vertical(g24)
    c: Distance(g24) = 4
    c: Vertical(g13)
    c: PointOnObject(g25,g-12)
    c: PointOnObject(g25,g12)
    c: Vertical(g25)
    c: Distance(g25) = 4
    c: Symmetric(g14,g14,g26)
    c: PointOnObject(g26,g-10)
    c: Vertical(g26)
    c: Distance(g26) = 4
    c: PointOnObject(g27,g-9)
    c: PointOnObject(g27,g15)
    c: Horizontal(g27)
    c: Distance(g27) = 4
    c: Parallel(g-8,g16)
    c: PointOnObject(g28,g16)
    c: PointOnObject(g28,g-8)
    c: Perpendicular(g16,g28)
    c: Distance(g28) = 4
    c: Parallel(g17,g-7)
    c: Symmetric(g17,g17,g29)
    c: PointOnObject(g29,g-7)
    c: Perpendicular(g17,g29)
    c: Distance(g29) = 4
    c: Parallel(g-5,g19)
    c: Parallel(g-23,g18)
    c: Symmetric(g18,g18,g30)
    c: PointOnObject(g30,g-23)
    c: Perpendicular(g18,g30)
    c: Distance(g30) = 4
    c: PointOnObject(g31,g19)
    c: PointOnObject(g31,g-5)
    c: Perpendicular(g19,g31)
    c: Distance(g31) = 4
    c: PointOnObject(g32,g20)
    c: PointOnObject(g32,g-22)
    c: Vertical(g32)
    c: Distance(g32) = 4
    c: PointOnObject(g33,g-21)
    c: PointOnObject(g33,g21)
    c: Horizontal(g33)
    c: Distance(g33) = 4
    c: Symmetric(g-13,g-13,g34)
    c: PointOnObject(g34,g4)
    c: Vertical(g34)
    c: Distance(g34) = 4
    c: Coincident(g35,g-14)
    c: PointOnObject(g35,g4)
    c: Vertical(g35)
    c: PointOnObject(g36,g5)
    c: PointOnObject(g36,g35)
    c: Horizontal(g36)
    c: Distance(g36) = 4
    c: Coincident(g37,g-16)
    c: Vertical(g37)
    c: PointOnObject(g38,g7)
    c: PointOnObject(g38,g37)
    c: Horizontal(g38)
    c: Distance(g38) = 4
    c: Coincident(g39,g-19)
    c: PointOnObject(g39,g10)
    c: Vertical(g39)
    c: PointOnObject(g40,g9)
    c: PointOnObject(g40,g39)
    c: Horizontal(g40)
    c: Distance(g40) = 4
    c: Coincident(g41,g-20)
    c: PointOnObject(g41,g12)
    c: Vertical(g41)
    c: PointOnObject(g42,g11)
    c: PointOnObject(g42,g41)
    c: Horizontal(g42)
    c: Distance(g42) = 4
    c: Coincident(g43,g-11)
    c: PointOnObject(g43,g14)
    c: Vertical(g43)
    c: PointOnObject(g44,g13)
    c: PointOnObject(g44,g43)
    c: Horizontal(g44)
    c: Distance(g44) = 4
FEATURE [Sketcher::SketchObject] Sketch083
  AttachmentSupport = -> [XY_Plane004]
  FullyConstrained = true
  MapMode = 5
  sketch-geometry (4):
    g0: LineSegment StartX=0 StartY=0 StartZ=0 EndX=14 EndY=0 EndZ=0
    g1: LineSegment StartX=14 StartY=0 StartZ=0 EndX=14 EndY=14 EndZ=0
    g2: LineSegment StartX=14 StartY=14 StartZ=0 EndX=0 EndY=14 EndZ=0
    g3: LineSegment StartX=0 StartY=14 StartZ=0 EndX=0 EndY=0 EndZ=0
  constraints (11):
    c: Coincident(g0,g1)
    c: Coincident(g1,g2)
    c: Coincident(g2,g3)
    c: Coincident(g3,g0)
    c: Horizontal(g0)
    c: Horizontal(g2)
    c: Vertical(g1)
    c: Vertical(g3)
    c: Distance(g1,g3) = 14
    c: Distance(g0,g2) = 14
    c: Coincident(g0,g-1)
FEATURE [PartDesign::Pad] Pad016
  Direction = (0,0,1)
  Length = 5
  Length2 = 10
  Profile = -> Sketch083
  ReferenceAxis = -> Sketch083 [N_Axis]
  Suppressed = false
  Type = 0
FEATURE [Sketcher::SketchObject] Sketch084
  AttachmentSupport = -> [Pad016]
  ExternalGeometry = -> [Pad016]
  FullyConstrained = true
  MapMode = 5
  Placement = pos=(0,0,5) rot=(0,0,1;0rad)
  sketch-geometry (1):
    g0: Circle CenterX=7 CenterY=7 CenterZ=0 NormalX=0 NormalY=0 NormalZ=1 AngleXU=0 Radius=2.3
  constraints (2):
    c: Diameter(g0) = 4.6
    c: Symmetric(g-1,g-3,g0)
FEATURE [PartDesign::Pad] Pad017
  BaseFeature = -> Pad016
  Direction = (0,0,1)
  Length = 4.4
  Length2 = 10
  Profile = -> Sketch084
  ReferenceAxis = -> Sketch084 [N_Axis]
  Suppressed = false
  Type = 0
FEATURE [PartDesign::Fillet] Fillet001
  Base = -> Pad017 [Edge15]
  BaseFeature = -> Pad017
  Radius = 1
  SupportTransform = false
  Suppressed = false
  UseAllEdges = false
FEATURE [Sketcher::SketchObject] Sketch085
  AttachmentSupport = -> [Fillet001]
  ExternalGeometry = -> [Fillet001]
  FullyConstrained = false
  MapMode = 5
  Placement = pos=(0,0,0) rot=(1,0,0;3.14159rad)
  sketch-geometry (8):
    g0: LineSegment StartX=-0.62 StartY=0.62 StartZ=0 EndX=14.62 EndY=0.62 EndZ=0
    g1: LineSegment StartX=14.62 StartY=0.62 StartZ=0 EndX=14.62 EndY=-14.62 EndZ=0
    g2: LineSegment StartX=14.62 StartY=-14.62 StartZ=0 EndX=-0.62 EndY=-14.62 EndZ=0
    g3: LineSegment StartX=-0.62 StartY=-14.62 StartZ=0 EndX=-0.62 EndY=0.62 EndZ=0
    g4: LineSegment StartX=14 StartY=0 StartZ=0 EndX=14.62 EndY=0 EndZ=0
    g5: LineSegment StartX=13.6411 StartY=0 StartZ=0 EndX=13.6411 EndY=0.62 EndZ=0
    g6: LineSegment StartX=0 StartY=-0.426805 StartZ=0 EndX=-0.62 EndY=-0.426805 EndZ=0
    g7: LineSegment StartX=14 StartY=-14 StartZ=0 EndX=14 EndY=-14.62 EndZ=0
  constraints (24):
    c: Horizontal(g0)
    c: Coincident(g0,g1)
    c: Vertical(g1)
    c: Coincident(g1,g2)
    c: Horizontal(g2)
    c: Coincident(g2,g3)
    c: Coincident(g3,g0)
    c: Vertical(g3)
    c: Coincident(g4,g-3)
    c: PointOnObject(g4,g1)
    c: Horizontal(g4)
    c: Distance(g4) = 0.62
    c: PointOnObject(g5,g-1)
    c: PointOnObject(g5,g0)
    c: Vertical(g5)
    c: Distance(g5) = 0.62
    c: PointOnObject(g6,g-2)
    c: PointOnObject(g6,g3)
    c: Horizontal(g6)
    c: Distance(g6) = 0.62
    c: Coincident(g7,g-3)
    c: PointOnObject(g7,g2)
    c: Vertical(g7)
    c: Distance(g7) = 0.62
FEATURE [PartDesign::Pad] Pad018
  BaseFeature = -> Fillet001
  Direction = (0,0,-1)
  Length = 5.8
  Length2 = 10
  Profile = -> Sketch085
  ReferenceAxis = -> Sketch085 [N_Axis]
  Suppressed = false
  Type = 0
FEATURE [Sketcher::SketchObject] Sketch086
  AttachmentSupport = -> [Pad018]
  ExternalGeometry = -> [Pad018]
  FullyConstrained = false
  MapMode = 5
  Placement = pos=(14.62,0,0) rot=(0.57735,0.57735,0.57735;2.0944rad)
  sketch-geometry (7):
    g0: LineSegment StartX=-0.62 StartY=-5.8 StartZ=0 EndX=1.4 EndY=-5.8 EndZ=0
    g1: LineSegment StartX=1.4 StartY=-5.8 StartZ=0 EndX=12.6 EndY=-5.8 EndZ=0
    g2: LineSegment StartX=12.6 StartY=-5.8 StartZ=0 EndX=14.62 EndY=-5.8 EndZ=0
    g3: LineSegment StartX=-0.62 StartY=0 StartZ=0 EndX=1.4 EndY=-5.8 EndZ=0
    g4: LineSegment StartX=-0.62 StartY=0 StartZ=0 EndX=-0.62 EndY=-5.8 EndZ=0
    g5: LineSegment StartX=14.62 StartY=0 StartZ=0 EndX=12.6 EndY=-5.8 EndZ=0
    g6: LineSegment StartX=14.62 StartY=-5.8 StartZ=0 EndX=14.62 EndY=0 EndZ=0
  constraints (14):
    c: Coincident(g0,g1)
    c: Coincident(g1,g2)
    c: Distance(g1) = 11.2
    c: Equal(g2,g0)
    c: Coincident(g2,g-5)
    c: Coincident(g0,g-5)
    c: Coincident(g3,g-4)
    c: Coincident(g3,g0)
    c: Coincident(g4,g3)
    c: Coincident(g4,g0)
    c: Coincident(g5,g-3)
    c: Coincident(g5,g1)
    c: Coincident(g6,g2)
    c: Coincident(g6,g5)
FEATURE [PartDesign::Pocket] Pocket009
  BaseFeature = -> Pad018
  Direction = (-1,0,0)
  Length = 14
  Length2 = 5
  Profile = -> Sketch086
  ReferenceAxis = -> Sketch086 [N_Axis]
  Suppressed = false
  Type = 1
FEATURE [Sketcher::SketchObject] Sketch087
  AttachmentSupport = -> [XZ_Plane004]
  ExternalGeometry = -> [Pocket009]
  FullyConstrained = true
  Placement = pos=(0,-1,0) rot=(1,0,0;1.5708rad)
  sketch-geometry (7):
    g0: LineSegment StartX=12.6 StartY=-5.8 StartZ=0 EndX=14.62 EndY=-5.8 EndZ=0
    g1: LineSegment StartX=-0.62 StartY=-5.8 StartZ=0 EndX=1.4 EndY=-5.8 EndZ=0
    g2: LineSegment StartX=1.4 StartY=-5.8 StartZ=0 EndX=12.6 EndY=-5.8 EndZ=0
    g3: LineSegment StartX=-0.62 StartY=0 StartZ=0 EndX=1.4 EndY=-5.8 EndZ=0
    g4: LineSegment StartX=-0.62 StartY=0 StartZ=0 EndX=-0.62 EndY=-5.8 EndZ=0
    g5: LineSegment StartX=14.62 StartY=0 StartZ=0 EndX=12.6 EndY=-5.8 EndZ=0
    g6: LineSegment StartX=14.62 StartY=-5.8 StartZ=0 EndX=14.62 EndY=0 EndZ=0
  constraints (16):
    c: Coincident(g1,g-5)
    c: Coincident(g0,g-5)
    c: Coincident(g2,g0)
    c: Coincident(g1,g2)
    c: Distance(g2) = 11.2
    c: Equal(g1,g0)
    c: Coincident(g3,g-4)
    c: Coincident(g3,g1)
    c: Coincident(g4,g3)
    c: Coincident(g4,g1)
    c: Coincident(g5,g-3)
    c: Coincident(g5,g0)
    c: Coincident(g6,g0)
    c: Coincident(g6,g5)
    c: Horizontal(g2)
    c: Horizontal(g1)
FEATURE [PartDesign::Pocket] Pocket010
  BaseFeature = -> Pocket009
  Direction = (0,1,-2e-16)
  Length = 5
  Length2 = 5
  Profile = -> Sketch087
  ReferenceAxis = -> Sketch087 [N_Axis]
  Suppressed = false
  Type = 1
FEATURE [Sketcher::SketchObject] Sketch088
  AttachmentSupport = -> [Pocket010]
  FullyConstrained = false
  MapMode = 5
  Placement = pos=(0,0,-5.8) rot=(1,0,0;3.14159rad)
  sketch-geometry (12):
    g0: LineSegment StartX=5.10029 StartY=-6.65195 StartZ=0 EndX=5.10029 EndY=-7.65195 EndZ=0
    g1: LineSegment StartX=6.60029 StartY=-9.15195 StartZ=0 EndX=6.60029 EndY=-7.65195 EndZ=0
    g2: LineSegment StartX=7.60029 StartY=-5.15195 StartZ=0 EndX=7.60029 EndY=-6.65195 EndZ=0
    g3: LineSegment StartX=9.10029 StartY=-7.65195 StartZ=0 EndX=9.10029 EndY=-6.65195 EndZ=0
    g4: LineSegment StartX=5.10029 StartY=-6.65195 StartZ=0 EndX=6.60029 EndY=-6.65195 EndZ=0
    g5: LineSegment StartX=7.60029 StartY=-5.15195 StartZ=0 EndX=6.60029 EndY=-5.15195 EndZ=0
    g6: LineSegment StartX=6.60029 StartY=-9.15195 StartZ=0 EndX=7.60029 EndY=-9.15195 EndZ=0
    g7: LineSegment StartX=9.10029 StartY=-7.65195 StartZ=0 EndX=7.60029 EndY=-7.65195 EndZ=0
    g8: LineSegment StartX=6.60029 StartY=-6.65195 StartZ=0 EndX=6.60029 EndY=-5.15195 EndZ=0
    g9: LineSegment StartX=7.60029 StartY=-6.65195 StartZ=0 EndX=9.10029 EndY=-6.65195 EndZ=0
    g10: LineSegment StartX=7.60029 StartY=-7.65195 StartZ=0 EndX=7.60029 EndY=-9.15195 EndZ=0
    g11: LineSegment StartX=6.60029 StartY=-7.65195 StartZ=0 EndX=5.10029 EndY=-7.65195 EndZ=0
  constraints (12):
    c: Vertical(g0)
    c: Vertical(g1)
    c: Vertical(g2)
    c: Vertical(g3)
    c: Horizontal(g4)
    c: Horizontal(g5)
    c: Horizontal(g6)
    c: Horizontal(g7)
    c: Coincident(g4,g8)
    c: Coincident(g2,g9)
    c: Coincident(g7,g10)
    c: Coincident(g11,g1)
FEATURE [PartDesign::Pad] Pad019
  BaseFeature = -> Pocket010
  Direction = (0,0,-1)
  Length = 3.6
  Length2 = 10
  Profile = -> Sketch088
  ReferenceAxis = -> Sketch088 [N_Axis]
  Suppressed = false
  Type = 0
FEATURE [PartDesign::Fillet] Fillet002
  Base = -> Pad019 [Edge55,Edge53,Edge59,Edge49,Edge47,Edge43,Edge41,Edge38]
  BaseFeature = -> Pad019
  Radius = 0.1
  SupportTransform = false
  Suppressed = false
  UseAllEdges = false
FEATURE [PartDesign::Chamfer] Chamfer
  Angle = 45
  Base = -> Fillet002 [Edge22,Edge21,Edge23,Edge24]
  BaseFeature = -> Fillet002
  ChamferType = 0
  FlipDirection = false
  Size = 1
  Size2 = 1
  SupportTransform = false
  Suppressed = false
  UseAllEdges = false
FEATURE [Sketcher::SketchObject] Sketch089
  AttachmentSupport = -> [Chamfer]
  ExternalGeometry = -> [Chamfer]
  FullyConstrained = false
  MapMode = 5
  Placement = pos=(0,0,5) rot=(0,0,1;0rad)
  sketch-geometry (18):
    g0: LineSegment StartX=0 StartY=14 StartZ=0 EndX=0 EndY=12.4 EndZ=0
    g1: LineSegment StartX=0 StartY=12.4 StartZ=0 EndX=14 EndY=12.4 EndZ=0
    g2: LineSegment StartX=14 StartY=12.4 StartZ=0 EndX=14 EndY=14 EndZ=0
    g3: LineSegment StartX=14 StartY=14 StartZ=0 EndX=0 EndY=14 EndZ=0
    g4: LineSegment StartX=0 StartY=14 StartZ=0 EndX=0 EndY=10 EndZ=0
    g5: LineSegment StartX=0 StartY=10 StartZ=0 EndX=14 EndY=10 EndZ=0
    g6: LineSegment StartX=14 StartY=10 StartZ=0 EndX=14 EndY=14 EndZ=0
    g7: LineSegment StartX=14 StartY=14 StartZ=0 EndX=0 EndY=14 EndZ=0
    g8: LineSegment StartX=14 StartY=14 StartZ=0 EndX=11.5 EndY=14 EndZ=0
    g9: LineSegment StartX=11.5 StartY=14 StartZ=0 EndX=11.5 EndY=0 EndZ=0
    g10: LineSegment StartX=11.5 StartY=0 StartZ=0 EndX=14 EndY=0 EndZ=0
    g11: LineSegment StartX=14 StartY=0 StartZ=0 EndX=14 EndY=14 EndZ=0
    g12: LineSegment StartX=0 StartY=14 StartZ=0 EndX=0 EndY=0 EndZ=0
    g13: LineSegment StartX=0 StartY=0 StartZ=0 EndX=3.5 EndY=0 EndZ=0
    g14: LineSegment StartX=3.5 StartY=0 StartZ=0 EndX=3.5 EndY=14 EndZ=0
    g15: LineSegment StartX=3.5 StartY=14 StartZ=0 EndX=0 EndY=14 EndZ=0
    g16: Circle CenterX=11.4827 CenterY=10 CenterZ=0 NormalX=0 NormalY=0 NormalZ=1 AngleXU=0 Radius=0.25
    g17: Circle CenterX=3.4931 CenterY=12.4 CenterZ=0 NormalX=0 NormalY=0 NormalZ=1 AngleXU=0 Radius=0.25
  constraints (48):
    c: Coincident(g0,g1)
    c: Coincident(g1,g2)
    c: Coincident(g2,g3)
    c: Coincident(g3,g0)
    c: Vertical(g0)
    c: Vertical(g2)
    c: Horizontal(g1)
    c: Horizontal(g3)
    c: Distance(g1,g3) = 1.6
    c: Coincident(g0,g-5)
    c: PointOnObject(g1,g-4)
    c: Coincident(g4,g5)
    c: Coincident(g5,g6)
    c: Coincident(g6,g7)
    c: Coincident(g7,g4)
    c: Vertical(g4)
    c: Vertical(g6)
    c: Horizontal(g5)
    c: Horizontal(g7)
    c: Distance(g5,g7) = 4
    c: Coincident(g4,g0)
    c: PointOnObject(g5,g-4)
    c: Coincident(g8,g9)
    c: Coincident(g9,g10)
    c: Coincident(g10,g11)
    c: Coincident(g11,g8)
    c: Horizontal(g8)
    c: Horizontal(g10)
    c: Vertical(g9)
    c: Vertical(g11)
    c: Distance(g9,g11) = 2.5
    c: Coincident(g8,g2)
    c: PointOnObject(g9,g-1)
    c: Coincident(g12,g13)
    c: Coincident(g13,g14)
    c: Coincident(g14,g15)
    c: Coincident(g15,g12)
    c: Vertical(g12)
    c: Vertical(g14)
    c: Horizontal(g13)
    c: Horizontal(g15)
    c: Distance(g12,g14) = 3.5
    c: Distance(g13,g15) = 14
    c: Coincident(g12,g0)
    c: PointOnObject(g16,g5)
    c: PointOnObject(g17,g1)
    c: Diameter(g17) = 0.5
    c: Diameter(g16) = 0.5
FEATURE [PartDesign::Pad] Pad020
  BaseFeature = -> Chamfer
  Direction = (0,0,1)
  Length = 4
  Length2 = 10
  Profile = -> Sketch089
  ReferenceAxis = -> Sketch089 [N_Axis]
  Suppressed = false
  Type = 0
FEATURE [PartDesign::Body] Body004  label="MXish"
  AllowCompound = false
  Group = -> [Sketch083,Pad016,Sketch084,Pad017,Fillet001,Sketch085,Pad018,Sketch086,Pocket009,Sketch087,Pocket010,Sketch088,Pad019,Fillet002,Chamfer,Sketch089,Pad020]
  Origin = -> Origin004
  Placement = pos=(2,16,8) rot=(1,0,0;3.14159rad)
  Tip = -> Pad020
FEATURE [App::DocumentObjectGroup] Group004  label="Models"
  Group = -> [Body002,xda_keycap,Body004]
FEATURE [Sketcher::SketchObject] Sketch091
  FullyConstrained = false
  MapMode = 5
  Placement = pos=(0,0,-14) rot=(1,0,0;3.14159rad)
  sketch-geometry (4):
    g0: LineSegment StartX=-58.0958 StartY=68.694 StartZ=0 EndX=-58.0958 EndY=-117.755 EndZ=0
    g1: LineSegment StartX=-58.0958 StartY=-117.755 StartZ=0 EndX=201.534 EndY=-117.755 EndZ=0
    g2: LineSegment StartX=201.534 StartY=-117.755 StartZ=0 EndX=201.534 EndY=68.694 EndZ=0
    g3: LineSegment StartX=201.534 StartY=68.694 StartZ=0 EndX=-58.0958 EndY=68.694 EndZ=0
  constraints (8):
    c: Coincident(g0,g1)
    c: Coincident(g1,g2)
    c: Coincident(g2,g3)
    c: Coincident(g3,g0)
    c: Vertical(g0)
    c: Vertical(g2)
    c: Horizontal(g1)
    c: Horizontal(g3)
FEATURE [PartDesign::Pocket] Pocket011  label="RebajeBorde"
  BaseFeature = -> Pocket007
  Direction = (0,0,1)
  Length = 9.4
  Length2 = 5
  Placement = pos=(0,0,6) rot=(0,0,1;0rad)
  Profile = -> Sketch091
  ReferenceAxis = -> Sketch091 [N_Axis]
  Suppressed = false
  Type = 0
FEATURE [Sketcher::SketchObject] Sketch092
  AttachmentOffset = pos=(0,0,-1.5) rot=(0,0,1;0rad)
  AttachmentSupport = -> [Pocket011]
  ExternalGeometry = -> [Sketch059,Pocket011]
  FullyConstrained = false
  MapMode = 5
  Placement = pos=(0,0,4.9) rot=(1,0,0;3.14159rad)
  sketch-geometry (5):
    g0: LineSegment StartX=134.627 StartY=-9 StartZ=0 EndX=136.827 EndY=-9 EndZ=0
    g1: LineSegment StartX=136.827 StartY=-2 StartZ=0 EndX=134.627 EndY=-2 EndZ=0
    g2: LineSegment StartX=134.627 StartY=-2 StartZ=0 EndX=134.627 EndY=-9 EndZ=0
    g3: LineSegment StartX=136.827 StartY=-9 StartZ=0 EndX=136.827 EndY=-2 EndZ=0
    g4: LineSegment StartX=134.627 StartY=-9 StartZ=0 EndX=134.627 EndY=-59.5 EndZ=0
  constraints (14):
    c: Coincident(g1,g2)
    c: Coincident(g2,g0)
    c: Horizontal(g0)
    c: Horizontal(g1)
    c: Vertical(g2)
    c: Distance(g0) = 2.2
    c: Coincident(g3,g0)
    c: Coincident(g3,g1)
    c: Vertical(g3)
    c: Coincident(g4,g0)
    c: PointOnObject(g4,g-4)
    c: Vertical(g4)
    c: Distance(g4) = 50.5
    c: Distance(g3) = 7
FEATURE [Sketcher::SketchObject] MirroredSketch005  label="PCB.Borders002"
  AttachmentSupport = -> [XY_Plane005]
  FullyConstrained = true
  MapMode = 5
  expr: Constraints[41] = Spreadsheet.PCBBorderRadius
  expr: Constraints[44] = Spreadsheet.PCBBorderRadius
  expr: Constraints[47] = Spreadsheet.PCBBorderRadius
  expr: Constraints[52] = Spreadsheet.PCBBorderRadius
  expr: Constraints[53] = Spreadsheet.PCBBorderRadius
  expr: Constraints[56] = Spreadsheet.PCBBorderRadius
  expr: Constraints[59] = Spreadsheet.PCBBorderRadius
  expr: Constraints[62] = Spreadsheet.PCBBorderRadius
  expr: Constraints[65] = Spreadsheet.PCBBorderRadius
  expr: Constraints[68] = Spreadsheet.PCBBorderRadius
  expr: Constraints[74] = Spreadsheet.PCBBorderRadius
  expr: Constraints[79] = Spreadsheet.PCBBorderRadius
  expr: Constraints[86] = Spreadsheet.PCBSmallStep
  expr: Constraints[87] = Spreadsheet.PCBSmallStep
  expr: Constraints[88] = Spreadsheet.PCBSmallStep
  expr: Constraints[89] = Spreadsheet.PCBSmallStep
  expr: Constraints[90] = Spreadsheet.PCBBigStep
  sketch-geometry (38):
    g0: LineSegment StartX=0 StartY=56.25 StartZ=0 EndX=0 EndY=0.632 EndZ=0
    g1: LineSegment StartX=0.632 StartY=0 StartZ=0 EndX=55.6983 EndY=0 EndZ=0
    g2: LineSegment StartX=55.6983 StartY=0 StartZ=0 EndX=66.4243 EndY=-14.7035 EndZ=0
    g3: LineSegment StartX=66.4243 StartY=-14.7035 StartZ=0 EndX=103.928 EndY=-19.5811 EndZ=0
    g4: LineSegment StartX=103.928 StartY=-19.5811 StartZ=0 EndX=118.437 EndY=-27.9743 EndZ=0
    g5: LineSegment StartX=120.31 StartY=-27.472 StartZ=0 EndX=133.73 EndY=-4.162 EndZ=0
    g6: LineSegment StartX=133.73 StartY=-4.162 StartZ=0 EndX=133.73 EndY=55.868 EndZ=0
    g7: LineSegment StartX=133.098 StartY=56.5 StartZ=0 EndX=113.612 EndY=56.5 EndZ=0
    g8: LineSegment StartX=112.98 StartY=57.132 StartZ=0 EndX=112.98 EndY=58.118 EndZ=0
    g9: LineSegment StartX=112.348 StartY=58.75 StartZ=0 EndX=94.612 EndY=58.75 EndZ=0
    g10: LineSegment StartX=93.98 StartY=59.382 StartZ=0 EndX=93.98 EndY=60.368 EndZ=0
    g11: LineSegment StartX=93.348 StartY=61 StartZ=0 EndX=75.612 EndY=61 EndZ=0
    g12: LineSegment StartX=74.98 StartY=61.632 StartZ=0 EndX=74.98 EndY=62.618 EndZ=0
    g13: LineSegment StartX=74.348 StartY=63.25 StartZ=0 EndX=57.612 EndY=63.25 EndZ=0
    g14: LineSegment StartX=56.98 StartY=62.618 StartZ=0 EndX=56.98 EndY=61.632 EndZ=0
    g15: LineSegment StartX=56.348 StartY=61 StartZ=0 EndX=38.612 EndY=61 EndZ=0
    g16: LineSegment StartX=37.98 StartY=60.368 StartZ=0 EndX=37.98 EndY=56.882 EndZ=0
    g17: LineSegment StartX=37.348 StartY=56.25 StartZ=0 EndX=0 EndY=56.25 EndZ=0
    g18: Circle CenterX=18.61 CenterY=37.51 CenterZ=0 NormalX=0 NormalY=0 NormalZ=1 AngleXU=0 Radius=2.15
    g19: Circle CenterX=18.6 CenterY=18.76 CenterZ=0 NormalX=0 NormalY=0 NormalZ=1 AngleXU=0 Radius=2.15
    g20: Circle CenterX=108.3 CenterY=-6.24 CenterZ=0 NormalX=0 NormalY=0 NormalZ=1 AngleXU=0 Radius=2.15
    g21: Circle CenterX=94.55 CenterY=41.5 CenterZ=0 NormalX=0 NormalY=0 NormalZ=1 AngleXU=0 Radius=2.15
    g22: Circle CenterX=61.84 CenterY=1.51 CenterZ=0 NormalX=0 NormalY=0 NormalZ=1 AngleXU=0 Radius=2.15
    g23: ArcOfCircle CenterX=37.348 CenterY=56.882 CenterZ=0 NormalX=0 NormalY=0 NormalZ=1 AngleXU=0 Radius=0.632 StartAngle=4.71239 EndAngle=6.28319
    g24: ArcOfCircle CenterX=56.348 CenterY=61.632 CenterZ=0 NormalX=0 NormalY=0 NormalZ=1 AngleXU=0 Radius=0.632 StartAngle=4.71239 EndAngle=6.28319
    g25: ArcOfCircle CenterX=75.612 CenterY=61.632 CenterZ=0 NormalX=0 NormalY=0 NormalZ=1 AngleXU=0 Radius=0.632 StartAngle=3.14159 EndAngle=4.71239
    g26: ArcOfCircle CenterX=57.612 CenterY=62.618 CenterZ=0 NormalX=0 NormalY=0 NormalZ=1 AngleXU=0 Radius=0.632 StartAngle=1.5708 EndAngle=3.14159
    g27: ArcOfCircle CenterX=74.348 CenterY=62.618 CenterZ=0 NormalX=0 NormalY=0 NormalZ=1 AngleXU=0 Radius=0.632 StartAngle=5e-15 EndAngle=1.5708
    g28: ArcOfCircle CenterX=93.348 CenterY=60.368 CenterZ=0 NormalX=0 NormalY=0 NormalZ=1 AngleXU=0 Radius=0.632 StartAngle=-9e-16 EndAngle=1.5708
    g29: ArcOfCircle CenterX=94.612 CenterY=59.382 CenterZ=0 NormalX=0 NormalY=0 NormalZ=1 AngleXU=0 Radius=0.632 StartAngle=3.14159 EndAngle=4.71239
    g30: ArcOfCircle CenterX=112.348 CenterY=58.118 CenterZ=0 NormalX=0 NormalY=0 NormalZ=1 AngleXU=0 Radius=0.632 StartAngle=-9e-16 EndAngle=1.5708
    g31: ArcOfCircle CenterX=113.612 CenterY=57.132 CenterZ=0 NormalX=0 NormalY=0 NormalZ=1 AngleXU=0 Radius=0.632 StartAngle=3.14159 EndAngle=4.71239
    g32: ArcOfCircle CenterX=133.098 CenterY=55.868 CenterZ=0 NormalX=0 NormalY=0 NormalZ=1 AngleXU=0 Radius=0.632 StartAngle=-5.3e-15 EndAngle=1.5708
    g33: ArcOfCircle CenterX=119.123 CenterY=-26.7885 CenterZ=0 NormalX=0 NormalY=0 NormalZ=1 AngleXU=0 Radius=1.37 StartAngle=4.18792 EndAngle=5.76081
    g34: ArcOfCircle CenterX=0.632 CenterY=0.632 CenterZ=0 NormalX=0 NormalY=0 NormalZ=1 AngleXU=0 Radius=0.632 StartAngle=3.14159 EndAngle=4.71239
    g35: ArcOfCircle CenterX=38.612 CenterY=60.368 CenterZ=0 NormalX=0 NormalY=0 NormalZ=1 AngleXU=0 Radius=0.632 StartAngle=1.5708 EndAngle=3.14159
    g36: LineSegment StartX=122.07 StartY=-24.4153 StartZ=0 EndX=119.625 EndY=-28.6618 EndZ=0
    g37: LineSegment StartX=116.44 StartY=-26.819 StartZ=0 EndX=119.625 EndY=-28.6618 EndZ=0
  constraints (102):
    c: Horizontal(g1)
    c: Vertical(g0)
    c: Coincident(g1,g2)
    c: Coincident(g2,g3)
    c: Coincident(g3,g4)
    c: Coincident(g5,g6)
    c: Coincident(g17,g0)
    c: Vertical(g6)
    c: Horizontal(g7)
    c: Horizontal(g9)
    c: Horizontal(g11)
    c: Horizontal(g13)
    c: Horizontal(g15)
    c: Horizontal(g17)
    c: Vertical(g16)
    c: Vertical(g14)
    c: Vertical(g12)
    c: Vertical(g10)
    c: Vertical(g8)
    c: Angle(g5,g6) = -2.61922
    c: Angle(g4,g5) = -1.5687
    c: Angle(g4,g3) = -2.74645
    c: Angle(g2,g3) = -2.33036
    c: Diameter(g20) = 4.3
    c: Diameter(g21) = 4.3
    c: Diameter(g18) = 4.3
    c: Diameter(g19) = 4.3
    c: Distance(g18,g0) = 18.61
    c: Distance(g19,g18) = 18.75
    c: Distance(g19,g0) = 18.6
    c: Distance(g21,g6) = 39.18
    c: Distance(g21,g9) = 17.25
    c: Distance(g20,g6) = 25.43
    c: Distance(g3) = 37.82
    c: Distance(g19,g1) = 18.76
    c: Diameter(g22) = 4.3
    c: DistanceX(g19,g22) = 43.24
    c: DistanceY(g22,g19) = 17.25
    c: DistanceY(g20,g22) = 7.75
    c: Tangent(g16,g23) = 1.5708
    c: Tangent(g17,g23) = 1.5708
    c: Radius(g23) = 0.632
    c: Tangent(g14,g24) = 1.5708
    c: Tangent(g15,g24) = 1.5708
    c: Radius(g24) = 0.632
    c: Tangent(g12,g25) = 1.5708
    c: Tangent(g11,g25) = 1.5708
    c: Radius(g25) = 0.632
    c: Tangent(g13,g26) = -1.5708
    c: Tangent(g14,g26) = -1.5708
    c: Tangent(g13,g27) = -1.5708
    c: Tangent(g12,g27) = -1.5708
    c: Radius(g26) = 0.632
    c: Radius(g27) = 0.632
    c: Tangent(g11,g28) = -1.5708
    c: Tangent(g10,g28) = -1.5708
    c: Radius(g28) = 0.632
    c: Tangent(g10,g29) = 1.5708
    c: Tangent(g9,g29) = 1.5708
    c: Radius(g29) = 0.632
    c: Tangent(g9,g30) = -1.5708
    c: Tangent(g8,g30) = -1.5708
    c: Radius(g30) = 0.632
    c: Tangent(g8,g31) = 1.5708
    c: Tangent(g7,g31) = 1.5708
    c: Radius(g31) = 0.632
    c: Tangent(g7,g32) = -1.5708
    c: Tangent(g6,g32) = -1.5708
    c: Radius(g32) = 0.632
    c: Tangent(g5,g33) = -1.5708
    c: Tangent(g4,g33) = -1.5708
    c: Radius(g33) = 1.37
    c: Tangent(g1,g34) = -1.5708
    c: Tangent(g0,g34) = -1.5708
    c: Radius(g34) = 0.632
    c: DistanceY(g-1,g1) = 0
    c: DistanceX(g-2,g0) = 0
    c: Tangent(g15,g35) = -1.5708
    c: Tangent(g16,g35) = -1.5708
    c: Radius(g35) = 0.632
    c: Distance(g16,g0) = 37.98
    c: Distance(g14,g16) = 19
    c: Distance(g14,g12) = 18
    c: Distance(g10,g12) = 19
    c: Distance(g10,g8) = 19
    c: Distance(g6,g8) = 20.75
    c: Distance(g7,g9) = 2.25
    c: Distance(g9,g11) = 2.25
    c: Distance(g11,g13) = 2.25
    c: Distance(g15,g13) = 2.25
    c: Distance(g15,g17) = 4.75
    c: Distance(g1,g17) = 56.25
    c: Distance(g2) = 18.2
    c: DistanceY(g6,g6) = 60.03
    c: PointOnObject(g36,g5)
    c: Tangent(g36,g33)
    c: PointOnObject(g37,g4)
    c: Tangent(g37,g33)
    c: Coincident(g36,g37)
    c: Distance(g5,g36) = 28.27
    c: Distance(g36) = 4.9
    c: Distance(g37) = 3.68
FEATURE [PartDesign::Pad] Pad021
  Direction = (0,0,1)
  Length = 1.4
  Length2 = 10
  Profile = -> MirroredSketch005
  ReferenceAxis = -> MirroredSketch005 [N_Axis]
  Suppressed = false
  Type = 0
FEATURE [Sketcher::SketchObject] Sketch093
  AttachmentSupport = -> [Pad021]
  ExternalGeometry = -> [Pad021]
  FullyConstrained = false
  MapMode = 5
  Placement = pos=(0,0,1.4) rot=(0,0,1;0rad)
  sketch-geometry (78):
    g0: Circle CenterX=131.63 CenterY=53.8 CenterZ=0 NormalX=0 NormalY=0 NormalZ=1 AngleXU=0 Radius=0.7
    g1: LineSegment StartX=131.63 StartY=56.5 StartZ=0 EndX=131.63 EndY=54.5 EndZ=0
    g2: LineSegment StartX=133.73 StartY=53.8 StartZ=0 EndX=132.33 EndY=53.8 EndZ=0
    g3: LineSegment StartX=131.63 StartY=53.8 StartZ=0 EndX=131.63 EndY=52.4 EndZ=0
    g4: LineSegment StartX=131.63 StartY=52.4 StartZ=0 EndX=131.63 EndY=51.7 EndZ=0
    g5: Circle CenterX=131.63 CenterY=51.7 CenterZ=0 NormalX=0 NormalY=0 NormalZ=1 AngleXU=0 Radius=0.7
    g6: LineSegment StartX=131.63 StartY=51.7 StartZ=0 EndX=131.63 EndY=50.3 EndZ=0
    g7: LineSegment StartX=131.63 StartY=50.3 StartZ=0 EndX=131.63 EndY=49.6 EndZ=0
    g8: LineSegment StartX=131.63 StartY=49.6 StartZ=0 EndX=131.63 EndY=48.2 EndZ=0
    g9: LineSegment StartX=131.63 StartY=48.2 StartZ=0 EndX=131.63 EndY=47.5 EndZ=0
    g10: LineSegment StartX=131.63 StartY=47.5 StartZ=0 EndX=131.63 EndY=46.1 EndZ=0
    g11: LineSegment StartX=131.63 StartY=46.1 StartZ=0 EndX=131.63 EndY=45.4 EndZ=0
    g12: LineSegment StartX=131.63 StartY=45.4 StartZ=0 EndX=131.63 EndY=44 EndZ=0
    g13: LineSegment StartX=131.63 StartY=44 StartZ=0 EndX=131.63 EndY=43.3 EndZ=0
    g14: LineSegment StartX=131.63 StartY=43.3 StartZ=0 EndX=131.63 EndY=41.9 EndZ=0
    g15: LineSegment StartX=131.63 StartY=41.9 StartZ=0 EndX=131.63 EndY=41.2 EndZ=0
    g16: LineSegment StartX=131.63 StartY=41.2 StartZ=0 EndX=131.63 EndY=39.8 EndZ=0
    g17: LineSegment StartX=131.63 StartY=39.8 StartZ=0 EndX=131.63 EndY=39.1 EndZ=0
    g18: Circle CenterX=131.63 CenterY=49.6 CenterZ=0 NormalX=0 NormalY=0 NormalZ=1 AngleXU=0 Radius=0.7
    g19: Circle CenterX=131.63 CenterY=47.5 CenterZ=0 NormalX=0 NormalY=0 NormalZ=1 AngleXU=0 Radius=0.7
    g20: Circle CenterX=131.63 CenterY=45.4 CenterZ=0 NormalX=0 NormalY=0 NormalZ=1 AngleXU=0 Radius=0.7
    g21: Circle CenterX=131.63 CenterY=43.3 CenterZ=0 NormalX=0 NormalY=0 NormalZ=1 AngleXU=0 Radius=0.7
    g22: Circle CenterX=131.63 CenterY=41.2 CenterZ=0 NormalX=0 NormalY=0 NormalZ=1 AngleXU=0 Radius=0.7
    g23: Circle CenterX=131.63 CenterY=39.1 CenterZ=0 NormalX=0 NormalY=0 NormalZ=1 AngleXU=0 Radius=0.7
    g24: LineSegment StartX=131.63 StartY=37 StartZ=0 EndX=131.63 EndY=35.6 EndZ=0
    g25: LineSegment StartX=131.63 StartY=35.6 StartZ=0 EndX=131.63 EndY=34.9 EndZ=0
    g26: LineSegment StartX=131.63 StartY=34.9 StartZ=0 EndX=131.63 EndY=33.5 EndZ=0
    g27: LineSegment StartX=131.63 StartY=33.5 StartZ=0 EndX=131.63 EndY=32.8 EndZ=0
    g28: LineSegment StartX=131.63 StartY=32.8 StartZ=0 EndX=131.63 EndY=31.4 EndZ=0
    g29: LineSegment StartX=131.63 StartY=31.4 StartZ=0 EndX=131.63 EndY=30.7 EndZ=0
    g30: LineSegment StartX=131.63 StartY=30.7 StartZ=0 EndX=131.63 EndY=29.3 EndZ=0
    g31: LineSegment StartX=131.63 StartY=29.3 StartZ=0 EndX=131.63 EndY=28.6 EndZ=0
    g32: LineSegment StartX=131.63 StartY=39.1 StartZ=0 EndX=131.63 EndY=37.7 EndZ=0
    g33: LineSegment StartX=131.63 StartY=37.7 StartZ=0 EndX=131.63 EndY=37 EndZ=0
    g34: Circle CenterX=131.63 CenterY=37 CenterZ=0 NormalX=0 NormalY=0 NormalZ=1 AngleXU=0 Radius=0.7
    g35: Circle CenterX=131.63 CenterY=34.9 CenterZ=0 NormalX=0 NormalY=0 NormalZ=1 AngleXU=0 Radius=0.7
    g36: Circle CenterX=131.63 CenterY=32.8 CenterZ=0 NormalX=0 NormalY=0 NormalZ=1 AngleXU=0 Radius=0.7
    g37: Circle CenterX=131.63 CenterY=30.7 CenterZ=0 NormalX=0 NormalY=0 NormalZ=1 AngleXU=0 Radius=0.7
    g38: Circle CenterX=131.63 CenterY=28.6 CenterZ=0 NormalX=0 NormalY=0 NormalZ=1 AngleXU=0 Radius=0.7
    g39: LineSegment StartX=131.63 StartY=53.8 StartZ=0 EndX=117.63 EndY=53.8 EndZ=0
    g40: Circle CenterX=117.63 CenterY=53.8 CenterZ=0 NormalX=0 NormalY=0 NormalZ=1 AngleXU=0 Radius=0.644462
    g41: LineSegment StartX=117.63 StartY=53.8 StartZ=0 EndX=117.63 EndY=52.4 EndZ=0
    g42: LineSegment StartX=117.63 StartY=52.4 StartZ=0 EndX=117.63 EndY=51.7 EndZ=0
    g43: LineSegment StartX=117.63 StartY=51.7 StartZ=0 EndX=117.63 EndY=50.3 EndZ=0
    g44: LineSegment StartX=117.63 StartY=50.3 StartZ=0 EndX=117.63 EndY=49.6 EndZ=0
    g45: LineSegment StartX=117.63 StartY=49.6 StartZ=0 EndX=117.63 EndY=48.2 EndZ=0
    g46: Circle CenterX=117.63 CenterY=51.7 CenterZ=0 NormalX=0 NormalY=0 NormalZ=1 AngleXU=0 Radius=0.7
    g47: Circle CenterX=117.63 CenterY=49.6 CenterZ=0 NormalX=0 NormalY=0 NormalZ=1 AngleXU=0 Radius=0.7
    g48: LineSegment StartX=117.63 StartY=48.2 StartZ=0 EndX=117.63 EndY=47.5 EndZ=0
    g49: LineSegment StartX=117.63 StartY=47.5 StartZ=0 EndX=117.63 EndY=46.1 EndZ=0
    g50: LineSegment StartX=117.63 StartY=46.1 StartZ=0 EndX=117.63 EndY=45.4 EndZ=0
    g51: LineSegment StartX=117.63 StartY=45.4 StartZ=0 EndX=117.63 EndY=44 EndZ=0
    g52: LineSegment StartX=117.63 StartY=44 StartZ=0 EndX=117.63 EndY=43.3 EndZ=0
    g53: LineSegment StartX=117.63 StartY=43.3 StartZ=0 EndX=117.63 EndY=41.9 EndZ=0
    g54: LineSegment StartX=117.63 StartY=41.9 StartZ=0 EndX=117.63 EndY=41.2 EndZ=0
    g55: Circle CenterX=117.63 CenterY=47.5 CenterZ=0 NormalX=0 NormalY=0 NormalZ=1 AngleXU=0 Radius=0.7
    g56: Circle CenterX=117.63 CenterY=45.4 CenterZ=0 NormalX=0 NormalY=0 NormalZ=1 AngleXU=0 Radius=0.7
    g57: Circle CenterX=117.63 CenterY=43.3 CenterZ=0 NormalX=0 NormalY=0 NormalZ=1 AngleXU=0 Radius=0.7
    g58: Circle CenterX=117.63 CenterY=41.2 CenterZ=0 NormalX=0 NormalY=0 NormalZ=1 AngleXU=0 Radius=0.7
    g59: LineSegment StartX=117.63 StartY=41.2 StartZ=0 EndX=117.63 EndY=39.8 EndZ=0
    g60: LineSegment StartX=117.63 StartY=39.8 StartZ=0 EndX=117.63 EndY=39.1 EndZ=0
    g61: LineSegment StartX=117.63 StartY=39.1 StartZ=0 EndX=117.63 EndY=37.7 EndZ=0
    g62: LineSegment StartX=117.63 StartY=37.7 StartZ=0 EndX=117.63 EndY=37 EndZ=0
    g63: LineSegment StartX=117.63 StartY=37 StartZ=0 EndX=117.63 EndY=35.6 EndZ=0
    g64: LineSegment StartX=117.63 StartY=35.6 StartZ=0 EndX=117.63 EndY=34.9 EndZ=0
    g65: LineSegment StartX=117.63 StartY=34.9 StartZ=0 EndX=117.63 EndY=33.5 EndZ=0
    g66: LineSegment StartX=117.63 StartY=33.5 StartZ=0 EndX=117.63 EndY=32.8 EndZ=0
    g67: LineSegment StartX=117.63 StartY=32.8 StartZ=0 EndX=117.63 EndY=31.4 EndZ=0
    g68: LineSegment StartX=117.63 StartY=31.4 StartZ=0 EndX=117.63 EndY=30.7 EndZ=0
    g69: LineSegment StartX=117.63 StartY=30.7 StartZ=0 EndX=117.63 EndY=29.3 EndZ=0
    g70: Circle CenterX=117.63 CenterY=39.1 CenterZ=0 NormalX=0 NormalY=0 NormalZ=1 AngleXU=0 Radius=0.7
    g71: Circle CenterX=117.63 CenterY=37 CenterZ=0 NormalX=0 NormalY=0 NormalZ=1 AngleXU=0 Radius=0.7
    g72: Circle CenterX=117.63 CenterY=34.8681 CenterZ=0 NormalX=0 NormalY=0 NormalZ=1 AngleXU=0 Radius=0.731859
    g73: Circle CenterX=117.63 CenterY=32.8 CenterZ=0 NormalX=0 NormalY=0 NormalZ=1 AngleXU=0 Radius=0.7
    g74: LineSegment StartX=117.63 StartY=29.3 StartZ=0 EndX=117.63 EndY=28.6 EndZ=0
    g75: LineSegment StartX=117.63 StartY=28.6 StartZ=0 EndX=117.63 EndY=27.2 EndZ=0
    g76: Circle CenterX=117.63 CenterY=30.7 CenterZ=0 NormalX=0 NormalY=0 NormalZ=1 AngleXU=0 Radius=0.7
    g77: Circle CenterX=117.63 CenterY=28.6 CenterZ=0 NormalX=0 NormalY=0 NormalZ=1 AngleXU=0 Radius=0.7
  constraints (210):
    c: Distance(g1) = 2
    c: Vertical(g1)
    c: PointOnObject(g1,g-3)
    c: Diameter(g0) = 1.4
    c: PointOnObject(g1,g0)
    c: PointOnObject(g2,g-4)
    c: PointOnObject(g2,g0)
    c: Horizontal(g2)
    c: Distance(g2) = 1.4
    c: Vertical(g1,g0)
    c: Horizontal(g2,g0)
    c: Distance(g3) = 1.4
    c: Coincident(g3,g0)
    c: Vertical(g3)
    c: Distance(g4) = 0.7
    c: Coincident(g4,g3)
    c: Vertical(g4)
    c: Coincident(g5,g4)
    c: PointOnObject(g3,g5)
    c: Coincident(g6,g4)
    c: Coincident(g6,g7)
    c: Vertical(g6)
    c: Coincident(g7,g8)
    c: Vertical(g7)
    c: Coincident(g8,g9)
    c: Vertical(g8)
    c: Coincident(g9,g10)
    c: Vertical(g9)
    c: Coincident(g10,g11)
    c: Vertical(g10)
    c: Coincident(g11,g12)
    c: Vertical(g11)
    c: Coincident(g12,g13)
    c: Vertical(g12)
    c: Coincident(g13,g14)
    c: Vertical(g13)
    c: Coincident(g14,g15)
    c: Vertical(g14)
    c: Coincident(g15,g16)
    c: Vertical(g15)
    c: Coincident(g16,g17)
    c: Vertical(g16)
    c: Vertical(g17)
    c: Distance(g6) = 1.4
    c: Distance(g7) = 0.7
    c: Distance(g8) = 1.4
    c: Distance(g9) = 0.7
    c: Distance(g10) = 1.4
    c: Distance(g11) = 0.7
    c: Distance(g12) = 1.4
    c: Distance(g13) = 0.7
    c: Distance(g14) = 1.4
    c: Distance(g15) = 0.7
    c: Distance(g16) = 1.4
    c: Distance(g17) = 0.7
    c: Coincident(g18,g7)
    c: Coincident(g19,g9)
    c: PointOnObject(g8,g19)
    c: Coincident(g20,g11)
    c: PointOnObject(g10,g20)
    c: Coincident(g21,g13)
    c: PointOnObject(g12,g21)
    c: Coincident(g22,g15)
    c: PointOnObject(g14,g22)
    c: Coincident(g23,g17)
    c: PointOnObject(g16,g23)
    c: PointOnObject(g6,g18)
    c: Coincident(g24,g25)
    c: Vertical(g24)
    c: Coincident(g25,g26)
    c: Vertical(g25)
    c: Coincident(g26,g27)
    c: Vertical(g26)
    c: Coincident(g27,g28)
    c: Vertical(g27)
    c: Coincident(g28,g29)
    c: Vertical(g28)
    c: Coincident(g29,g30)
    c: Vertical(g29)
    c: Coincident(g30,g31)
    c: Vertical(g30)
    c: Vertical(g31)
    c: Distance(g32) = 1.4
    c: Coincident(g33,g32)
    c: Coincident(g33,g24)
    c: Vertical(g33)
    c: Distance(g33) = 0.7
    c: Distance(g24) = 1.4
    c: Distance(g26) = 1.4
    c: Distance(g25) = 0.7
    c: Distance(g27) = 0.7
    c: Distance(g28) = 1.4
    c: Distance(g29) = 0.7
    c: Distance(g30) = 1.4
    c: Distance(g31) = 0.7
    c: Coincident(g32,g17)
    c: Vertical(g32)
    c: Coincident(g34,g24)
    c: PointOnObject(g32,g34)
    c: Coincident(g35,g25)
    c: PointOnObject(g24,g35)
    c: Coincident(g36,g27)
    c: PointOnObject(g26,g36)
    c: Coincident(g37,g29)
    c: PointOnObject(g28,g37)
    c: Coincident(g38,g31)
    c: PointOnObject(g30,g38)
    c: Distance(g39) = 14
    c: Coincident(g39,g0)
    c: Horizontal(g39)
    c: Coincident(g40,g39)
    c: Distance(g41) = 1.4
    c: Coincident(g41,g39)
    c: Vertical(g41)
    c: Distance(g42) = 0.7
    c: Coincident(g42,g41)
    c: Vertical(g42)
    c: Distance(g43) = 1.4
    c: Coincident(g43,g42)
    c: Vertical(g43)
    c: Distance(g44) = 0.7
    c: Coincident(g44,g43)
    c: Vertical(g44)
    c: Distance(g45) = 1.4
    c: Coincident(g45,g44)
    c: Vertical(g45)
    c: Coincident(g46,g42)
    c: PointOnObject(g41,g46)
    c: Coincident(g47,g44)
    c: PointOnObject(g43,g47)
    c: Coincident(g48,g45)
    c: Coincident(g48,g49)
    c: Distance(g48,g75) = 21
    c: Vertical(g48)
    c: Coincident(g49,g50)
    c: Vertical(g49)
    c: Coincident(g50,g51)
    c: Vertical(g50)
    c: Coincident(g51,g52)
    c: Vertical(g51)
    c: Coincident(g52,g53)
    c: Vertical(g52)
    c: Coincident(g53,g54)
    c: Vertical(g53)
    c: Coincident(g54,g59)
    c: Vertical(g54)
    c: Distance(g48) = 0.7
    c: Distance(g49) = 1.4
    c: Distance(g50) = 0.7
    c: Distance(g51) = 1.4
    c: Distance(g52) = 0.7
    c: Distance(g53) = 1.4
    c: Distance(g54) = 0.7
    c: Coincident(g55,g48)
    c: PointOnObject(g45,g55)
    c: Coincident(g56,g50)
    c: PointOnObject(g49,g56)
    c: Coincident(g57,g52)
    c: PointOnObject(g51,g57)
    c: Coincident(g58,g54)
    c: PointOnObject(g53,g58)
    c: Coincident(g59,g60)
    c: Vertical(g59)
    c: Coincident(g60,g61)
    c: Vertical(g60)
    c: Coincident(g61,g62)
    c: Vertical(g61)
    c: Coincident(g62,g63)
    c: Vertical(g62)
    c: Coincident(g63,g64)
    c: Vertical(g63)
    c: Coincident(g64,g65)
    c: Vertical(g64)
    c: Coincident(g65,g66)
    c: Vertical(g65)
    c: Coincident(g66,g67)
    c: Vertical(g66)
    c: Coincident(g67,g68)
    c: Vertical(g67)
    c: Coincident(g68,g69)
    c: Vertical(g68)
    c: Coincident(g69,g74)
    c: Vertical(g69)
    c: Distance(g59) = 1.4
    c: Distance(g60) = 0.7
    c: Distance(g61) = 1.4
    c: Distance(g62) = 0.7
    c: Distance(g63) = 1.4
    c: Distance(g64) = 0.7
    c: Distance(g65) = 1.4
    c: Distance(g66) = 0.7
    c: Coincident(g70,g60)
    c: PointOnObject(g59,g70)
    c: Coincident(g71,g62)
    c: PointOnObject(g61,g71)
    c: PointOnObject(g72,g65)
    c: PointOnObject(g63,g72)
    c: Coincident(g73,g66)
    c: PointOnObject(g65,g73)
    c: Distance(g67) = 1.4
    c: Distance(g68) = 0.7
    c: Distance(g69) = 1.4
    c: Coincident(g74,g75)
    c: Vertical(g74)
    c: Vertical(g75)
    c: Distance(g74) = 0.7
    c: Coincident(g76,g68)
    c: PointOnObject(g67,g76)
    c: Coincident(g77,g74)
    c: PointOnObject(g69,g77)
FEATURE [PartDesign::Pocket] Pocket013  label="NiceNano"
  BaseFeature = -> Pad021
  Direction = (0,0,-1)
  Length = 5
  Length2 = 5
  Profile = -> Sketch093
  ReferenceAxis = -> Sketch093 [N_Axis]
  Suppressed = false
  Type = 1
FEATURE [Sketcher::SketchObject] Sketch094
  AttachmentSupport = -> [Pad]
  ExternalGeometry = -> [Sketch059]
  FullyConstrained = false
  MapMode = 5
  Placement = pos=(0,0,6) rot=(1,0,0;3.14159rad)
  sketch-geometry (6):
    g0: LineSegment StartX=113.98 StartY=-0.896746 StartZ=0 EndX=113.98 EndY=-57.5 EndZ=0
    g1: LineSegment StartX=113.98 StartY=-57.5 StartZ=0 EndX=134.135 EndY=-57.5 EndZ=0
    g2: LineSegment StartX=134.726 StartY=-56.9095 StartZ=0 EndX=134.726 EndY=-0.896746 EndZ=0
    g3: LineSegment StartX=134.726 StartY=-0.896746 StartZ=0 EndX=113.98 EndY=-0.896746 EndZ=0
    g4: ArcOfCircle CenterX=134.135 CenterY=-56.9095 CenterZ=0 NormalX=0 NormalY=0 NormalZ=1 AngleXU=0 Radius=0.590469 StartAngle=4.71239 EndAngle=6.28319
    g5: GeomPoint X=134.726 Y=-57.5 Z=0
  constraints (12):
    c: Coincident(g0,g1)
    c: Coincident(g2,g3)
    c: Coincident(g3,g0)
    c: Vertical(g0)
    c: Vertical(g2)
    c: Horizontal(g1)
    c: Horizontal(g3)
    c: Coincident(g0,g-3)
    c: PointOnObject(g5,g1)
    c: PointOnObject(g5,g2)
    c: Tangent(g1,g4) = -1.5708
    c: Tangent(g2,g4) = -1.5708
FEATURE [PartDesign::Pocket] Pocket014
  BaseFeature = -> Pocket011
  Direction = (0,1e-16,1)
  Length = 1.2
  Length2 = 5
  Placement = pos=(0,0,6) rot=(0,0,1;0rad)
  Profile = -> Sketch094
  ReferenceAxis = -> Sketch094 [N_Axis]
  Suppressed = false
  Type = 0
FEATURE [Sketcher::SketchObject] Sketch095
  AttachmentSupport = -> [ShapeBinder]
  ExternalGeometry = -> [ShapeBinder]
  FullyConstrained = false
  MapMode = 5
  Placement = pos=(0,-2.7e-15,-16) rot=(1,0,0;3.14159rad)
  sketch-geometry (31):
    g0: LineSegment StartX=-2.2752 StartY=3 StartZ=0 EndX=54.1734 EndY=3 EndZ=0
    g1: LineSegment StartX=54.1734 StartY=3 StartZ=0 EndX=64.7598 EndY=17.5123 EndZ=0
    g2: LineSegment StartX=64.7598 StartY=17.5123 StartZ=0 EndX=102.946 EndY=22.4786 EndZ=0
    g3: LineSegment StartX=102.946 StartY=22.4786 StartZ=0 EndX=119.981 EndY=32.3337 EndZ=0
    g4: ArcOfCircle CenterX=120.41 CenterY=31.5915 CenterZ=0 NormalX=0 NormalY=0 NormalZ=1 AngleXU=0 Radius=0.857438 StartAngle=0.522377 EndAngle=2.09527
    g5: LineSegment StartX=121.154 StartY=32.0193 StartZ=0 EndX=136.73 EndY=4.96388 EndZ=0
    g6: LineSegment StartX=136.73 StartY=4.96388 StartZ=0 EndX=136.73 EndY=-58.8821 EndZ=0
    g7: ArcOfCircle CenterX=136.112 CenterY=-58.8821 CenterZ=0 NormalX=0 NormalY=0 NormalZ=1 AngleXU=0 Radius=0.617924 StartAngle=4.71239 EndAngle=6.28319
    g8: LineSegment StartX=136.112 StartY=-59.5 StartZ=0 EndX=116.334 EndY=-59.5 EndZ=0
    g9: ArcOfCircle CenterX=116.334 CenterY=-59.8538 CenterZ=0 NormalX=0 NormalY=0 NormalZ=1 AngleXU=0 Radius=0.353806 StartAngle=1.5708 EndAngle=3.14159
    g10: LineSegment StartX=115.98 StartY=-59.8538 StartZ=0 EndX=115.98 EndY=-61.2993 EndZ=0
    g11: ArcOfCircle CenterX=115.529 CenterY=-61.2993 CenterZ=0 NormalX=0 NormalY=0 NormalZ=1 AngleXU=0 Radius=0.450718 StartAngle=4.71239 EndAngle=6.28319
    g12: LineSegment StartX=115.529 StartY=-61.75 StartZ=0 EndX=97.1988 EndY=-61.75 EndZ=0
    g13: ArcOfCircle CenterX=97.1988 CenterY=-61.9688 CenterZ=0 NormalX=0 NormalY=0 NormalZ=1 AngleXU=0 Radius=0.218754 StartAngle=1.5708 EndAngle=3.14159
    g14: LineSegment StartX=96.98 StartY=-61.9688 StartZ=0 EndX=96.98 EndY=-63.4166 EndZ=0
    g15: ArcOfCircle CenterX=96.3966 CenterY=-63.4166 CenterZ=0 NormalX=0 NormalY=0 NormalZ=1 AngleXU=0 Radius=0.583444 StartAngle=4.71239 EndAngle=6.28318
    g16: LineSegment StartX=96.3966 StartY=-64 StartZ=0 EndX=78.3317 EndY=-64 EndZ=0
    g17: ArcOfCircle CenterX=78.3317 CenterY=-64.3517 CenterZ=0 NormalX=0 NormalY=0 NormalZ=1 AngleXU=0 Radius=0.3517 StartAngle=1.5708 EndAngle=3.14159
    g18: LineSegment StartX=77.98 StartY=-64.3517 StartZ=0 EndX=77.98 EndY=-65.8316 EndZ=0
    g19: ArcOfCircle CenterX=77.5616 CenterY=-65.8316 CenterZ=0 NormalX=0 NormalY=0 NormalZ=1 AngleXU=0 Radius=0.418401 StartAngle=4.71239 EndAngle=6.28318
    g20: LineSegment StartX=77.5616 StartY=-66.25 StartZ=0 EndX=54.4496 EndY=-66.25 EndZ=0
    g21: ArcOfCircle CenterX=54.4496 CenterY=-65.7804 CenterZ=0 NormalX=0 NormalY=0 NormalZ=1 AngleXU=0 Radius=0.469571 StartAngle=3.14159 EndAngle=4.71239
    g22: LineSegment StartX=53.98 StartY=-65.7804 StartZ=0 EndX=53.98 EndY=-64.4483 EndZ=0
    g23: ArcOfCircle CenterX=53.5317 CenterY=-64.4483 CenterZ=0 NormalX=0 NormalY=0 NormalZ=1 AngleXU=0 Radius=0.448303 StartAngle=5.92e-14 EndAngle=1.5708
    g24: LineSegment StartX=53.5317 StartY=-64 StartZ=0 EndX=35.7843 EndY=-64 EndZ=0
    g25: ArcOfCircle CenterX=35.7843 CenterY=-63.1957 CenterZ=0 NormalX=0 NormalY=0 NormalZ=1 AngleXU=0 Radius=0.804272 StartAngle=3.14159 EndAngle=4.71239
    g26: LineSegment StartX=34.98 StartY=-63.1957 StartZ=0 EndX=34.98 EndY=-59.9399 EndZ=0
    g27: ArcOfCircle CenterX=34.2901 CenterY=-59.9399 CenterZ=0 NormalX=0 NormalY=0 NormalZ=1 AngleXU=0 Radius=0.689901 StartAngle=0 EndAngle=1.5708
    g28: LineSegment StartX=34.2901 StartY=-59.25 StartZ=0 EndX=-3 EndY=-59.25 EndZ=0
    g29: LineSegment StartX=-3 StartY=-59.25 StartZ=0 EndX=-3 EndY=2.2752 EndZ=0
    g30: ArcOfCircle CenterX=-2.2752 CenterY=2.2752 CenterZ=0 NormalX=0 NormalY=0 NormalZ=1 AngleXU=0 Radius=0.7248 StartAngle=1.5708 EndAngle=3.14159
  constraints (53):
    c: Tangent(g-4,g0) = 1.5708
    c: Coincident(g0,g1)
    c: Coincident(g1,g-62)
    c: Coincident(g1,g2)
    c: Coincident(g2,g-61)
    c: Coincident(g2,g3)
    c: Coincident(g3,g-58)
    c: Coincident(g4,g3)
    c: Tangent(g4,g-57) = -1.5708
    c: Tangent(g4,g5) = 1.5708
    c: Coincident(g5,g6)
    c: Coincident(g6,g-52)
    c: Vertical(g6)
    c: Coincident(g7,g6)
    c: Tangent(g7,g-51) = -1.5708
    c: Tangent(g7,g8) = 1.5708
    c: Coincident(g9,g8)
    c: Tangent(g9,g-45) = -1.5708
    c: Coincident(g10,g9)
    c: Coincident(g10,g-44)
    c: Coincident(g11,g10)
    c: Tangent(g11,g12) = 1.5708
    c: Coincident(g13,g12)
    c: Coincident(g13,g-41)
    c: Tangent(g13,g-40)
    c: Coincident(g15,g-35)
    c: Coincident(g15,g14)
    c: Tangent(g15,g16) = 1.5708
    c: Tangent(g17,g-32) = -1.5708
    c: Coincident(g17,g16)
    c: Coincident(g19,g18)
    c: Tangent(g19,g-30) = -1.5708
    c: Tangent(g19,g20) = 1.5708
    c: Coincident(g21,g20)
    c: Tangent(g21,g-24) = -1.5708
    c: Coincident(g22,g21)
    c: Coincident(g22,g-20)
    c: Tangent(g23,g-19) = -1.5708
    c: Coincident(g23,g22)
    c: Coincident(g24,g23)
    c: Coincident(g24,g-14)
    c: Tangent(g25,g-13) = -1.5708
    c: Coincident(g25,g24)
    c: Tangent(g25,g26) = 1.5708
    c: Tangent(g27,g-11) = -1.5708
    c: Coincident(g27,g26)
    c: Coincident(g28,g27)
    c: Coincident(g28,g-10)
    c: Coincident(g29,g28)
    c: Coincident(g29,g-5)
    c: Coincident(g30,g0)
    c: Coincident(g30,g29)
    c: Tangent(g30,g-4)
FEATURE [Sketcher::SketchObject] Sketch096
  AttachmentSupport = -> [ShapeBinder]
  ExternalGeometry = -> [ShapeBinder]
  FullyConstrained = false
  MapMode = 5
  Placement = pos=(0,-2.7e-15,-16) rot=(1,0,0;3.14159rad)
  sketch-geometry (119):
    g0: LineSegment StartX=-2.2752 StartY=3 StartZ=0 EndX=54.1734 EndY=3 EndZ=0
    g1: LineSegment StartX=54.1734 StartY=3 StartZ=0 EndX=64.7598 EndY=17.5123 EndZ=0
    g2: LineSegment StartX=64.7598 StartY=17.5123 StartZ=0 EndX=102.946 EndY=22.4786 EndZ=0
    g3: LineSegment StartX=102.946 StartY=22.4786 StartZ=0 EndX=119.981 EndY=32.3337 EndZ=0
    g4: ArcOfCircle CenterX=120.41 CenterY=31.5915 CenterZ=0 NormalX=0 NormalY=0 NormalZ=1 AngleXU=0 Radius=0.857438 StartAngle=0.522377 EndAngle=2.09527
    g5: LineSegment StartX=121.154 StartY=32.0193 StartZ=0 EndX=136.73 EndY=4.96388 EndZ=0
    g6: LineSegment StartX=136.73 StartY=4.96388 StartZ=0 EndX=136.73 EndY=-58.8821 EndZ=0
    g7: ArcOfCircle CenterX=136.112 CenterY=-58.8821 CenterZ=0 NormalX=0 NormalY=0 NormalZ=1 AngleXU=0 Radius=0.617924 StartAngle=4.71239 EndAngle=6.28319
    g8: LineSegment StartX=136.112 StartY=-59.5 StartZ=0 EndX=116.334 EndY=-59.5 EndZ=0
    g9: ArcOfCircle CenterX=116.334 CenterY=-59.8538 CenterZ=0 NormalX=0 NormalY=0 NormalZ=1 AngleXU=0 Radius=0.353806 StartAngle=1.5708 EndAngle=3.14159
    g10: LineSegment StartX=115.98 StartY=-59.8538 StartZ=0 EndX=115.98 EndY=-61.2993 EndZ=0
    g11: ArcOfCircle CenterX=115.529 CenterY=-61.2993 CenterZ=0 NormalX=0 NormalY=0 NormalZ=1 AngleXU=0 Radius=0.450718 StartAngle=4.71239 EndAngle=6.28319
    g12: LineSegment StartX=115.529 StartY=-61.75 StartZ=0 EndX=97.1988 EndY=-61.75 EndZ=0
    g13: ArcOfCircle CenterX=97.1988 CenterY=-61.9688 CenterZ=0 NormalX=0 NormalY=0 NormalZ=1 AngleXU=0 Radius=0.218754 StartAngle=1.5708 EndAngle=3.14159
    g14: LineSegment StartX=96.98 StartY=-61.9688 StartZ=0 EndX=96.98 EndY=-63.4166 EndZ=0
    g15: ArcOfCircle CenterX=96.3966 CenterY=-63.4166 CenterZ=0 NormalX=0 NormalY=0 NormalZ=1 AngleXU=0 Radius=0.583444 StartAngle=4.71239 EndAngle=6.28318
    g16: LineSegment StartX=96.3966 StartY=-64 StartZ=0 EndX=78.3317 EndY=-64 EndZ=0
    g17: ArcOfCircle CenterX=78.3317 CenterY=-64.3517 CenterZ=0 NormalX=0 NormalY=0 NormalZ=1 AngleXU=0 Radius=0.3517 StartAngle=1.5708 EndAngle=3.14159
    g18: LineSegment StartX=77.98 StartY=-64.3517 StartZ=0 EndX=77.98 EndY=-65.8316 EndZ=0
    g19: ArcOfCircle CenterX=77.5616 CenterY=-65.8316 CenterZ=0 NormalX=0 NormalY=0 NormalZ=1 AngleXU=0 Radius=0.418401 StartAngle=4.71239 EndAngle=6.28318
    g20: LineSegment StartX=77.5616 StartY=-66.25 StartZ=0 EndX=54.4496 EndY=-66.25 EndZ=0
    g21: ArcOfCircle CenterX=54.4496 CenterY=-65.7804 CenterZ=0 NormalX=0 NormalY=0 NormalZ=1 AngleXU=0 Radius=0.469571 StartAngle=3.14159 EndAngle=4.71239
    g22: LineSegment StartX=53.98 StartY=-65.7804 StartZ=0 EndX=53.98 EndY=-64.4483 EndZ=0
    g23: ArcOfCircle CenterX=53.5317 CenterY=-64.4483 CenterZ=0 NormalX=0 NormalY=0 NormalZ=1 AngleXU=0 Radius=0.448303 StartAngle=5.92e-14 EndAngle=1.5708
    g24: LineSegment StartX=53.5317 StartY=-64 StartZ=0 EndX=35.7843 EndY=-64 EndZ=0
    g25: ArcOfCircle CenterX=35.7843 CenterY=-63.1957 CenterZ=0 NormalX=0 NormalY=0 NormalZ=1 AngleXU=0 Radius=0.804272 StartAngle=3.14159 EndAngle=4.71239
    g26: LineSegment StartX=34.98 StartY=-63.1957 StartZ=0 EndX=34.98 EndY=-59.9399 EndZ=0
    g27: ArcOfCircle CenterX=34.2901 CenterY=-59.9399 CenterZ=0 NormalX=0 NormalY=0 NormalZ=1 AngleXU=0 Radius=0.689901 StartAngle=0 EndAngle=1.5708
    g28: LineSegment StartX=34.2901 StartY=-59.25 StartZ=0 EndX=-3 EndY=-59.25 EndZ=0
    g29: LineSegment StartX=-3 StartY=-59.25 StartZ=0 EndX=-3 EndY=2.2752 EndZ=0
    g30: ArcOfCircle CenterX=-2.2752 CenterY=2.2752 CenterZ=0 NormalX=0 NormalY=0 NormalZ=1 AngleXU=0 Radius=0.7248 StartAngle=1.5708 EndAngle=3.14159
    g31: LineSegment StartX=-0.150389 StartY=1 StartZ=0 EndX=55.19 EndY=1 EndZ=0
    g32: LineSegment StartX=55.19 StartY=1 StartZ=0 EndX=65.9238 EndY=15.7144 EndZ=0
    g33: LineSegment StartX=65.9238 StartY=15.7144 StartZ=0 EndX=103.751 EndY=20.634 EndZ=0
    g34: LineSegment StartX=103.751 StartY=20.634 StartZ=0 EndX=118.869 EndY=29.3799 EndZ=0
    g35: ArcOfCircle CenterX=119.558 CenterY=28.1883 CenterZ=0 NormalX=0 NormalY=0 NormalZ=1 AngleXU=0 Radius=1.37659 StartAngle=0.517526 EndAngle=2.09527
    g36: LineSegment StartX=120.755 StartY=28.8693 StartZ=0 EndX=134.73 EndY=4.32052 EndZ=0
    g37: LineSegment StartX=134.73 StartY=4.32052 StartZ=0 EndX=134.73 EndY=-56.9441 EndZ=0
    g38: ArcOfCircle CenterX=134.174 CenterY=-56.9441 CenterZ=0 NormalX=0 NormalY=0 NormalZ=1 AngleXU=0 Radius=0.555946 StartAngle=4.71239 EndAngle=6.28319
    g39: LineSegment StartX=134.174 StartY=-57.5 StartZ=0 EndX=113.98 EndY=-57.5 EndZ=0
    g40: LineSegment StartX=113.98 StartY=-57.5 StartZ=0 EndX=113.98 EndY=-59.2166 EndZ=0
    g41: ArcOfCircle CenterX=113.447 CenterY=-59.2166 CenterZ=0 NormalX=0 NormalY=0 NormalZ=1 AngleXU=0 Radius=0.533416 StartAngle=4.71239 EndAngle=6.28319
    g42: LineSegment StartX=113.447 StartY=-59.75 StartZ=0 EndX=95.4233 EndY=-59.75 EndZ=0
    g43: ArcOfCircle CenterX=95.4233 CenterY=-60.1933 CenterZ=0 NormalX=0 NormalY=0 NormalZ=1 AngleXU=0 Radius=0.443253 StartAngle=1.5708 EndAngle=3.14159
    g44: LineSegment StartX=94.98 StartY=-60.1933 StartZ=0 EndX=94.98 EndY=-61.4124 EndZ=0
    g45: ArcOfCircle CenterX=94.3924 CenterY=-61.4124 CenterZ=0 NormalX=0 NormalY=0 NormalZ=1 AngleXU=0 Radius=0.587645 StartAngle=4.71239 EndAngle=6.28319
    g46: LineSegment StartX=94.3924 StartY=-62 StartZ=0 EndX=76.4717 EndY=-62 EndZ=0
    g47: ArcOfCircle CenterX=76.4717 CenterY=-62.4917 CenterZ=0 NormalX=0 NormalY=0 NormalZ=1 AngleXU=0 Radius=0.491748 StartAngle=1.5708 EndAngle=3.14159
    g48: LineSegment StartX=75.98 StartY=-62.4917 StartZ=0 EndX=75.98 EndY=-63.7211 EndZ=0
    g49: ArcOfCircle CenterX=75.4511 CenterY=-63.7211 CenterZ=0 NormalX=0 NormalY=0 NormalZ=1 AngleXU=0 Radius=0.528895 StartAngle=4.71239 EndAngle=6.28319
    g50: LineSegment StartX=75.4511 StartY=-64.25 StartZ=0 EndX=56.4769 EndY=-64.25 EndZ=0
    g51: ArcOfCircle CenterX=56.4769 CenterY=-63.7531 CenterZ=0 NormalX=0 NormalY=0 NormalZ=1 AngleXU=0 Radius=0.496936 StartAngle=3.14159 EndAngle=4.71239
    g52: LineSegment StartX=55.98 StartY=-62.5636 StartZ=0 EndX=55.98 EndY=-63.7531 EndZ=0
    g53: ArcOfCircle CenterX=55.4164 CenterY=-62.5636 CenterZ=0 NormalX=0 NormalY=0 NormalZ=1 AngleXU=0 Radius=0.563591 StartAngle=-1.8e-15 EndAngle=1.5708
    g54: LineSegment StartX=55.4164 StartY=-62 StartZ=0 EndX=37.5625 EndY=-62 EndZ=0
    g55: ArcOfCircle CenterX=37.5625 CenterY=-61.4175 CenterZ=0 NormalX=0 NormalY=0 NormalZ=1 AngleXU=0 Radius=0.582459 StartAngle=3.14159 EndAngle=4.71239
    g56: LineSegment StartX=36.98 StartY=-61.4175 StartZ=0 EndX=36.98 EndY=-58.0131 EndZ=0
    g57: ArcOfCircle CenterX=36.2169 CenterY=-58.0131 CenterZ=0 NormalX=0 NormalY=0 NormalZ=1 AngleXU=0 Radius=0.763133 StartAngle=4.4e-15 EndAngle=1.5708
    g58: LineSegment StartX=36.2169 StartY=-57.25 StartZ=0 EndX=-1 EndY=-57.25 EndZ=0
    g59: LineSegment StartX=-1 StartY=-57.25 StartZ=0 EndX=-1 EndY=0.150389 EndZ=0
    g60: ArcOfCircle CenterX=-0.150389 CenterY=0.150389 CenterZ=0 NormalX=0 NormalY=0 NormalZ=1 AngleXU=0 Radius=0.849611 StartAngle=1.5708 EndAngle=3.14159
    g61: LineSegment StartX=-0.132 StartY=0.5 StartZ=0 EndX=55.4442 EndY=0.5 EndZ=0
    g62: LineSegment StartX=55.4442 StartY=0.5 StartZ=0 EndX=66.2012 EndY=15.2462 EndZ=0
    g63: LineSegment StartX=66.2012 StartY=15.2462 StartZ=0 EndX=103.915 EndY=20.1511 EndZ=0
    g64: LineSegment StartX=134.23 StartY=4.18817 StartZ=0 EndX=134.23 EndY=-56.9441 EndZ=0
    g65: LineSegment StartX=134.174 StartY=-57 StartZ=0 EndX=113.48 EndY=-57 EndZ=0
    g66: LineSegment StartX=113.48 StartY=-57 StartZ=0 EndX=113.48 EndY=-59.2166 EndZ=0
    g67: LineSegment StartX=113.447 StartY=-59.25 StartZ=0 EndX=95.4233 EndY=-59.25 EndZ=0
    g68: LineSegment StartX=94.48 StartY=-60.1933 StartZ=0 EndX=94.48 EndY=-61.4124 EndZ=0
    g69: LineSegment StartX=94.3924 StartY=-61.5 StartZ=0 EndX=76.4717 EndY=-61.5 EndZ=0
    g70: LineSegment StartX=75.48 StartY=-62.4917 StartZ=0 EndX=75.48 EndY=-63.7211 EndZ=0
    g71: LineSegment StartX=75.4511 StartY=-63.75 StartZ=0 EndX=56.5678 EndY=-63.75 EndZ=0
    g72: LineSegment StartX=56.48 StartY=-63.6622 StartZ=0 EndX=56.48 EndY=-62.5636 EndZ=0
    g73: LineSegment StartX=55.4164 StartY=-61.5 StartZ=0 EndX=37.7334 EndY=-61.5 EndZ=0
    g74: LineSegment StartX=37.48 StartY=-61.2466 StartZ=0 EndX=37.48 EndY=-58.0131 EndZ=0
    g75: LineSegment StartX=36.2169 StartY=-56.75 StartZ=0 EndX=-0.5 EndY=-56.75 EndZ=0
    g76: LineSegment StartX=-0.5 StartY=-56.75 StartZ=0 EndX=-0.5 EndY=0.132 EndZ=0
    g77: LineSegment StartX=8.34144 StartY=1 StartZ=0 EndX=8.34144 EndY=0.5 EndZ=0
    g78: LineSegment StartX=59.6956 StartY=7.17637 StartZ=0 EndX=60.0995 EndY=6.8817 EndZ=0
    g79: LineSegment StartX=76.1703 StartY=16.5427 StartZ=0 EndX=76.1058 EndY=17.0386 EndZ=0
    g80: LineSegment StartX=111.557 StartY=24.5718 StartZ=0 EndX=111.31 EndY=25.0069 EndZ=0
    g81: LineSegment StartX=134.23 StartY=0.582883 StartZ=0 EndX=134.73 EndY=0.582883 EndZ=0
    g82: LineSegment StartX=103.915 StartY=20.1511 StartZ=0 EndX=119.12 EndY=28.9471 EndZ=0
    g83: LineSegment StartX=120.32 StartY=28.622 StartZ=0 EndX=134.23 EndY=4.18817 EndZ=0
    g84: LineSegment StartX=118.869 StartY=29.3799 StartZ=0 EndX=119.12 EndY=28.9471 EndZ=0
    g85: LineSegment StartX=120.755 StartY=28.8693 StartZ=0 EndX=120.32 EndY=28.622 EndZ=0
    g86: ArcOfCircle CenterX=119.557 CenterY=28.1824 CenterZ=0 NormalX=0 NormalY=0 NormalZ=1 AngleXU=0 Radius=0.880884 StartAngle=0.522399 EndAngle=2.09037
    g87: LineSegment StartX=134.73 StartY=-56.9441 StartZ=0 EndX=134.23 EndY=-56.9441 EndZ=0
    g88: LineSegment StartX=134.174 StartY=-57.5 StartZ=0 EndX=134.174 EndY=-57 EndZ=0
    g89: ArcOfCircle CenterX=134.177 CenterY=-56.9466 CenterZ=0 NormalX=0 NormalY=0 NormalZ=1 AngleXU=0 Radius=0.053458 StartAngle=4.66469 EndAngle=6.33088
    g90: LineSegment StartX=113.447 StartY=-59.75 StartZ=0 EndX=113.447 EndY=-59.25 EndZ=0
    g91: LineSegment StartX=113.98 StartY=-59.2166 StartZ=0 EndX=113.48 EndY=-59.2166 EndZ=0
    g92: ArcOfCircle CenterX=113.446 CenterY=-59.2162 CenterZ=0 NormalX=0 NormalY=0 NormalZ=1 AngleXU=0 Radius=0.0337606 StartAngle=4.72255 EndAngle=6.27303
    g93: LineSegment StartX=95.4233 StartY=-59.75 StartZ=0 EndX=95.4233 EndY=-59.25 EndZ=0
    g94: LineSegment StartX=94.98 StartY=-60.1933 StartZ=0 EndX=94.48 EndY=-60.1933 EndZ=0
    g95: ArcOfCircle CenterX=95.4289 CenterY=-60.1989 CenterZ=0 NormalX=0 NormalY=0 NormalZ=1 AngleXU=0 Radius=0.948911 StartAngle=1.57674 EndAngle=3.13565
    g96: LineSegment StartX=94.98 StartY=-61.4124 StartZ=0 EndX=94.48 EndY=-61.4124 EndZ=0
    g97: LineSegment StartX=94.3924 StartY=-62 StartZ=0 EndX=94.3924 EndY=-61.5 EndZ=0
    g98: ArcOfCircle CenterX=94.3918 CenterY=-61.4118 CenterZ=0 NormalX=0 NormalY=0 NormalZ=1 AngleXU=0 Radius=0.0881892 StartAngle=4.71854 EndAngle=6.27703
    g99: LineSegment StartX=76.4717 StartY=-62 StartZ=0 EndX=76.4717 EndY=-61.5 EndZ=0
    g100: LineSegment StartX=75.98 StartY=-62.4917 StartZ=0 EndX=75.48 EndY=-62.4917 EndZ=0
    g101: ArcOfCircle CenterX=76.4704 CenterY=-62.4904 CenterZ=0 NormalX=0 NormalY=0 NormalZ=1 AngleXU=0 Radius=0.990437 StartAngle=1.56947 EndAngle=3.14292
    g102: LineSegment StartX=75.98 StartY=-63.7211 StartZ=0 EndX=75.48 EndY=-63.7211 EndZ=0
    g103: LineSegment StartX=75.4511 StartY=-64.25 StartZ=0 EndX=75.4511 EndY=-63.75 EndZ=0
    g104: ArcOfCircle CenterX=75.4508 CenterY=-63.7208 CenterZ=0 NormalX=0 NormalY=0 NormalZ=1 AngleXU=0 Radius=0.029212 StartAngle=4.72318 EndAngle=6.27239
    g105: ArcOfCircle CenterX=56.5678 CenterY=-63.6622 CenterZ=0 NormalX=0 NormalY=0 NormalZ=1 AngleXU=0 Radius=0.087844 StartAngle=3.14159 EndAngle=4.71239
    g106: GeomPoint X=56.48 Y=-63.75 Z=0
    g107: ArcOfCircle CenterX=55.4164 CenterY=-62.5636 CenterZ=0 NormalX=0 NormalY=0 NormalZ=1 AngleXU=0 Radius=1.06359 StartAngle=1e-16 EndAngle=1.5708
    g108: GeomPoint X=56.48 Y=-61.5 Z=0
    g109: LineSegment StartX=55.4164 StartY=-62 StartZ=0 EndX=55.4164 EndY=-61.5 EndZ=0
    g110: LineSegment StartX=55.98 StartY=-62.5636 StartZ=0 EndX=56.48 EndY=-62.5636 EndZ=0
    g111: ArcOfCircle CenterX=37.7334 CenterY=-61.2466 CenterZ=0 NormalX=0 NormalY=0 NormalZ=1 AngleXU=0 Radius=0.25341 StartAngle=3.14159 EndAngle=4.71239
    g112: GeomPoint X=37.48 Y=-61.5 Z=0
    g113: ArcOfCircle CenterX=36.2169 CenterY=-58.0131 CenterZ=0 NormalX=0 NormalY=0 NormalZ=1 AngleXU=0 Radius=1.26313 StartAngle=0 EndAngle=1.5708
    g114: GeomPoint X=37.48 Y=-56.75 Z=0
    g115: LineSegment StartX=36.2169 StartY=-57.25 StartZ=0 EndX=36.2169 EndY=-56.75 EndZ=0
    g116: LineSegment StartX=36.98 StartY=-58.0131 StartZ=0 EndX=37.48 EndY=-58.0131 EndZ=0
    g117: ArcOfCircle CenterX=-0.132 CenterY=0.132 CenterZ=0 NormalX=0 NormalY=0 NormalZ=1 AngleXU=0 Radius=0.368 StartAngle=1.5708 EndAngle=3.14159
    g118: GeomPoint X=-0.5 Y=0.5 Z=0
  constraints (243):
    c: Tangent(g-4,g0) = 1.5708
    c: Coincident(g0,g1)
    c: Coincident(g1,g-62)
    c: Coincident(g1,g2)
    c: Coincident(g2,g-61)
    c: Coincident(g2,g3)
    c: Coincident(g3,g-58)
    c: Coincident(g4,g3)
    c: Tangent(g4,g-57) = -1.5708
    c: Tangent(g4,g5) = 1.5708
    c: Coincident(g5,g6)
    c: Coincident(g6,g-52)
    c: Vertical(g6)
    c: Coincident(g7,g6)
    c: Tangent(g7,g-51) = -1.5708
    c: Tangent(g7,g8) = 1.5708
    c: Coincident(g9,g8)
    c: Tangent(g9,g-45) = -1.5708
    c: Coincident(g10,g9)
    c: Coincident(g10,g-44)
    c: Coincident(g11,g10)
    c: Tangent(g11,g12) = 1.5708
    c: Coincident(g13,g12)
    c: Coincident(g13,g-41)
    c: Tangent(g13,g-40)
    c: Coincident(g15,g-35)
    c: Coincident(g15,g14)
    c: Tangent(g15,g16) = 1.5708
    c: Tangent(g17,g-32) = -1.5708
    c: Coincident(g17,g16)
    c: Coincident(g19,g18)
    c: Tangent(g19,g-30) = -1.5708
    c: Tangent(g19,g20) = 1.5708
    c: Coincident(g21,g20)
    c: Tangent(g21,g-24) = -1.5708
    c: Coincident(g22,g21)
    c: Coincident(g22,g-20)
    c: Tangent(g23,g-19) = -1.5708
    c: Coincident(g23,g22)
    c: Coincident(g24,g23)
    c: Coincident(g24,g-14)
    c: Tangent(g25,g-13) = -1.5708
    c: Coincident(g25,g24)
    c: Tangent(g25,g26) = 1.5708
    c: Tangent(g27,g-11) = -1.5708
    c: Coincident(g27,g26)
    c: Coincident(g28,g27)
    c: Coincident(g28,g-10)
    c: Coincident(g29,g28)
    c: Coincident(g29,g-5)
    c: Coincident(g30,g0)
    c: Coincident(g30,g29)
    c: Tangent(g30,g-4)
    c: Coincident(g-8,g31)
    c: Coincident(g31,g-63)
    c: Coincident(g31,g32)
    c: Coincident(g32,g-63)
    c: Coincident(g32,g33)
    c: Coincident(g33,g-60)
    c: Coincident(g33,g34)
    c: Coincident(g34,g-59)
    c: Coincident(g35,g34)
    c: Tangent(g35,g-56) = -1.5708
    c: Tangent(g35,g36) = 1.5708
    c: Coincident(g36,g37)
    c: Coincident(g37,g-53)
    c: Vertical(g37)
    c: Tangent(g38,g-50) = -1.5708
    c: Coincident(g38,g37)
    c: Tangent(g38,g39) = 1.5708
    c: Coincident(g39,g40)
    c: Coincident(g40,g-48)
    c: Vertical(g40)
    c: Tangent(g41,g-47) = -1.5708
    c: Coincident(g41,g40)
    c: Tangent(g41,g42) = 1.5708
    c: Tangent(g43,g-38) = -1.5708
    c: Coincident(g43,g42)
    c: Coincident(g44,g43)
    c: Coincident(g44,g-37)
    c: Tangent(g45,g-36) = -1.5708
    c: Coincident(g45,g44)
    c: Tangent(g45,g46) = 1.5708
    c: Tangent(g47,g-29) = -1.5708
    c: Coincident(g47,g46)
    c: Coincident(g48,g47)
    c: Coincident(g48,g-28)
    c: Coincident(g49,g48)
    c: Tangent(g49,g-27) = -1.5708
    c: Tangent(g51,g-23) = -1.5708
    c: Coincident(g51,g50)
    c: Coincident(g52,g-22)
    c: Coincident(g52,g51)
    c: Tangent(g53,g-22) = -1.5708
    c: Coincident(g53,g52)
    c: Coincident(g54,g53)
    c: Coincident(g54,g-16)
    c: Coincident(g55,g-17)
    c: Coincident(g55,g54)
    c: Tangent(g55,g-16)
    c: Coincident(g56,g55)
    c: Coincident(g56,g-18)
    c: Tangent(g57,g-18) = -1.5708
    c: Coincident(g57,g56)
    c: Tangent(g57,g58) = -1.5708
    c: Coincident(g58,g59)
    c: Coincident(g59,g-7)
    c: Vertical(g59)
    c: Coincident(g60,g31)
    c: Coincident(g60,g59)
    c: Horizontal(g61)
    c: Coincident(g61,g62)
    c: Coincident(g62,g63)
    c: Coincident(g63,g82)
    c: Coincident(g83,g64)
    c: Vertical(g64)
    c: Horizontal(g65)
    c: Coincident(g65,g66)
    c: Horizontal(g67)
    c: Horizontal(g69)
    c: Horizontal(g71)
    c: Vertical(g72)
    c: Horizontal(g73)
    c: Horizontal(g75)
    c: Coincident(g75,g76)
    c: Vertical(g76)
    c: Vertical(g77)
    c: PointOnObject(g77,g31)
    c: PointOnObject(g77,g61)
    c: Parallel(g62,g32)
    c: PointOnObject(g78,g32)
    c: PointOnObject(g78,g62)
    c: Perpendicular(g32,g78)
    c: Distance(g78) = 0.5
    c: Distance(g77) = 0.5
    c: PointOnObject(g79,g63)
    c: PointOnObject(g79,g33)
    c: Parallel(g63,g33)
    c: Perpendicular(g33,g79)
    c: Distance(g79) = 0.5
    c: Symmetric(g34,g34,g80)
    c: Distance(g80) = 0.5
    c: Horizontal(g81)
    c: PointOnObject(g81,g64)
    c: PointOnObject(g81,g37)
    c: Distance(g81) = 0.5
    c: Distance(g39,g65) = 0.5
    c: Vertical(g66)
    c: Distance(g40,g66) = 0.5
    c: Distance(g42,g67) = 0.5
    c: Vertical(g68)
    c: Distance(g43,g68) = 0.5
    c: Distance(g45,g69) = 0.5
    c: Vertical(g70)
    c: Distance(g47,g70) = 0.5
    c: Distance(g50,g71) = 0.5
    c: Distance(g52,g72) = 0.5
    c: Distance(g53,g73) = 0.5
    c: Vertical(g74)
    c: Distance(g56,g74) = 0.5
    c: Distance(g57,g75) = 0.5
    c: Distance(g58,g76) = 0.5
    c: Parallel(g83,g36)
    c: Distance(g35,g83) = 0.5
    c: Coincident(g84,g34)
    c: Perpendicular(g34,g84)
    c: PointOnObject(g80,g82)
    c: Parallel(g82,g34)
    c: Coincident(g85,g35)
    c: Perpendicular(g36,g85)
    c: Coincident(g84,g82)
    c: Coincident(g85,g83)
    c: Coincident(g86,g82)
    c: Coincident(g86,g83)
    c: Coincident(g87,g37)
    c: Horizontal(g87)
    c: Coincident(g88,g38)
    c: Vertical(g88)
    c: Coincident(g64,g87)
    c: Coincident(g65,g88)
    c: Coincident(g89,g64)
    c: Coincident(g89,g65)
    c: Vertical(g90)
    c: Coincident(g90,g41)
    c: Coincident(g67,g90)
    c: Coincident(g66,g91)
    c: Coincident(g92,g66)
    c: Coincident(g92,g67)
    c: Vertical(g93)
    c: Coincident(g93,g42)
    c: Coincident(g94,g68)
    c: Coincident(g93,g67)
    c: Coincident(g95,g67)
    c: Coincident(g95,g68)
    c: Horizontal(g96)
    c: Coincident(g96,g44)
    c: Coincident(g98,g68)
    c: Coincident(g98,g69)
    c: Vertical(g99)
    c: Coincident(g99,g46)
    c: Coincident(g69,g99)
    c: Coincident(g100,g70)
    c: Coincident(g101,g70)
    c: Coincident(g101,g69)
    c: Coincident(g50,g49)
    c: Horizontal(g102)
    c: Coincident(g102,g48)
    c: Coincident(g104,g70)
    c: Coincident(g104,g71)
    c: PointOnObject(g106,g72)
    c: PointOnObject(g106,g71)
    c: Tangent(g72,g105) = 1.5708
    c: Tangent(g71,g105) = 1.5708
    c: PointOnObject(g108,g73)
    c: PointOnObject(g108,g72)
    c: Tangent(g73,g107) = -1.5708
    c: Tangent(g72,g107) = -1.5708
    c: Coincident(g109,g53)
    c: Coincident(g109,g73)
    c: Vertical(g109)
    c: Coincident(g110,g52)
    c: Coincident(g110,g72)
    c: PointOnObject(g112,g74)
    c: PointOnObject(g112,g73)
    c: Tangent(g74,g111) = 1.5708
    c: Tangent(g73,g111) = 1.5708
    c: PointOnObject(g114,g75)
    c: PointOnObject(g114,g74)
    c: Tangent(g75,g113) = -1.5708
    c: Tangent(g74,g113) = -1.5708
    c: Coincident(g115,g57)
    c: Coincident(g115,g75)
    c: Vertical(g115)
    c: Coincident(g116,g56)
    c: Coincident(g116,g74)
    c: PointOnObject(g118,g61)
    c: PointOnObject(g118,g76)
    c: Tangent(g61,g117) = 1.5708
    c: Tangent(g76,g117) = 1.5708
    c: Coincident(g96,g68)
    c: Coincident(g97,g69)
    c: Coincident(g102,g70)
    c: Coincident(g103,g71)
FEATURE [PartDesign::Pad] Pad022
  Direction = (0,0,-1)
  Length = 2
  Length2 = 10
  Placement = pos=(0,-2.7e-15,-22) rot=(0,0,1;0rad)
  Profile = -> Sketch095
  ReferenceAxis = -> Sketch095 [N_Axis]
  Suppressed = false
  Type = 0
FEATURE [PartDesign::Pad] Pad023
  BaseFeature = -> Pad022
  Direction = (0,-1e-16,-1)
  Length = 1
  Length2 = 10
  Placement = pos=(0,-2.7e-15,-22) rot=(0,0,1;0rad)
  Profile = -> Sketch096
  ReferenceAxis = -> Sketch096 [N_Axis]
  Reversed = true
  Suppressed = false
  Type = 0
FEATURE [PartDesign::ShapeBinder] ShapeBinder001
  Support = -> [Pocket014]
  TraceSupport = false
FEATURE [Sketcher::SketchObject] Sketch097
  ExternalGeometry = -> [ShapeBinder001]
  FullyConstrained = true
  MapMode = 5
  Placement = pos=(0,-2.7e-15,-18) rot=(1,0,0;3.14159rad)
  sketch-geometry (5):
    g0: Circle CenterX=18.61 CenterY=-37.51 CenterZ=0 NormalX=0 NormalY=0 NormalZ=1 AngleXU=0 Radius=1.25
    g1: Circle CenterX=18.6 CenterY=-18.76 CenterZ=0 NormalX=0 NormalY=0 NormalZ=1 AngleXU=0 Radius=1.25
    g2: Circle CenterX=61.84 CenterY=-1.51 CenterZ=0 NormalX=0 NormalY=0 NormalZ=1 AngleXU=0 Radius=1.25
    g3: Circle CenterX=108.3 CenterY=6.24 CenterZ=0 NormalX=0 NormalY=0 NormalZ=1 AngleXU=0 Radius=1.25
    g4: Circle CenterX=94.55 CenterY=-41.5 CenterZ=0 NormalX=0 NormalY=0 NormalZ=1 AngleXU=0 Radius=1.25
  constraints (10):
    c: Diameter(g0) = 2.5
    c: Coincident(g0,g-4)
    c: Diameter(g1) = 2.5
    c: Coincident(g1,g-5)
    c: Diameter(g2) = 2.5
    c: Coincident(g2,g-6)
    c: Diameter(g3) = 2.5
    c: Coincident(g3,g-7)
    c: Diameter(g4) = 2.5
    c: Coincident(g4,g-3)
FEATURE [PartDesign::Pocket] Pocket015
  BaseFeature = -> Pad023
  Direction = (0,1e-16,1)
  Length = 5
  Length2 = 5
  Placement = pos=(0,-2.7e-15,-22) rot=(0,0,1;0rad)
  Profile = -> Sketch097
  ReferenceAxis = -> Sketch097 [N_Axis]
  Suppressed = false
  Type = 1
FEATURE [Sketcher::SketchObject] Sketch100
  FullyConstrained = false
  MapMode = 5
  Placement = pos=(0,-2.7e-15,-15) rot=(0,0,1;0rad)
  sketch-geometry (10):
    g0: LineSegment StartX=24.0467 StartY=45.7162 StartZ=0 EndX=24.0467 EndY=9.52623 EndZ=0
    g1: LineSegment StartX=26.9517 StartY=6.62123 StartZ=0 EndX=86.5306 EndY=6.62123 EndZ=0
    g2: LineSegment StartX=89.4356 StartY=9.52623 StartZ=0 EndX=89.4356 EndY=45.7162 EndZ=0
    g3: LineSegment StartX=86.5306 StartY=48.6212 StartZ=0 EndX=26.9517 EndY=48.6212 EndZ=0
    g4: ArcOfCircle CenterX=26.9517 CenterY=45.7162 CenterZ=0 NormalX=0 NormalY=0 NormalZ=1 AngleXU=0 Radius=2.905 StartAngle=1.5708 EndAngle=3.14159
    g5: ArcOfCircle CenterX=26.9517 CenterY=9.52623 CenterZ=0 NormalX=0 NormalY=0 NormalZ=1 AngleXU=0 Radius=2.905 StartAngle=3.14159 EndAngle=4.71239
    g6: ArcOfCircle CenterX=86.5306 CenterY=9.52623 CenterZ=0 NormalX=0 NormalY=0 NormalZ=1 AngleXU=0 Radius=2.905 StartAngle=4.71239 EndAngle=6.28319
    g7: ArcOfCircle CenterX=86.5306 CenterY=45.7162 CenterZ=0 NormalX=0 NormalY=0 NormalZ=1 AngleXU=0 Radius=2.905 StartAngle=5e-16 EndAngle=1.5708
    g8: GeomPoint X=24.0467 Y=48.6212 Z=0
    g9: GeomPoint X=89.4356 Y=6.62123 Z=0
  constraints (21):
    c: Tangent(g0,g4) = -1.5708
    c: Tangent(g0,g5) = -1.5708
    c: Tangent(g1,g5) = -1.5708
    c: Tangent(g1,g6) = -1.5708
    c: Tangent(g2,g6) = -1.5708
    c: Tangent(g2,g7) = -1.5708
    c: Tangent(g3,g7) = -1.5708
    c: Tangent(g3,g4) = -1.5708
    c: Vertical(g0)
    c: Vertical(g2)
    c: Horizontal(g1)
    c: Horizontal(g3)
    c: Equal(g4,g5)
    c: Equal(g5,g6)
    c: Equal(g6,g7)
    c: PointOnObject(g8,g0)
    c: PointOnObject(g8,g3)
    c: PointOnObject(g9,g1)
    c: PointOnObject(g9,g2)
    c: Distance(g1,g3) = 42
    c: Diameter(g7) = 5.81
FEATURE [PartDesign::Pocket] Pocket017
  BaseFeature = -> Pocket015
  Direction = (0,0,-1)
  Length = 2.6
  Length2 = 5
  Placement = pos=(0,-2.7e-15,-22) rot=(0,0,1;0rad)
  Profile = -> Sketch100
  ReferenceAxis = -> Sketch100 [N_Axis]
  Suppressed = false
  Type = 0
  expr: Length = 3 - 0.4
FEATURE [Sketcher::SketchObject] Sketch101
  AttachmentSupport = -> [Pocket013]
  ExternalGeometry = -> [Pocket013]
  FullyConstrained = true
  MapMode = 5
  Placement = pos=(0,0,1.4) rot=(0,0,1;0rad)
  sketch-geometry (5):
    g0: LineSegment StartX=129.88 StartY=24.6 StartZ=0 EndX=129.88 EndY=18.6 EndZ=0
    g1: LineSegment StartX=129.88 StartY=18.6 StartZ=0 EndX=133.38 EndY=18.6 EndZ=0
    g2: LineSegment StartX=133.38 StartY=18.6 StartZ=0 EndX=133.38 EndY=24.6 EndZ=0
    g3: LineSegment StartX=133.38 StartY=24.6 StartZ=0 EndX=131.63 EndY=24.6 EndZ=0
    g4: LineSegment StartX=131.63 StartY=24.6 StartZ=0 EndX=129.88 EndY=24.6 EndZ=0
  constraints (15):
    c: Coincident(g0,g1)
    c: Coincident(g1,g2)
    c: Coincident(g2,g3)
    c: Coincident(g4,g0)
    c: Vertical(g0)
    c: Vertical(g2)
    c: Horizontal(g1)
    c: Coincident(g3,g4)
    c: Horizontal(g3)
    c: Horizontal(g4)
    c: Equal(g3,g4)
    c: Vertical(g3,g-3)
    c: Distance(g1) = 3.5
    c: Distance(g0) = 6
    c: Distance(g3,g-3) = 4
FEATURE [PartDesign::Pad] Pad024
  BaseFeature = -> Pocket013
  Direction = (0,0,1)
  Length = 2
  Length2 = 10
  Profile = -> Sketch101
  ReferenceAxis = -> Sketch101 [N_Axis]
  Suppressed = false
  Type = 0
FEATURE [PartDesign::Body] Body005  label="PCB"
  AllowCompound = false
  Group = -> [MirroredSketch005,Pad021,Sketch093,Pocket013,Sketch101,Pad024]
  Origin = -> Origin005
  Placement = pos=(0,0,2) rot=(0,0,1;0rad)
  Tip = -> Pad024
FEATURE [Sketcher::SketchObject] Sketch102
  AttachmentSupport = -> [Pocket014]
  ExternalGeometry = -> [Pocket014]
  FullyConstrained = false
  MapMode = 5
  Placement = pos=(0,0,8) rot=(0,0,1;0rad)
  sketch-geometry (11):
    g0: ArcOfCircle CenterX=130.63 CenterY=20.0008 CenterZ=0 NormalX=0 NormalY=0 NormalZ=1 AngleXU=0 Radius=0.5 StartAngle=1.51475 EndAngle=3.14159
    g1: ArcOfCircle CenterX=130.63 CenterY=15.0011 CenterZ=0 NormalX=0 NormalY=0 NormalZ=1 AngleXU=0 Radius=0.5 StartAngle=3.14221 EndAngle=4.71239
    g2: ArcOfCircle CenterX=133.158 CenterY=15.0003 CenterZ=0 NormalX=0 NormalY=0 NormalZ=1 AngleXU=0 Radius=0.5 StartAngle=4.65634 EndAngle=6.28319
    g3: ArcOfCircle CenterX=133.158 CenterY=20 CenterZ=0 NormalX=0 NormalY=0 NormalZ=1 AngleXU=0 Radius=0.5 StartAngle=0.000620745 EndAngle=1.5708
    g4: GeomPoint X=133.38 Y=18.6 Z=0
    g5: LineSegment StartX=130.931 StartY=20.5 StartZ=0 EndX=130.931 EndY=59.5 EndZ=0
    g6: LineSegment StartX=130.658 StartY=20.5 StartZ=0 EndX=133.158 EndY=20.5 EndZ=0
    g7: LineSegment StartX=130.63 StartY=14.5011 StartZ=0 EndX=133.13 EndY=14.5011 EndZ=0
    g8: LineSegment StartX=133.658 StartY=15.0003 StartZ=0 EndX=133.658 EndY=20.0003 EndZ=0
    g9: LineSegment StartX=130.13 StartY=20.0008 StartZ=0 EndX=130.13 EndY=15.0008 EndZ=0
    g10: LineSegment StartX=130.13 StartY=18.3949 StartZ=0 EndX=136.73 EndY=18.3949 EndZ=0
  constraints (28):
    c: Vertical(g5)
    c: Distance(g5) = 39
    c: PointOnObject(g5,g-3)
    c: Coincident(g6,g0)
    c: Tangent(g6,g3) = 1.5708
    c: Horizontal(g6)
    c: Tangent(g7,g1) = -1.5708
    c: Coincident(g7,g2)
    c: Horizontal(g7)
    c: Tangent(g8,g2) = -1.5708
    c: Coincident(g8,g3)
    c: Vertical(g8)
    c: Tangent(g9,g0) = -1.5708
    c: Coincident(g9,g1)
    c: Vertical(g9)
    c: Distance(g9) = 5
    c: Distance(g6) = 2.5
    c: Radius(g0) = 0.5
    c: Radius(g3) = 0.5
    c: Radius(g2) = 0.5
    c: Radius(g1) = 0.5
    c: Equal(g7,g6)
    c: Equal(g8,g9)
    c: PointOnObject(g5,g6)
    c: PointOnObject(g10,g9)
    c: PointOnObject(g10,g-4)
    c: Horizontal(g10)
    c: Distance(g10) = 6.6
FEATURE [PartDesign::Pocket] Pocket018
  BaseFeature = -> Pocket014
  Direction = (0,0,-1)
  Length = 2
  Length2 = 5
  Placement = pos=(0,0,6) rot=(0,0,1;0rad)
  Profile = -> Sketch102
  ReferenceAxis = -> Sketch102 [N_Axis]
  Suppressed = false
  Type = 1
FEATURE [Sketcher::SketchObject] Sketch103
  AttachmentSupport = -> [Pocket011]
  ExternalGeometry = -> [Pocket011]
  FullyConstrained = false
  MapMode = 5
  Placement = pos=(136.73,0,6) rot=(0.57735,0.57735,0.57735;2.0944rad)
  sketch-geometry (7):
    g0: LineSegment StartX=2.5 StartY=-0.951739 StartZ=0 EndX=2.5 EndY=-3.95174 EndZ=0
    g1: LineSegment StartX=2.5 StartY=-3.95174 StartZ=0 EndX=10.5 EndY=-3.95174 EndZ=0
    g2: LineSegment StartX=10.5 StartY=-3.95174 StartZ=0 EndX=10.5 EndY=-0.951739 EndZ=0
    g3: LineSegment StartX=10.5 StartY=-0.951739 StartZ=0 EndX=2.5 EndY=-0.951739 EndZ=0
    g4: LineSegment StartX=7.67853 StartY=2.04826 StartZ=0 EndX=7.67853 EndY=-0.951739 EndZ=0
    g5: LineSegment StartX=59.5 StartY=2.04826 StartZ=0 EndX=59.5 EndY=-7.95174 EndZ=0
    g6: LineSegment StartX=10.5 StartY=-0.951739 StartZ=0 EndX=59.5 EndY=-0.951739 EndZ=0
  constraints (21):
    c: Coincident(g0,g1)
    c: Coincident(g1,g2)
    c: Coincident(g2,g3)
    c: Coincident(g3,g0)
    c: Vertical(g0)
    c: Vertical(g2)
    c: Horizontal(g1)
    c: Horizontal(g3)
    c: Vertical(g4)
    c: PointOnObject(g4,g-3)
    c: PointOnObject(g4,g3)
    c: Distance(g4) = 3
    c: Distance(g2) = 3
    c: Distance(g3) = 8
    c: Distance(g5) = 10
    c: Coincident(g5,g-4)
    c: Vertical(g5)
    c: Coincident(g6,g2)
    c: PointOnObject(g6,g5)
    c: Horizontal(g6)
    c: Distance(g6) = 49
FEATURE [PartDesign::Pocket] Pocket019
  BaseFeature = -> Pocket018
  Direction = (-1,0,0)
  Length = 3
  Length2 = 5
  Placement = pos=(0,0,6) rot=(0,0,1;0rad)
  Profile = -> Sketch103
  ReferenceAxis = -> Sketch103 [N_Axis]
  Suppressed = false
  Type = 0
FEATURE [PartDesign::Body] Body001  label="Case-Top"
  AllowCompound = false
  Group = -> [Pad,Pocket006,Sketch023,MirroredSketch003,Sketch054,Sketch058,Sketch059,Pad009,Pad008,Sketch077,Pad013,Sketch078,Pad014,Sketch079,Pocket,Sketch080,Pocket007,Sketch091,Pocket011,Sketch092,Sketch094,Pocket014,Sketch102,Pocket018,Sketch103,Pocket019]
  Origin = -> Origin001
  Tip = -> Pocket019
FEATURE [Sketcher::SketchObject] Sketch104
  AttachmentSupport = -> [XY_Plane006]
  FullyConstrained = false
  MapMode = 5
  sketch-geometry (10):
    g0: LineSegment StartX=130.577 StartY=19.5336 StartZ=0 EndX=130.577 EndY=15.4299 EndZ=0
    g1: LineSegment StartX=131.109 StartY=14.8975 StartZ=0 EndX=132.674 EndY=14.8975 EndZ=0
    g2: LineSegment StartX=133.207 StartY=15.4299 StartZ=0 EndX=133.207 EndY=19.5336 EndZ=0
    g3: LineSegment StartX=132.674 StartY=20.066 StartZ=0 EndX=131.109 EndY=20.066 EndZ=0
    g4: ArcOfCircle CenterX=131.109 CenterY=19.5336 CenterZ=0 NormalX=0 NormalY=0 NormalZ=1 AngleXU=0 Radius=0.532373 StartAngle=1.5708 EndAngle=3.14159
    g5: ArcOfCircle CenterX=131.109 CenterY=15.4299 CenterZ=0 NormalX=0 NormalY=0 NormalZ=1 AngleXU=0 Radius=0.532373 StartAngle=3.14159 EndAngle=4.71239
    g6: ArcOfCircle CenterX=132.674 CenterY=15.4299 CenterZ=0 NormalX=0 NormalY=0 NormalZ=1 AngleXU=0 Radius=0.532373 StartAngle=4.71239 EndAngle=6.28319
    g7: ArcOfCircle CenterX=132.674 CenterY=19.5336 CenterZ=0 NormalX=0 NormalY=0 NormalZ=1 AngleXU=0 Radius=0.532373 StartAngle=0 EndAngle=1.5708
    g8: GeomPoint X=130.577 Y=20.066 Z=0
    g9: GeomPoint X=133.207 Y=14.8975 Z=0
  constraints (19):
    c: Tangent(g0,g4) = -1.5708
    c: Tangent(g0,g5) = -1.5708
    c: Tangent(g1,g5) = -1.5708
    c: Tangent(g1,g6) = -1.5708
    c: Tangent(g2,g6) = -1.5708
    c: Tangent(g2,g7) = -1.5708
    c: Tangent(g3,g7) = -1.5708
    c: Tangent(g3,g4) = -1.5708
    c: Vertical(g0)
    c: Vertical(g2)
    c: Horizontal(g1)
    c: Horizontal(g3)
    c: Equal(g4,g5)
    c: Equal(g5,g6)
    c: Equal(g6,g7)
    c: PointOnObject(g8,g0)
    c: PointOnObject(g8,g3)
    c: PointOnObject(g9,g1)
    c: PointOnObject(g9,g2)
FEATURE [PartDesign::Pad] Pad025
  Direction = (0,0,1)
  Length = 3
  Length2 = 10
  Profile = -> Sketch104
  ReferenceAxis = -> Sketch104 [N_Axis]
  Suppressed = false
  Type = 0
FEATURE [Sketcher::SketchObject] Sketch105
  AttachmentSupport = -> [Pad025]
  ExternalGeometry = -> [Pad025]
  FullyConstrained = false
  MapMode = 5
  Placement = pos=(0,0,0) rot=(1,0,0;3.14159rad)
  sketch-geometry (4):
    g0: LineSegment StartX=130.577 StartY=-17.7181 StartZ=0 EndX=133.207 EndY=-17.7181 EndZ=0
    g1: LineSegment StartX=133.207 StartY=-17.7181 StartZ=0 EndX=133.207 EndY=-9.22847 EndZ=0
    g2: LineSegment StartX=133.207 StartY=-9.22847 StartZ=0 EndX=130.577 EndY=-9.22847 EndZ=0
    g3: LineSegment StartX=130.577 StartY=-9.22847 StartZ=0 EndX=130.577 EndY=-17.7181 EndZ=0
  constraints (10):
    c: Coincident(g0,g1)
    c: Coincident(g1,g2)
    c: Coincident(g2,g3)
    c: Coincident(g3,g0)
    c: Horizontal(g0)
    c: Horizontal(g2)
    c: Vertical(g1)
    c: Vertical(g3)
    c: PointOnObject(g0,g-3)
    c: PointOnObject(g1,g-4)
FEATURE [PartDesign::Pad] Pad026
  BaseFeature = -> Pad025
  Direction = (0,0,-1)
  Length = 0.5
  Length2 = 10
  Profile = -> Sketch105
  ReferenceAxis = -> Sketch105 [N_Axis]
  Reversed = true
  Suppressed = false
  Type = 0
FEATURE [PartDesign::Body] Body006  label="Boton"
  AllowCompound = false
  Group = -> [Sketch104,Pad025,Sketch105,Pad026]
  Origin = -> Origin006
  Placement = pos=(0,0,6.5) rot=(0,0,1;0rad)
  Tip = -> Pad026
FEATURE [Sketcher::SketchObject] Sketch106
  AttachmentSupport = -> [Pocket017]
  ExternalGeometry = -> [Pocket017]
  FullyConstrained = true
  MapMode = 5
  Placement = pos=(0,-2.7e-15,-18) rot=(1,0,0;3.14159rad)
  sketch-geometry (5):
    g0: Circle CenterX=61.84 CenterY=-1.51 CenterZ=0 NormalX=0 NormalY=0 NormalZ=1 AngleXU=0 Radius=2.5
    g1: Circle CenterX=108.3 CenterY=6.24 CenterZ=0 NormalX=0 NormalY=0 NormalZ=1 AngleXU=0 Radius=2.5
    g2: Circle CenterX=94.55 CenterY=-41.5 CenterZ=0 NormalX=0 NormalY=0 NormalZ=1 AngleXU=0 Radius=2.5
    g3: Circle CenterX=18.61 CenterY=-37.51 CenterZ=0 NormalX=0 NormalY=0 NormalZ=1 AngleXU=0 Radius=2.5
    g4: Circle CenterX=18.6 CenterY=-18.76 CenterZ=0 NormalX=0 NormalY=0 NormalZ=1 AngleXU=0 Radius=2.5
  constraints (10):
    c: Diameter(g0) = 5
    c: Coincident(g0,g-3)
    c: Diameter(g1) = 5
    c: Coincident(g1,g-4)
    c: Diameter(g2) = 5
    c: Coincident(g2,g-7)
    c: Diameter(g3) = 5
    c: Coincident(g3,g-6)
    c: Diameter(g4) = 5
    c: Coincident(g4,g-5)
FEATURE [PartDesign::Pocket] Pocket020
  BaseFeature = -> Pocket017
  Direction = (0,0,1)
  Length = 1
  Length2 = 5
  Placement = pos=(0,-2.7e-15,-22) rot=(0,0,1;0rad)
  Profile = -> Sketch106
  ReferenceAxis = -> Sketch106 [N_Axis]
  Suppressed = false
  Type = 0
FEATURE [Sketcher::SketchObject] Sketch107
  AttachmentSupport = -> [Pocket020]
  ExternalGeometry = -> [Pocket020]
  FullyConstrained = false
  MapMode = 5
  Placement = pos=(0,-2.7e-15,-17) rot=(1,0,0;3.14159rad)
  sketch-geometry (5):
    g0: Circle CenterX=61.84 CenterY=-1.51 CenterZ=0 NormalX=0 NormalY=0 NormalZ=1 AngleXU=0 Radius=1.26441
    g1: Circle CenterX=18.6 CenterY=-18.76 CenterZ=0 NormalX=0 NormalY=0 NormalZ=1 AngleXU=0 Radius=1.25
    g2: Circle CenterX=108.3 CenterY=6.24 CenterZ=0 NormalX=0 NormalY=0 NormalZ=1 AngleXU=0 Radius=1.25
    g3: Circle CenterX=94.55 CenterY=-41.5 CenterZ=0 NormalX=0 NormalY=0 NormalZ=1 AngleXU=0 Radius=1.25
    g4: Circle CenterX=18.61 CenterY=-37.51 CenterZ=0 NormalX=0 NormalY=0 NormalZ=1 AngleXU=0 Radius=1.25
  constraints (5):
    c: Coincident(g0,g-3)
    c: Tangent(g1,g-5) = -1.5708
    c: Tangent(g2,g-4) = -1.5708
    c: Tangent(g3,g-7) = -1.5708
    c: Tangent(g4,g-6) = -1.5708
FEATURE [PartDesign::Pad] Pad027
  BaseFeature = -> Pocket020
  Direction = (0,0,-1)
  Length = 0.24
  Length2 = 10
  Placement = pos=(0,-2.7e-15,-22) rot=(0,0,1;0rad)
  Profile = -> Sketch107
  ReferenceAxis = -> Sketch107 [N_Axis]
  Reversed = true
  Suppressed = false
  Type = 0
FEATURE [PartDesign::Body] Body  label="Bottom"
  AllowCompound = false
  Group = -> [ShapeBinder,Sketch081,Sketch082,Sketch095,Sketch096,Pad022,Pad023,ShapeBinder001,Sketch097,Pocket015,Sketch100,Pocket017,Sketch106,Pocket020,Sketch107,Pad027]
  Origin = -> Origin
  Placement = pos=(0,0,9.4) rot=(0,0,1;0rad)
  Tip = -> Pad027
